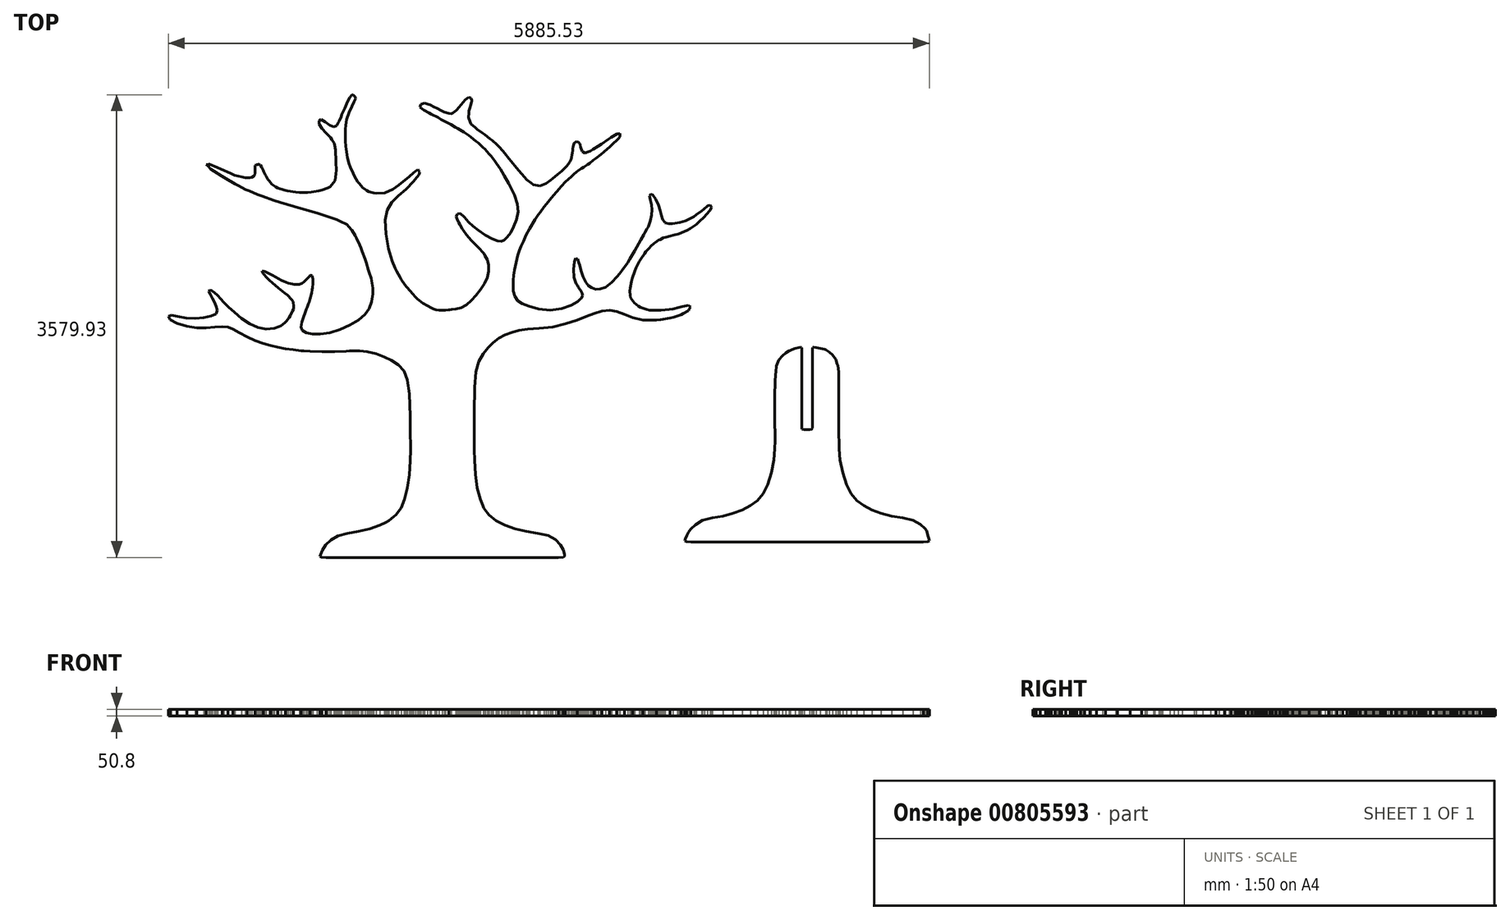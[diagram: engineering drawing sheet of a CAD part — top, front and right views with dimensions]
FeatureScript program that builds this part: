
annotation { "Feature Type Name" : "Feature", "Feature Type Description" : "" }
export const myFeature = defineFeature(function(context is Context, id is Id, definition is map)
    precondition{}
    {
        {
            var Q0;
            Q0=qCreatedBy(makeId("Top.planeOp"),FACE);
            var sketch = newSketch(context, id + "F0", { "sketchPlane" : qUnion([Q0])});
            skLineSegment(sketch, "E0", {"start": v(-5439.15, 1936.53) * mm, "end": v(-5418.75, 1946.97) * mm});
            skLineSegment(sketch, "E1", {"start": v(-5418.75, 1946.97) * mm, "end": v(-5368.69, 1938.08) * mm});
            skLineSegment(sketch, "E2", {"start": v(-5368.69, 1938.08) * mm, "end": v(-5302.09, 1925.05) * mm});
            skLineSegment(sketch, "E3", {"start": v(-5302.09, 1925.05) * mm, "end": v(-5232.04, 1923) * mm});
            skLineSegment(sketch, "E4", {"start": v(-5232.04, 1923) * mm, "end": v(-5165.29, 1928.8) * mm});
            skLineSegment(sketch, "E5", {"start": v(-5165.29, 1928.8) * mm, "end": v(-5108.52, 1939.45) * mm});
            skLineSegment(sketch, "E6", {"start": v(-5108.52, 1939.45) * mm, "end": v(-5071.25, 1957.33) * mm});
            skLineSegment(sketch, "E7", {"start": v(-5071.25, 1957.33) * mm, "end": v(-5063.03, 1984.92) * mm});
            skLineSegment(sketch, "E8", {"start": v(-5063.03, 1984.92) * mm, "end": v(-5071.2, 2016.84) * mm});
            skLineSegment(sketch, "E9", {"start": v(-5071.2, 2016.84) * mm, "end": v(-5083.17, 2047.76) * mm});
            skLineSegment(sketch, "E10", {"start": v(-5083.17, 2047.76) * mm, "end": v(-5098.53, 2078.31) * mm});
            skLineSegment(sketch, "E11", {"start": v(-5098.53, 2078.31) * mm, "end": v(-5116.97, 2109.17) * mm});
            skLineSegment(sketch, "E12", {"start": v(-5116.97, 2109.17) * mm, "end": v(-5128.35, 2132.67) * mm});
            skLineSegment(sketch, "E13", {"start": v(-5128.35, 2132.67) * mm, "end": v(-5122.64, 2141.15) * mm});
            skLineSegment(sketch, "E14", {"start": v(-5122.64, 2141.15) * mm, "end": v(-5105.5, 2136.55) * mm});
            skLineSegment(sketch, "E15", {"start": v(-5105.5, 2136.55) * mm, "end": v(-5082.68, 2120.8) * mm});
            skLineSegment(sketch, "E16", {"start": v(-5082.68, 2120.8) * mm, "end": v(-5058.38, 2098.6) * mm});
            skLineSegment(sketch, "E17", {"start": v(-5058.38, 2098.6) * mm, "end": v(-5036.81, 2074.63) * mm});
            skLineSegment(sketch, "E18", {"start": v(-5036.81, 2074.63) * mm, "end": v(-5011.36, 2046.2) * mm});
            skLineSegment(sketch, "E19", {"start": v(-5011.36, 2046.2) * mm, "end": v(-4975.47, 2010.62) * mm});
            skLineSegment(sketch, "E20", {"start": v(-4975.47, 2010.62) * mm, "end": v(-4929.45, 1968.96) * mm});
            skLineSegment(sketch, "E21", {"start": v(-4929.45, 1968.96) * mm, "end": v(-4873.5, 1922.33) * mm});
            skLineSegment(sketch, "E22", {"start": v(-4873.5, 1922.33) * mm, "end": v(-4811.51, 1880.12) * mm});
            skLineSegment(sketch, "E23", {"start": v(-4811.51, 1880.12) * mm, "end": v(-4747.35, 1851.74) * mm});
            skLineSegment(sketch, "E24", {"start": v(-4747.35, 1851.74) * mm, "end": v(-4683.35, 1839.17) * mm});
            skLineSegment(sketch, "E25", {"start": v(-4683.35, 1839.17) * mm, "end": v(-4621.88, 1844.4) * mm});
            skLineSegment(sketch, "E26", {"start": v(-4621.88, 1844.4) * mm, "end": v(-4585.12, 1858.53) * mm});
            skLineSegment(sketch, "E27", {"start": v(-4585.12, 1858.53) * mm, "end": v(-4568.23, 1865) * mm});
            skLineSegment(sketch, "E28", {"start": v(-4568.23, 1865) * mm, "end": v(-4540.47, 1887.99) * mm});
            skLineSegment(sketch, "E29", {"start": v(-4540.47, 1887.99) * mm, "end": v(-4527.72, 1898.56) * mm});
            skLineSegment(sketch, "E30", {"start": v(-4527.72, 1898.56) * mm, "end": v(-4506.61, 1928.9) * mm});
            skLineSegment(sketch, "E31", {"start": v(-4506.61, 1928.9) * mm, "end": v(-4496.9, 1942.83) * mm});
            skLineSegment(sketch, "E32", {"start": v(-4496.9, 1942.83) * mm, "end": v(-4480.1, 1979) * mm});
            skLineSegment(sketch, "E33", {"start": v(-4480.1, 1979) * mm, "end": v(-4480.1, 1979) * mm});
            skLineSegment(sketch, "E34", {"start": v(-4480.1, 1979) * mm, "end": v(-4472.35, 1995.58) * mm});
            skLineSegment(sketch, "E35", {"start": v(-4472.35, 1995.58) * mm, "end": v(-4472.35, 1995.58) * mm});
            skLineSegment(sketch, "E36", {"start": v(-4472.35, 1995.58) * mm, "end": v(-4472.65, 2012.93) * mm});
            skLineSegment(sketch, "E37", {"start": v(-4472.65, 2012.93) * mm, "end": v(-4473.34, 2050.75) * mm});
            skLineSegment(sketch, "E38", {"start": v(-4473.34, 2050.75) * mm, "end": v(-4473.34, 2050.75) * mm});
            skLineSegment(sketch, "E39", {"start": v(-4473.34, 2050.75) * mm, "end": v(-4487.74, 2066.98) * mm});
            skLineSegment(sketch, "E40", {"start": v(-4487.74, 2066.98) * mm, "end": v(-4519.13, 2102.31) * mm});
            skLineSegment(sketch, "E41", {"start": v(-4519.13, 2102.31) * mm, "end": v(-4519.14, 2102.32) * mm});
            skLineSegment(sketch, "E42", {"start": v(-4519.14, 2102.32) * mm, "end": v(-4540.78, 2119.18) * mm});
            skLineSegment(sketch, "E43", {"start": v(-4540.78, 2119.18) * mm, "end": v(-4587.87, 2155.88) * mm});
            skLineSegment(sketch, "E44", {"start": v(-4587.87, 2155.88) * mm, "end": v(-4635.72, 2197.87) * mm});
            skLineSegment(sketch, "E45", {"start": v(-4635.72, 2197.87) * mm, "end": v(-4657.67, 2217.1) * mm});
            skLineSegment(sketch, "E46", {"start": v(-4657.67, 2217.1) * mm, "end": v(-4673.31, 2233) * mm});
            skLineSegment(sketch, "E47", {"start": v(-4673.31, 2233) * mm, "end": v(-4707.5, 2267.72) * mm});
            skLineSegment(sketch, "E48", {"start": v(-4707.5, 2267.72) * mm, "end": v(-4707.5, 2267.72) * mm});
            skLineSegment(sketch, "E49", {"start": v(-4707.5, 2267.72) * mm, "end": v(-4710.24, 2274.53) * mm});
            skLineSegment(sketch, "E50", {"start": v(-4710.24, 2274.53) * mm, "end": v(-4716.4, 2289.46) * mm});
            skLineSegment(sketch, "E51", {"start": v(-4716.4, 2289.46) * mm, "end": v(-4698.13, 2285.83) * mm});
            skLineSegment(sketch, "E52", {"start": v(-4698.13, 2285.83) * mm, "end": v(-4689.65, 2284.13) * mm});
            skLineSegment(sketch, "E53", {"start": v(-4689.65, 2284.13) * mm, "end": v(-4650.66, 2263.17) * mm});
            skLineSegment(sketch, "E54", {"start": v(-4650.66, 2263.17) * mm, "end": v(-4632.6, 2253.5) * mm});
            skLineSegment(sketch, "E55", {"start": v(-4632.6, 2253.5) * mm, "end": v(-4587.33, 2228.63) * mm});
            skLineSegment(sketch, "E56", {"start": v(-4587.33, 2228.63) * mm, "end": v(-4566.4, 2217.15) * mm});
            skLineSegment(sketch, "E57", {"start": v(-4566.4, 2217.15) * mm, "end": v(-4529.24, 2201.7) * mm});
            skLineSegment(sketch, "E58", {"start": v(-4529.24, 2201.7) * mm, "end": v(-4512.2, 2194.62) * mm});
            skLineSegment(sketch, "E59", {"start": v(-4512.2, 2194.62) * mm, "end": v(-4481.06, 2187.7) * mm});
            skLineSegment(sketch, "E60", {"start": v(-4481.06, 2187.7) * mm, "end": v(-4466.84, 2184.56) * mm});
            skLineSegment(sketch, "E61", {"start": v(-4466.84, 2184.56) * mm, "end": v(-4439.58, 2185.27) * mm});
            skLineSegment(sketch, "E62", {"start": v(-4439.58, 2185.27) * mm, "end": v(-4427.19, 2185.65) * mm});
            skLineSegment(sketch, "E63", {"start": v(-4427.19, 2185.65) * mm, "end": v(-4404.07, 2195.46) * mm});
            skLineSegment(sketch, "E64", {"start": v(-4404.07, 2195.46) * mm, "end": v(-4393.6, 2200.03) * mm});
            skLineSegment(sketch, "E65", {"start": v(-4393.6, 2200.03) * mm, "end": v(-4374.94, 2220.45) * mm});
            skLineSegment(sketch, "E66", {"start": v(-4374.94, 2220.45) * mm, "end": v(-4366.48, 2229.9) * mm});
            skLineSegment(sketch, "E67", {"start": v(-4366.48, 2229.9) * mm, "end": v(-4351.92, 2246.71) * mm});
            skLineSegment(sketch, "E68", {"start": v(-4351.92, 2246.71) * mm, "end": v(-4351.92, 2246.71) * mm});
            skLineSegment(sketch, "E69", {"start": v(-4351.92, 2246.71) * mm, "end": v(-4345.32, 2254.49) * mm});
            skLineSegment(sketch, "E70", {"start": v(-4345.32, 2254.49) * mm, "end": v(-4334.6, 2253.5) * mm});
            skLineSegment(sketch, "E71", {"start": v(-4334.6, 2253.5) * mm, "end": v(-4334.6, 2253.5) * mm});
            skLineSegment(sketch, "E72", {"start": v(-4334.6, 2253.5) * mm, "end": v(-4329.7, 2253.06) * mm});
            skLineSegment(sketch, "E73", {"start": v(-4329.7, 2253.06) * mm, "end": v(-4323.99, 2237.32) * mm});
            skLineSegment(sketch, "E74", {"start": v(-4323.99, 2237.32) * mm, "end": v(-4323.99, 2237.32) * mm});
            skLineSegment(sketch, "E75", {"start": v(-4323.99, 2237.32) * mm, "end": v(-4323.99, 2237.31) * mm});
            skLineSegment(sketch, "E76", {"start": v(-4323.99, 2237.31) * mm, "end": v(-4321.35, 2230.08) * mm});
            skLineSegment(sketch, "E77", {"start": v(-4321.35, 2230.08) * mm, "end": v(-4321.85, 2202.6) * mm});
            skLineSegment(sketch, "E78", {"start": v(-4321.85, 2202.6) * mm, "end": v(-4321.85, 2202.6) * mm});
            skLineSegment(sketch, "E79", {"start": v(-4321.85, 2202.6) * mm, "end": v(-4322.03, 2189.97) * mm});
            skLineSegment(sketch, "E80", {"start": v(-4322.03, 2189.97) * mm, "end": v(-4325.84, 2159.26) * mm});
            skLineSegment(sketch, "E81", {"start": v(-4325.84, 2159.26) * mm, "end": v(-4325.84, 2159.26) * mm});
            skLineSegment(sketch, "E82", {"start": v(-4325.84, 2159.26) * mm, "end": v(-4327.54, 2145.16) * mm});
            skLineSegment(sketch, "E83", {"start": v(-4327.54, 2145.16) * mm, "end": v(-4331.84, 2119.76) * mm});
            skLineSegment(sketch, "E84", {"start": v(-4331.84, 2119.76) * mm, "end": v(-4333.8, 2108.1) * mm});
            skLineSegment(sketch, "E85", {"start": v(-4333.8, 2108.1) * mm, "end": v(-4339.76, 2084.43) * mm});
            skLineSegment(sketch, "E86", {"start": v(-4339.76, 2084.43) * mm, "end": v(-4339.76, 2084.43) * mm});
            skLineSegment(sketch, "E87", {"start": v(-4339.76, 2084.43) * mm, "end": v(-4342.55, 2073.59) * mm});
            skLineSegment(sketch, "E88", {"start": v(-4342.55, 2073.59) * mm, "end": v(-4351.5, 2048.06) * mm});
            skLineSegment(sketch, "E89", {"start": v(-4351.5, 2048.06) * mm, "end": v(-4355.64, 2036.38) * mm});
            skLineSegment(sketch, "E90", {"start": v(-4355.64, 2036.38) * mm, "end": v(-4367.01, 2006.89) * mm});
            skLineSegment(sketch, "E91", {"start": v(-4367.01, 2006.89) * mm, "end": v(-4372.3, 1993.37) * mm});
            skLineSegment(sketch, "E92", {"start": v(-4372.3, 1993.37) * mm, "end": v(-4385.58, 1957.79) * mm});
            skLineSegment(sketch, "E93", {"start": v(-4385.58, 1957.79) * mm, "end": v(-4391.68, 1941.45) * mm});
            skLineSegment(sketch, "E94", {"start": v(-4391.68, 1941.45) * mm, "end": v(-4407.43, 1891.67) * mm});
            skLineSegment(sketch, "E95", {"start": v(-4407.43, 1891.67) * mm, "end": v(-4413.06, 1855.02) * mm});
            skLineSegment(sketch, "E96", {"start": v(-4413.06, 1855.02) * mm, "end": v(-4403.23, 1829.04) * mm});
            skLineSegment(sketch, "E97", {"start": v(-4403.23, 1829.04) * mm, "end": v(-4372.6, 1811.23) * mm});
            skLineSegment(sketch, "E98", {"start": v(-4372.6, 1811.23) * mm, "end": v(-4339.84, 1804.53) * mm});
            skLineSegment(sketch, "E99", {"start": v(-4339.84, 1804.53) * mm, "end": v(-4324.8, 1801.45) * mm});
            skLineSegment(sketch, "E100", {"start": v(-4324.8, 1801.45) * mm, "end": v(-4282.81, 1800.18) * mm});
            skLineSegment(sketch, "E101", {"start": v(-4282.81, 1800.18) * mm, "end": v(-4263.53, 1799.6) * mm});
            skLineSegment(sketch, "E102", {"start": v(-4263.53, 1799.6) * mm, "end": v(-4191.88, 1809.78) * mm});
            skLineSegment(sketch, "E103", {"start": v(-4191.88, 1809.78) * mm, "end": v(-4112.86, 1836.22) * mm});
            skLineSegment(sketch, "E104", {"start": v(-4112.86, 1836.22) * mm, "end": v(-4035.72, 1871.99) * mm});
            skLineSegment(sketch, "E105", {"start": v(-4035.72, 1871.99) * mm, "end": v(-3969.58, 1910.09) * mm});
            skLineSegment(sketch, "E106", {"start": v(-3969.58, 1910.09) * mm, "end": v(-3918.22, 1952) * mm});
            skLineSegment(sketch, "E107", {"start": v(-3918.22, 1952) * mm, "end": v(-3885.3, 1999.24) * mm});
            skLineSegment(sketch, "E108", {"start": v(-3885.3, 1999.24) * mm, "end": v(-3866.79, 2052.68) * mm});
            skLineSegment(sketch, "E109", {"start": v(-3866.79, 2052.68) * mm, "end": v(-3858.6, 2113.21) * mm});
            skLineSegment(sketch, "E110", {"start": v(-3858.6, 2113.21) * mm, "end": v(-3859.85, 2155.58) * mm});
            skLineSegment(sketch, "E111", {"start": v(-3859.85, 2155.58) * mm, "end": v(-3860.41, 2175.06) * mm});
            skLineSegment(sketch, "E112", {"start": v(-3860.41, 2175.06) * mm, "end": v(-3868.2, 2214.35) * mm});
            skLineSegment(sketch, "E113", {"start": v(-3868.2, 2214.35) * mm, "end": v(-3871.8, 2232.46) * mm});
            skLineSegment(sketch, "E114", {"start": v(-3871.8, 2232.46) * mm, "end": v(-3885.4, 2276.71) * mm});
            skLineSegment(sketch, "E115", {"start": v(-3885.4, 2276.71) * mm, "end": v(-3891.65, 2297.06) * mm});
            skLineSegment(sketch, "E116", {"start": v(-3891.65, 2297.06) * mm, "end": v(-3910.37, 2354.3) * mm});
            skLineSegment(sketch, "E117", {"start": v(-3910.37, 2354.3) * mm, "end": v(-3918.96, 2380.47) * mm});
            skLineSegment(sketch, "E118", {"start": v(-3918.96, 2380.47) * mm, "end": v(-3940.78, 2440.26) * mm});
            skLineSegment(sketch, "E119", {"start": v(-3940.78, 2440.26) * mm, "end": v(-3950.76, 2467.6) * mm});
            skLineSegment(sketch, "E120", {"start": v(-3950.76, 2467.6) * mm, "end": v(-3961.25, 2491.4) * mm});
            skLineSegment(sketch, "E121", {"start": v(-3961.25, 2491.4) * mm, "end": v(-3984.1, 2543.23) * mm});
            skLineSegment(sketch, "E122", {"start": v(-3984.1, 2543.23) * mm, "end": v(-3995.39, 2562.51) * mm});
            skLineSegment(sketch, "E123", {"start": v(-3995.39, 2562.51) * mm, "end": v(-4020.02, 2604.4) * mm});
            skLineSegment(sketch, "E124", {"start": v(-4020.02, 2604.4) * mm, "end": v(-4047.15, 2634.24) * mm});
            skLineSegment(sketch, "E125", {"start": v(-4047.15, 2634.24) * mm, "end": v(-4059.6, 2647.96) * mm});
            skLineSegment(sketch, "E126", {"start": v(-4059.6, 2647.96) * mm, "end": v(-4113.42, 2675.03) * mm});
            skLineSegment(sketch, "E127", {"start": v(-4113.42, 2675.03) * mm, "end": v(-4138.06, 2687.43) * mm});
            skLineSegment(sketch, "E128", {"start": v(-4138.06, 2687.43) * mm, "end": v(-4242.86, 2721.03) * mm});
            skLineSegment(sketch, "E129", {"start": v(-4242.86, 2721.03) * mm, "end": v(-4290.61, 2736.32) * mm});
            skLineSegment(sketch, "E130", {"start": v(-4290.61, 2736.32) * mm, "end": v(-4413.4, 2772.04) * mm});
            skLineSegment(sketch, "E131", {"start": v(-4413.4, 2772.04) * mm, "end": v(-4469.05, 2788.21) * mm});
            skLineSegment(sketch, "E132", {"start": v(-4469.05, 2788.21) * mm, "end": v(-4576.44, 2821.57) * mm});
            skLineSegment(sketch, "E133", {"start": v(-4576.44, 2821.57) * mm, "end": v(-4625.15, 2836.7) * mm});
            skLineSegment(sketch, "E134", {"start": v(-4625.15, 2836.7) * mm, "end": v(-4712.25, 2867.03) * mm});
            skLineSegment(sketch, "E135", {"start": v(-4712.25, 2867.03) * mm, "end": v(-4751.9, 2880.82) * mm});
            skLineSegment(sketch, "E136", {"start": v(-4751.9, 2880.82) * mm, "end": v(-4813.9, 2907.52) * mm});
            skLineSegment(sketch, "E137", {"start": v(-4813.9, 2907.52) * mm, "end": v(-4842.25, 2919.7) * mm});
            skLineSegment(sketch, "E138", {"start": v(-4842.25, 2919.7) * mm, "end": v(-4898.64, 2949.81) * mm});
            skLineSegment(sketch, "E139", {"start": v(-4898.64, 2949.81) * mm, "end": v(-4924.5, 2963.6) * mm});
            skLineSegment(sketch, "E140", {"start": v(-4924.5, 2963.6) * mm, "end": v(-4994.67, 3004.07) * mm});
            skLineSegment(sketch, "E141", {"start": v(-4994.67, 3004.07) * mm, "end": v(-5027.03, 3022.7) * mm});
            skLineSegment(sketch, "E142", {"start": v(-5027.03, 3022.7) * mm, "end": v(-5085.86, 3061.04) * mm});
            skLineSegment(sketch, "E143", {"start": v(-5085.86, 3061.04) * mm, "end": v(-5113.11, 3078.76) * mm});
            skLineSegment(sketch, "E144", {"start": v(-5113.11, 3078.76) * mm, "end": v(-5135.54, 3102.5) * mm});
            skLineSegment(sketch, "E145", {"start": v(-5135.54, 3102.5) * mm, "end": v(-5135.54, 3102.5) * mm});
            skLineSegment(sketch, "E146", {"start": v(-5135.54, 3102.5) * mm, "end": v(-5145.96, 3113.51) * mm});
            skLineSegment(sketch, "E147", {"start": v(-5145.96, 3113.51) * mm, "end": v(-5128.79, 3115.4) * mm});
            skLineSegment(sketch, "E148", {"start": v(-5128.79, 3115.4) * mm, "end": v(-5128.79, 3115.4) * mm});
            skLineSegment(sketch, "E149", {"start": v(-5128.79, 3115.4) * mm, "end": v(-5120.84, 3116.28) * mm});
            skLineSegment(sketch, "E150", {"start": v(-5120.84, 3116.28) * mm, "end": v(-5060.76, 3089.05) * mm});
            skLineSegment(sketch, "E151", {"start": v(-5060.76, 3089.05) * mm, "end": v(-5033.03, 3076.48) * mm});
            skLineSegment(sketch, "E152", {"start": v(-5033.03, 3076.48) * mm, "end": v(-4960.18, 3044.25) * mm});
            skLineSegment(sketch, "E153", {"start": v(-4960.18, 3044.25) * mm, "end": v(-4926.7, 3029.44) * mm});
            skLineSegment(sketch, "E154", {"start": v(-4926.7, 3029.44) * mm, "end": v(-4871.36, 3016.46) * mm});
            skLineSegment(sketch, "E155", {"start": v(-4871.36, 3016.46) * mm, "end": v(-4846.03, 3010.52) * mm});
            skLineSegment(sketch, "E156", {"start": v(-4846.03, 3010.52) * mm, "end": v(-4810.02, 3012.17) * mm});
            skLineSegment(sketch, "E157", {"start": v(-4810.02, 3012.17) * mm, "end": v(-4793.56, 3012.93) * mm});
            skLineSegment(sketch, "E158", {"start": v(-4793.56, 3012.93) * mm, "end": v(-4793.56, 3012.93) * mm});
            skLineSegment(sketch, "E159", {"start": v(-4793.56, 3012.93) * mm, "end": v(-4793.55, 3012.93) * mm});
            skLineSegment(sketch, "E160", {"start": v(-4793.55, 3012.93) * mm, "end": v(-4778.65, 3024.59) * mm});
            skLineSegment(sketch, "E161", {"start": v(-4778.65, 3024.59) * mm, "end": v(-4771.86, 3029.9) * mm});
            skLineSegment(sketch, "E162", {"start": v(-4771.86, 3029.9) * mm, "end": v(-4769.22, 3047.3) * mm});
            skLineSegment(sketch, "E163", {"start": v(-4769.22, 3047.3) * mm, "end": v(-4769.22, 3047.3) * mm});
            skLineSegment(sketch, "E164", {"start": v(-4769.22, 3047.3) * mm, "end": v(-4768.03, 3055.25) * mm});
            skLineSegment(sketch, "E165", {"start": v(-4768.03, 3055.25) * mm, "end": v(-4768.03, 3055.25) * mm});
            skLineSegment(sketch, "E166", {"start": v(-4768.03, 3055.25) * mm, "end": v(-4768.87, 3074.17) * mm});
            skLineSegment(sketch, "E167", {"start": v(-4768.87, 3074.17) * mm, "end": v(-4768.87, 3074.17) * mm});
            skLineSegment(sketch, "E168", {"start": v(-4768.87, 3074.17) * mm, "end": v(-4769.25, 3082.8) * mm});
            skLineSegment(sketch, "E169", {"start": v(-4769.25, 3082.8) * mm, "end": v(-4769.25, 3082.8) * mm});
            skLineSegment(sketch, "E170", {"start": v(-4769.25, 3082.8) * mm, "end": v(-4768.9, 3097.77) * mm});
            skLineSegment(sketch, "E171", {"start": v(-4768.9, 3097.77) * mm, "end": v(-4768.9, 3097.77) * mm});
            skLineSegment(sketch, "E172", {"start": v(-4768.9, 3097.77) * mm, "end": v(-4768.72, 3104.6) * mm});
            skLineSegment(sketch, "E173", {"start": v(-4768.72, 3104.6) * mm, "end": v(-4762.52, 3110.09) * mm});
            skLineSegment(sketch, "E174", {"start": v(-4762.52, 3110.09) * mm, "end": v(-4762.52, 3110.09) * mm});
            skLineSegment(sketch, "E175", {"start": v(-4762.52, 3110.09) * mm, "end": v(-4759.7, 3112.57) * mm});
            skLineSegment(sketch, "E176", {"start": v(-4759.7, 3112.57) * mm, "end": v(-4759.7, 3112.57) * mm});
            skLineSegment(sketch, "E177", {"start": v(-4759.7, 3112.57) * mm, "end": v(-4751.24, 3113.29) * mm});
            skLineSegment(sketch, "E178", {"start": v(-4751.24, 3113.29) * mm, "end": v(-4751.24, 3113.29) * mm});
            skLineSegment(sketch, "E179", {"start": v(-4751.24, 3113.29) * mm, "end": v(-4747.35, 3113.6) * mm});
            skLineSegment(sketch, "E180", {"start": v(-4747.35, 3113.6) * mm, "end": v(-4740.22, 3114.17) * mm});
            skLineSegment(sketch, "E181", {"start": v(-4740.22, 3114.17) * mm, "end": v(-4740.22, 3114.17) * mm});
            skLineSegment(sketch, "E182", {"start": v(-4740.22, 3114.17) * mm, "end": v(-4736.94, 3114.45) * mm});
            skLineSegment(sketch, "E183", {"start": v(-4736.94, 3114.45) * mm, "end": v(-4736.94, 3114.45) * mm});
            skLineSegment(sketch, "E184", {"start": v(-4736.94, 3114.45) * mm, "end": v(-4729.98, 3110.14) * mm});
            skLineSegment(sketch, "E185", {"start": v(-4729.98, 3110.14) * mm, "end": v(-4729.98, 3110.14) * mm});
            skLineSegment(sketch, "E186", {"start": v(-4729.98, 3110.14) * mm, "end": v(-4726.8, 3108.18) * mm});
            skLineSegment(sketch, "E187", {"start": v(-4726.8, 3108.18) * mm, "end": v(-4718.9, 3094.13) * mm});
            skLineSegment(sketch, "E188", {"start": v(-4718.9, 3094.13) * mm, "end": v(-4718.9, 3094.13) * mm});
            skLineSegment(sketch, "E189", {"start": v(-4718.9, 3094.13) * mm, "end": v(-4715.32, 3087.76) * mm});
            skLineSegment(sketch, "E190", {"start": v(-4715.32, 3087.76) * mm, "end": v(-4705.75, 3067.24) * mm});
            skLineSegment(sketch, "E191", {"start": v(-4705.75, 3067.24) * mm, "end": v(-4701.4, 3057.89) * mm});
            skLineSegment(sketch, "E192", {"start": v(-4701.4, 3057.89) * mm, "end": v(-4689.4, 3034.11) * mm});
            skLineSegment(sketch, "E193", {"start": v(-4689.4, 3034.11) * mm, "end": v(-4689.4, 3034.11) * mm});
            skLineSegment(sketch, "E194", {"start": v(-4689.4, 3034.11) * mm, "end": v(-4683.93, 3023.3) * mm});
            skLineSegment(sketch, "E195", {"start": v(-4683.93, 3023.3) * mm, "end": v(-4683.93, 3023.3) * mm});
            skLineSegment(sketch, "E196", {"start": v(-4683.93, 3023.3) * mm, "end": v(-4669.6, 2999.44) * mm});
            skLineSegment(sketch, "E197", {"start": v(-4669.6, 2999.44) * mm, "end": v(-4663.1, 2988.62) * mm});
            skLineSegment(sketch, "E198", {"start": v(-4663.1, 2988.62) * mm, "end": v(-4646.54, 2967.92) * mm});
            skLineSegment(sketch, "E199", {"start": v(-4646.54, 2967.92) * mm, "end": v(-4639.02, 2958.52) * mm});
            skLineSegment(sketch, "E200", {"start": v(-4639.02, 2958.52) * mm, "end": v(-4639.02, 2958.52) * mm});
            skLineSegment(sketch, "E201", {"start": v(-4639.02, 2958.52) * mm, "end": v(-4609.6, 2940.44) * mm});
            skLineSegment(sketch, "E202", {"start": v(-4609.6, 2940.44) * mm, "end": v(-4596.3, 2932.26) * mm});
            skLineSegment(sketch, "E203", {"start": v(-4596.3, 2932.26) * mm, "end": v(-4543.37, 2916.28) * mm});
            skLineSegment(sketch, "E204", {"start": v(-4543.37, 2916.28) * mm, "end": v(-4519.47, 2909.07) * mm});
            skLineSegment(sketch, "E205", {"start": v(-4519.47, 2909.07) * mm, "end": v(-4455, 2899.85) * mm});
            skLineSegment(sketch, "E206", {"start": v(-4455, 2899.85) * mm, "end": v(-4425.9, 2895.68) * mm});
            skLineSegment(sketch, "E207", {"start": v(-4425.9, 2895.68) * mm, "end": v(-4361.96, 2897.84) * mm});
            skLineSegment(sketch, "E208", {"start": v(-4361.96, 2897.84) * mm, "end": v(-4333, 2898.8) * mm});
            skLineSegment(sketch, "E209", {"start": v(-4333, 2898.8) * mm, "end": v(-4276.46, 2909.88) * mm});
            skLineSegment(sketch, "E210", {"start": v(-4276.46, 2909.88) * mm, "end": v(-4276.46, 2909.88) * mm});
            skLineSegment(sketch, "E211", {"start": v(-4276.46, 2909.88) * mm, "end": v(-4250.73, 2914.91) * mm});
            skLineSegment(sketch, "E212", {"start": v(-4250.73, 2914.91) * mm, "end": v(-4208.4, 2932.4) * mm});
            skLineSegment(sketch, "E213", {"start": v(-4208.4, 2932.4) * mm, "end": v(-4208.4, 2932.41) * mm});
            skLineSegment(sketch, "E214", {"start": v(-4208.4, 2932.41) * mm, "end": v(-4189.06, 2940.39) * mm});
            skLineSegment(sketch, "E215", {"start": v(-4189.06, 2940.39) * mm, "end": v(-4163.18, 2972.8) * mm});
            skLineSegment(sketch, "E216", {"start": v(-4163.18, 2972.8) * mm, "end": v(-4151.32, 2987.63) * mm});
            skLineSegment(sketch, "E217", {"start": v(-4151.32, 2987.63) * mm, "end": v(-4144.15, 3043.44) * mm});
            skLineSegment(sketch, "E218", {"start": v(-4144.15, 3043.44) * mm, "end": v(-4140.88, 3069.04) * mm});
            skLineSegment(sketch, "E219", {"start": v(-4140.88, 3069.04) * mm, "end": v(-4142.96, 3129.67) * mm});
            skLineSegment(sketch, "E220", {"start": v(-4142.96, 3129.67) * mm, "end": v(-4143.92, 3157.48) * mm});
            skLineSegment(sketch, "E221", {"start": v(-4143.92, 3157.48) * mm, "end": v(-4145.8, 3204.4) * mm});
            skLineSegment(sketch, "E222", {"start": v(-4145.8, 3204.4) * mm, "end": v(-4146.67, 3225.93) * mm});
            skLineSegment(sketch, "E223", {"start": v(-4146.67, 3225.93) * mm, "end": v(-4154.04, 3262.18) * mm});
            skLineSegment(sketch, "E224", {"start": v(-4154.04, 3262.18) * mm, "end": v(-4157.41, 3278.8) * mm});
            skLineSegment(sketch, "E225", {"start": v(-4157.41, 3278.8) * mm, "end": v(-4175.96, 3307.42) * mm});
            skLineSegment(sketch, "E226", {"start": v(-4175.96, 3307.42) * mm, "end": v(-4184.46, 3320.55) * mm});
            skLineSegment(sketch, "E227", {"start": v(-4184.46, 3320.55) * mm, "end": v(-4218.98, 3356.82) * mm});
            skLineSegment(sketch, "E228", {"start": v(-4218.98, 3356.82) * mm, "end": v(-4252.18, 3393.14) * mm});
            skLineSegment(sketch, "E229", {"start": v(-4252.18, 3393.14) * mm, "end": v(-4274.1, 3426.14) * mm});
            skLineSegment(sketch, "E230", {"start": v(-4274.1, 3426.14) * mm, "end": v(-4274.1, 3426.14) * mm});
            skLineSegment(sketch, "E231", {"start": v(-4274.1, 3426.14) * mm, "end": v(-4274.84, 3452.35) * mm});
            skLineSegment(sketch, "E232", {"start": v(-4274.84, 3452.35) * mm, "end": v(-4257.62, 3461.3) * mm});
            skLineSegment(sketch, "E233", {"start": v(-4257.62, 3461.3) * mm, "end": v(-4225.8, 3442.52) * mm});
            skLineSegment(sketch, "E234", {"start": v(-4225.8, 3442.52) * mm, "end": v(-4190.1, 3417) * mm});
            skLineSegment(sketch, "E235", {"start": v(-4190.1, 3417) * mm, "end": v(-4161.33, 3405.72) * mm});
            skLineSegment(sketch, "E236", {"start": v(-4161.33, 3405.72) * mm, "end": v(-4137.78, 3414.48) * mm});
            skLineSegment(sketch, "E237", {"start": v(-4137.78, 3414.48) * mm, "end": v(-4124.04, 3438.25) * mm});
            skLineSegment(sketch, "E238", {"start": v(-4124.04, 3438.25) * mm, "end": v(-4124.04, 3438.25) * mm});
            skLineSegment(sketch, "E239", {"start": v(-4124.04, 3438.25) * mm, "end": v(-4117.71, 3449.15) * mm});
            skLineSegment(sketch, "E240", {"start": v(-4117.71, 3449.15) * mm, "end": v(-4104.25, 3482.83) * mm});
            skLineSegment(sketch, "E241", {"start": v(-4104.25, 3482.83) * mm, "end": v(-4104.25, 3482.83) * mm});
            skLineSegment(sketch, "E242", {"start": v(-4104.25, 3482.83) * mm, "end": v(-4098.08, 3498.27) * mm});
            skLineSegment(sketch, "E243", {"start": v(-4098.08, 3498.27) * mm, "end": v(-4075.78, 3550.4) * mm});
            skLineSegment(sketch, "E244", {"start": v(-4075.78, 3550.4) * mm, "end": v(-4053.73, 3597.66) * mm});
            skLineSegment(sketch, "E245", {"start": v(-4053.73, 3597.66) * mm, "end": v(-4034.88, 3632.18) * mm});
            skLineSegment(sketch, "E246", {"start": v(-4034.88, 3632.18) * mm, "end": v(-4019.85, 3651.1) * mm});
            skLineSegment(sketch, "E247", {"start": v(-4019.85, 3651.1) * mm, "end": v(-4019.85, 3651.1) * mm});
            skLineSegment(sketch, "E248", {"start": v(-4019.85, 3651.1) * mm, "end": v(-4009.26, 3651.59) * mm});
            skLineSegment(sketch, "E249", {"start": v(-4009.26, 3651.59) * mm, "end": v(-4001.2, 3643.13) * mm});
            skLineSegment(sketch, "E250", {"start": v(-4001.2, 3643.13) * mm, "end": v(-4001.2, 3643.13) * mm});
            skLineSegment(sketch, "E251", {"start": v(-4001.2, 3643.13) * mm, "end": v(-3993.71, 3635.28) * mm});
            skLineSegment(sketch, "E252", {"start": v(-3993.71, 3635.28) * mm, "end": v(-3993.71, 3635.28) * mm});
            skLineSegment(sketch, "E253", {"start": v(-3993.71, 3635.28) * mm, "end": v(-3992.44, 3622.38) * mm});
            skLineSegment(sketch, "E254", {"start": v(-3992.44, 3622.38) * mm, "end": v(-4003.1, 3598.8) * mm});
            skLineSegment(sketch, "E255", {"start": v(-4003.1, 3598.8) * mm, "end": v(-4021.17, 3563.32) * mm});
            skLineSegment(sketch, "E256", {"start": v(-4021.17, 3563.32) * mm, "end": v(-4042.1, 3514.78) * mm});
            skLineSegment(sketch, "E257", {"start": v(-4042.1, 3514.78) * mm, "end": v(-4060.1, 3462.66) * mm});
            skLineSegment(sketch, "E258", {"start": v(-4060.1, 3462.66) * mm, "end": v(-4069.3, 3416.54) * mm});
            skLineSegment(sketch, "E259", {"start": v(-4069.3, 3416.54) * mm, "end": v(-4071.51, 3384.25) * mm});
            skLineSegment(sketch, "E260", {"start": v(-4071.51, 3384.25) * mm, "end": v(-4072.52, 3369.42) * mm});
            skLineSegment(sketch, "E261", {"start": v(-4072.52, 3369.42) * mm, "end": v(-4072.58, 3331.7) * mm});
            skLineSegment(sketch, "E262", {"start": v(-4072.58, 3331.7) * mm, "end": v(-4072.58, 3331.7) * mm});
            skLineSegment(sketch, "E263", {"start": v(-4072.58, 3331.7) * mm, "end": v(-4072.6, 3314.4) * mm});
            skLineSegment(sketch, "E264", {"start": v(-4072.6, 3314.4) * mm, "end": v(-4071.3, 3295.12) * mm});
            skLineSegment(sketch, "E265", {"start": v(-4071.3, 3295.12) * mm, "end": v(-4068.49, 3253.09) * mm});
            skLineSegment(sketch, "E266", {"start": v(-4068.49, 3253.09) * mm, "end": v(-4068.49, 3253.09) * mm});
            skLineSegment(sketch, "E267", {"start": v(-4068.49, 3253.09) * mm, "end": v(-4065.57, 3232.39) * mm});
            skLineSegment(sketch, "E268", {"start": v(-4065.57, 3232.39) * mm, "end": v(-4059.2, 3187.15) * mm});
            skLineSegment(sketch, "E269", {"start": v(-4059.2, 3187.15) * mm, "end": v(-4053.6, 3165.23) * mm});
            skLineSegment(sketch, "E270", {"start": v(-4053.6, 3165.23) * mm, "end": v(-4041.39, 3117.4) * mm});
            skLineSegment(sketch, "E271", {"start": v(-4041.39, 3117.4) * mm, "end": v(-4032.09, 3094.49) * mm});
            skLineSegment(sketch, "E272", {"start": v(-4032.09, 3094.49) * mm, "end": v(-4011.8, 3044.65) * mm});
            skLineSegment(sketch, "E273", {"start": v(-4011.8, 3044.65) * mm, "end": v(-4011.8, 3044.65) * mm});
            skLineSegment(sketch, "E274", {"start": v(-4011.8, 3044.65) * mm, "end": v(-4000.31, 3024.18) * mm});
            skLineSegment(sketch, "E275", {"start": v(-4000.31, 3024.18) * mm, "end": v(-3975.3, 2979.73) * mm});
            skLineSegment(sketch, "E276", {"start": v(-3975.3, 2979.73) * mm, "end": v(-3963.18, 2965.18) * mm});
            skLineSegment(sketch, "E277", {"start": v(-3963.18, 2965.18) * mm, "end": v(-3936.76, 2933.48) * mm});
            skLineSegment(sketch, "E278", {"start": v(-3936.76, 2933.48) * mm, "end": v(-3905.3, 2913.16) * mm});
            skLineSegment(sketch, "E279", {"start": v(-3905.3, 2913.16) * mm, "end": v(-3890.84, 2903.83) * mm});
            skLineSegment(sketch, "E280", {"start": v(-3890.84, 2903.83) * mm, "end": v(-3850.63, 2893.55) * mm});
            skLineSegment(sketch, "E281", {"start": v(-3850.63, 2893.55) * mm, "end": v(-3850.63, 2893.55) * mm});
            skLineSegment(sketch, "E282", {"start": v(-3850.63, 2893.55) * mm, "end": v(-3832.2, 2888.83) * mm});
            skLineSegment(sketch, "E283", {"start": v(-3832.2, 2888.83) * mm, "end": v(-3767.35, 2893.42) * mm});
            skLineSegment(sketch, "E284", {"start": v(-3767.35, 2893.42) * mm, "end": v(-3702.9, 2922.66) * mm});
            skLineSegment(sketch, "E285", {"start": v(-3702.9, 2922.66) * mm, "end": v(-3659.27, 2953.8) * mm});
            skLineSegment(sketch, "E286", {"start": v(-3659.27, 2953.8) * mm, "end": v(-3659.27, 2953.8) * mm});
            skLineSegment(sketch, "E287", {"start": v(-3659.27, 2953.8) * mm, "end": v(-3639.23, 2968.12) * mm});
            skLineSegment(sketch, "E288", {"start": v(-3639.23, 2968.12) * mm, "end": v(-3596.35, 3004.6) * mm});
            skLineSegment(sketch, "E289", {"start": v(-3596.35, 3004.6) * mm, "end": v(-3576.67, 3021.34) * mm});
            skLineSegment(sketch, "E290", {"start": v(-3576.67, 3021.34) * mm, "end": v(-3543.98, 3049.7) * mm});
            skLineSegment(sketch, "E291", {"start": v(-3543.98, 3049.7) * mm, "end": v(-3543.97, 3049.71) * mm});
            skLineSegment(sketch, "E292", {"start": v(-3543.97, 3049.71) * mm, "end": v(-3528.97, 3062.74) * mm});
            skLineSegment(sketch, "E293", {"start": v(-3528.97, 3062.74) * mm, "end": v(-3509.79, 3072.65) * mm});
            skLineSegment(sketch, "E294", {"start": v(-3509.79, 3072.65) * mm, "end": v(-3503.82, 3065.53) * mm});
            skLineSegment(sketch, "E295", {"start": v(-3503.82, 3065.53) * mm, "end": v(-3503.82, 3065.53) * mm});
            skLineSegment(sketch, "E296", {"start": v(-3503.82, 3065.53) * mm, "end": v(-3498.23, 3058.9) * mm});
            skLineSegment(sketch, "E297", {"start": v(-3498.23, 3058.9) * mm, "end": v(-3498.23, 3058.9) * mm});
            skLineSegment(sketch, "E298", {"start": v(-3498.23, 3058.9) * mm, "end": v(-3495.67, 3055.86) * mm});
            skLineSegment(sketch, "E299", {"start": v(-3495.67, 3055.86) * mm, "end": v(-3500.8, 3039.37) * mm});
            skLineSegment(sketch, "E300", {"start": v(-3500.8, 3039.37) * mm, "end": v(-3503.16, 3031.78) * mm});
            skLineSegment(sketch, "E301", {"start": v(-3503.16, 3031.78) * mm, "end": v(-3531.23, 2997.36) * mm});
            skLineSegment(sketch, "E302", {"start": v(-3531.23, 2997.36) * mm, "end": v(-3544.13, 2981.54) * mm});
            skLineSegment(sketch, "E303", {"start": v(-3544.13, 2981.54) * mm, "end": v(-3602.2, 2922.3) * mm});
            skLineSegment(sketch, "E304", {"start": v(-3602.2, 2922.3) * mm, "end": v(-3661.05, 2871.3) * mm});
            skLineSegment(sketch, "E305", {"start": v(-3661.05, 2871.3) * mm, "end": v(-3711.97, 2820.32) * mm});
            skLineSegment(sketch, "E306", {"start": v(-3711.97, 2820.32) * mm, "end": v(-3746.24, 2761.22) * mm});
            skLineSegment(sketch, "E307", {"start": v(-3746.24, 2761.22) * mm, "end": v(-3761.96, 2683.26) * mm});
            skLineSegment(sketch, "E308", {"start": v(-3761.96, 2683.26) * mm, "end": v(-3757.29, 2575.77) * mm});
            skLineSegment(sketch, "E309", {"start": v(-3757.29, 2575.77) * mm, "end": v(-3744.03, 2498.2) * mm});
            skLineSegment(sketch, "E310", {"start": v(-3744.03, 2498.2) * mm, "end": v(-3737.93, 2462.59) * mm});
            skLineSegment(sketch, "E311", {"start": v(-3737.93, 2462.59) * mm, "end": v(-3718.55, 2397.46) * mm});
            skLineSegment(sketch, "E312", {"start": v(-3718.55, 2397.46) * mm, "end": v(-3709.66, 2367.57) * mm});
            skLineSegment(sketch, "E313", {"start": v(-3709.66, 2367.57) * mm, "end": v(-3686.17, 2313.21) * mm});
            skLineSegment(sketch, "E314", {"start": v(-3686.17, 2313.21) * mm, "end": v(-3675.37, 2288.24) * mm});
            skLineSegment(sketch, "E315", {"start": v(-3675.37, 2288.24) * mm, "end": v(-3649.77, 2243) * mm});
            skLineSegment(sketch, "E316", {"start": v(-3649.77, 2243) * mm, "end": v(-3649.77, 2243) * mm});
            skLineSegment(sketch, "E317", {"start": v(-3649.77, 2243) * mm, "end": v(-3638.03, 2222.23) * mm});
            skLineSegment(sketch, "E318", {"start": v(-3638.03, 2222.23) * mm, "end": v(-3610.32, 2183.31) * mm});
            skLineSegment(sketch, "E319", {"start": v(-3610.32, 2183.31) * mm, "end": v(-3597.6, 2165.46) * mm});
            skLineSegment(sketch, "E320", {"start": v(-3597.6, 2165.46) * mm, "end": v(-3567.78, 2130.13) * mm});
            skLineSegment(sketch, "E321", {"start": v(-3567.78, 2130.13) * mm, "end": v(-3554.09, 2113.92) * mm});
            skLineSegment(sketch, "E322", {"start": v(-3554.09, 2113.92) * mm, "end": v(-3524.32, 2084.53) * mm});
            skLineSegment(sketch, "E323", {"start": v(-3524.32, 2084.53) * mm, "end": v(-3510.65, 2071.02) * mm});
            skLineSegment(sketch, "E324", {"start": v(-3510.65, 2071.02) * mm, "end": v(-3470.57, 2040.16) * mm});
            skLineSegment(sketch, "E325", {"start": v(-3470.57, 2040.16) * mm, "end": v(-3435.57, 2018.7) * mm});
            skLineSegment(sketch, "E326", {"start": v(-3435.57, 2018.7) * mm, "end": v(-3407.5, 2004) * mm});
            skLineSegment(sketch, "E327", {"start": v(-3407.5, 2004) * mm, "end": v(-3388.1, 1995.03) * mm});
            skLineSegment(sketch, "E328", {"start": v(-3388.1, 1995.03) * mm, "end": v(-3379.06, 1990.86) * mm});
            skLineSegment(sketch, "E329", {"start": v(-3379.06, 1990.86) * mm, "end": v(-3379.06, 1990.86) * mm});
            skLineSegment(sketch, "E330", {"start": v(-3379.06, 1990.86) * mm, "end": v(-3369.35, 1988.85) * mm});
            skLineSegment(sketch, "E331", {"start": v(-3369.35, 1988.85) * mm, "end": v(-3347.9, 1986.36) * mm});
            skLineSegment(sketch, "E332", {"start": v(-3347.9, 1986.36) * mm, "end": v(-3321.12, 1985) * mm});
            skLineSegment(sketch, "E333", {"start": v(-3321.12, 1985) * mm, "end": v(-3295.52, 1986.36) * mm});
            skLineSegment(sketch, "E334", {"start": v(-3295.52, 1986.36) * mm, "end": v(-3275.07, 1988.55) * mm});
            skLineSegment(sketch, "E335", {"start": v(-3275.07, 1988.55) * mm, "end": v(-3263.76, 1989.7) * mm});
            skLineSegment(sketch, "E336", {"start": v(-3263.76, 1989.7) * mm, "end": v(-3248.7, 1991.04) * mm});
            skLineSegment(sketch, "E337", {"start": v(-3248.7, 1991.04) * mm, "end": v(-3216.88, 1993.88) * mm});
            skLineSegment(sketch, "E338", {"start": v(-3216.88, 1993.88) * mm, "end": v(-3176.5, 2003.94) * mm});
            skLineSegment(sketch, "E339", {"start": v(-3176.5, 2003.94) * mm, "end": v(-3135.67, 2026.93) * mm});
            skLineSegment(sketch, "E340", {"start": v(-3135.67, 2026.93) * mm, "end": v(-3096.3, 2059.8) * mm});
            skLineSegment(sketch, "E341", {"start": v(-3096.3, 2059.8) * mm, "end": v(-3060.24, 2099.47) * mm});
            skLineSegment(sketch, "E342", {"start": v(-3060.24, 2099.47) * mm, "end": v(-3026.96, 2144.02) * mm});
            skLineSegment(sketch, "E343", {"start": v(-3026.96, 2144.02) * mm, "end": v(-2995.97, 2191.52) * mm});
            skLineSegment(sketch, "E344", {"start": v(-2995.97, 2191.52) * mm, "end": v(-2972.45, 2240.16) * mm});
            skLineSegment(sketch, "E345", {"start": v(-2972.45, 2240.16) * mm, "end": v(-2961.45, 2288.04) * mm});
            skLineSegment(sketch, "E346", {"start": v(-2961.45, 2288.04) * mm, "end": v(-2961.89, 2334.01) * mm});
            skLineSegment(sketch, "E347", {"start": v(-2961.89, 2334.01) * mm, "end": v(-2969.25, 2363.45) * mm});
            skLineSegment(sketch, "E348", {"start": v(-2969.25, 2363.45) * mm, "end": v(-2969.25, 2363.45) * mm});
            skLineSegment(sketch, "E349", {"start": v(-2969.25, 2363.45) * mm, "end": v(-2972.6, 2376.97) * mm});
            skLineSegment(sketch, "E350", {"start": v(-2972.6, 2376.97) * mm, "end": v(-2990.56, 2407.78) * mm});
            skLineSegment(sketch, "E351", {"start": v(-2990.56, 2407.78) * mm, "end": v(-2998.82, 2421.95) * mm});
            skLineSegment(sketch, "E352", {"start": v(-2998.82, 2421.95) * mm, "end": v(-3045.73, 2474.04) * mm});
            skLineSegment(sketch, "E353", {"start": v(-3045.73, 2474.04) * mm, "end": v(-3080.6, 2509.6) * mm});
            skLineSegment(sketch, "E354", {"start": v(-3080.6, 2509.6) * mm, "end": v(-3096.63, 2525.91) * mm});
            skLineSegment(sketch, "E355", {"start": v(-3096.63, 2525.91) * mm, "end": v(-3134.76, 2570.1) * mm});
            skLineSegment(sketch, "E356", {"start": v(-3134.76, 2570.1) * mm, "end": v(-3156.04, 2599.98) * mm});
            skLineSegment(sketch, "E357", {"start": v(-3156.04, 2599.98) * mm, "end": v(-3165.82, 2613.7) * mm});
            skLineSegment(sketch, "E358", {"start": v(-3165.82, 2613.7) * mm, "end": v(-3186.2, 2647.98) * mm});
            skLineSegment(sketch, "E359", {"start": v(-3186.2, 2647.98) * mm, "end": v(-3195.57, 2663.73) * mm});
            skLineSegment(sketch, "E360", {"start": v(-3195.57, 2663.73) * mm, "end": v(-3207, 2693.8) * mm});
            skLineSegment(sketch, "E361", {"start": v(-3207, 2693.8) * mm, "end": v(-3207, 2693.8) * mm});
            skLineSegment(sketch, "E362", {"start": v(-3207, 2693.8) * mm, "end": v(-3212.25, 2707.6) * mm});
            skLineSegment(sketch, "E363", {"start": v(-3212.25, 2707.6) * mm, "end": v(-3204.25, 2732.72) * mm});
            skLineSegment(sketch, "E364", {"start": v(-3204.25, 2732.72) * mm, "end": v(-3180.63, 2734.16) * mm});
            skLineSegment(sketch, "E365", {"start": v(-3180.63, 2734.16) * mm, "end": v(-3150.56, 2707.09) * mm});
            skLineSegment(sketch, "E366", {"start": v(-3150.56, 2707.09) * mm, "end": v(-3117.18, 2668.46) * mm});
            skLineSegment(sketch, "E367", {"start": v(-3117.18, 2668.46) * mm, "end": v(-3083.68, 2635.23) * mm});
            skLineSegment(sketch, "E368", {"start": v(-3083.68, 2635.23) * mm, "end": v(-3042.84, 2602.9) * mm});
            skLineSegment(sketch, "E369", {"start": v(-3042.84, 2602.9) * mm, "end": v(-2987.51, 2566.93) * mm});
            skLineSegment(sketch, "E370", {"start": v(-2987.51, 2566.93) * mm, "end": v(-2932.8, 2536.68) * mm});
            skLineSegment(sketch, "E371", {"start": v(-2932.8, 2536.68) * mm, "end": v(-2893.87, 2521.57) * mm});
            skLineSegment(sketch, "E372", {"start": v(-2893.87, 2521.57) * mm, "end": v(-2865.21, 2519.61) * mm});
            skLineSegment(sketch, "E373", {"start": v(-2865.21, 2519.61) * mm, "end": v(-2841.41, 2528.8) * mm});
            skLineSegment(sketch, "E374", {"start": v(-2841.41, 2528.8) * mm, "end": v(-2818.63, 2550.32) * mm});
            skLineSegment(sketch, "E375", {"start": v(-2818.63, 2550.32) * mm, "end": v(-2793.08, 2585.3) * mm});
            skLineSegment(sketch, "E376", {"start": v(-2793.08, 2585.3) * mm, "end": v(-2767.93, 2631.63) * mm});
            skLineSegment(sketch, "E377", {"start": v(-2767.93, 2631.63) * mm, "end": v(-2746.4, 2687.1) * mm});
            skLineSegment(sketch, "E378", {"start": v(-2746.4, 2687.1) * mm, "end": v(-2734.91, 2747) * mm});
            skLineSegment(sketch, "E379", {"start": v(-2734.91, 2747) * mm, "end": v(-2739.97, 2806.6) * mm});
            skLineSegment(sketch, "E380", {"start": v(-2739.97, 2806.6) * mm, "end": v(-2763.33, 2876.02) * mm});
            skLineSegment(sketch, "E381", {"start": v(-2763.33, 2876.02) * mm, "end": v(-2806.84, 2965.36) * mm});
            skLineSegment(sketch, "E382", {"start": v(-2806.84, 2965.36) * mm, "end": v(-2841.41, 3026.34) * mm});
            skLineSegment(sketch, "E383", {"start": v(-2841.41, 3026.34) * mm, "end": v(-2857.26, 3054.33) * mm});
            skLineSegment(sketch, "E384", {"start": v(-2857.26, 3054.33) * mm, "end": v(-2871.13, 3075.9) * mm});
            skLineSegment(sketch, "E385", {"start": v(-2871.13, 3075.9) * mm, "end": v(-2901.43, 3122.81) * mm});
            skLineSegment(sketch, "E386", {"start": v(-2901.43, 3122.81) * mm, "end": v(-2914.92, 3140.49) * mm});
            skLineSegment(sketch, "E387", {"start": v(-2914.92, 3140.49) * mm, "end": v(-2944.46, 3179.02) * mm});
            skLineSegment(sketch, "E388", {"start": v(-2944.46, 3179.02) * mm, "end": v(-2959.2, 3195.48) * mm});
            skLineSegment(sketch, "E389", {"start": v(-2959.2, 3195.48) * mm, "end": v(-2991.45, 3231.3) * mm});
            skLineSegment(sketch, "E390", {"start": v(-2991.45, 3231.3) * mm, "end": v(-3007.53, 3246.53) * mm});
            skLineSegment(sketch, "E391", {"start": v(-3007.53, 3246.53) * mm, "end": v(-3042.7, 3279.66) * mm});
            skLineSegment(sketch, "E392", {"start": v(-3042.7, 3279.66) * mm, "end": v(-3060.24, 3293.63) * mm});
            skLineSegment(sketch, "E393", {"start": v(-3060.24, 3293.63) * mm, "end": v(-3098.54, 3324.08) * mm});
            skLineSegment(sketch, "E394", {"start": v(-3098.54, 3324.08) * mm, "end": v(-3115.76, 3336.04) * mm});
            skLineSegment(sketch, "E395", {"start": v(-3115.76, 3336.04) * mm, "end": v(-3153.3, 3362.15) * mm});
            skLineSegment(sketch, "E396", {"start": v(-3153.3, 3362.15) * mm, "end": v(-3153.3, 3362.16) * mm});
            skLineSegment(sketch, "E397", {"start": v(-3153.3, 3362.16) * mm, "end": v(-3168.46, 3371.38) * mm});
            skLineSegment(sketch, "E398", {"start": v(-3168.46, 3371.38) * mm, "end": v(-3201.38, 3391.52) * mm});
            skLineSegment(sketch, "E399", {"start": v(-3201.38, 3391.52) * mm, "end": v(-3218.68, 3401.04) * mm});
            skLineSegment(sketch, "E400", {"start": v(-3218.68, 3401.04) * mm, "end": v(-3256.17, 3421.87) * mm});
            skLineSegment(sketch, "E401", {"start": v(-3256.17, 3421.87) * mm, "end": v(-3279.82, 3434.75) * mm});
            skLineSegment(sketch, "E402", {"start": v(-3279.82, 3434.75) * mm, "end": v(-3331.13, 3462.9) * mm});
            skLineSegment(sketch, "E403", {"start": v(-3331.13, 3462.9) * mm, "end": v(-3354.95, 3475.8) * mm});
            skLineSegment(sketch, "E404", {"start": v(-3354.95, 3475.8) * mm, "end": v(-3406.74, 3503.96) * mm});
            skLineSegment(sketch, "E405", {"start": v(-3406.74, 3503.96) * mm, "end": v(-3406.74, 3503.96) * mm});
            skLineSegment(sketch, "E406", {"start": v(-3406.74, 3503.96) * mm, "end": v(-3424.62, 3513.56) * mm});
            skLineSegment(sketch, "E407", {"start": v(-3424.62, 3513.56) * mm, "end": v(-3463.56, 3534.5) * mm});
            skLineSegment(sketch, "E408", {"start": v(-3463.56, 3534.5) * mm, "end": v(-3472.93, 3541.94) * mm});
            skLineSegment(sketch, "E409", {"start": v(-3472.93, 3541.94) * mm, "end": v(-3493.28, 3558.12) * mm});
            skLineSegment(sketch, "E410", {"start": v(-3493.28, 3558.12) * mm, "end": v(-3489.37, 3572.11) * mm});
            skLineSegment(sketch, "E411", {"start": v(-3489.37, 3572.11) * mm, "end": v(-3489.37, 3572.11) * mm});
            skLineSegment(sketch, "E412", {"start": v(-3489.37, 3572.11) * mm, "end": v(-3487.56, 3578.54) * mm});
            skLineSegment(sketch, "E413", {"start": v(-3487.56, 3578.54) * mm, "end": v(-3467.37, 3584.43) * mm});
            skLineSegment(sketch, "E414", {"start": v(-3467.37, 3584.43) * mm, "end": v(-3467.37, 3584.43) * mm});
            skLineSegment(sketch, "E415", {"start": v(-3467.37, 3584.43) * mm, "end": v(-3458.1, 3587.12) * mm});
            skLineSegment(sketch, "E416", {"start": v(-3458.1, 3587.12) * mm, "end": v(-3429.6, 3579) * mm});
            skLineSegment(sketch, "E417", {"start": v(-3429.6, 3579) * mm, "end": v(-3416.52, 3575.26) * mm});
            skLineSegment(sketch, "E418", {"start": v(-3416.52, 3575.26) * mm, "end": v(-3381.52, 3558.2) * mm});
            skLineSegment(sketch, "E419", {"start": v(-3381.52, 3558.2) * mm, "end": v(-3365.44, 3550.37) * mm});
            skLineSegment(sketch, "E420", {"start": v(-3365.44, 3550.37) * mm, "end": v(-3325.69, 3529.46) * mm});
            skLineSegment(sketch, "E421", {"start": v(-3325.69, 3529.46) * mm, "end": v(-3307.43, 3519.86) * mm});
            skLineSegment(sketch, "E422", {"start": v(-3307.43, 3519.86) * mm, "end": v(-3270.04, 3510.24) * mm});
            skLineSegment(sketch, "E423", {"start": v(-3270.04, 3510.24) * mm, "end": v(-3252.9, 3505.82) * mm});
            skLineSegment(sketch, "E424", {"start": v(-3252.9, 3505.82) * mm, "end": v(-3240.1, 3513.51) * mm});
            skLineSegment(sketch, "E425", {"start": v(-3240.1, 3513.51) * mm, "end": v(-3212.2, 3530.3) * mm});
            skLineSegment(sketch, "E426", {"start": v(-3212.2, 3530.3) * mm, "end": v(-3189.34, 3558.98) * mm});
            skLineSegment(sketch, "E427", {"start": v(-3189.34, 3558.98) * mm, "end": v(-3178.85, 3572.14) * mm});
            skLineSegment(sketch, "E428", {"start": v(-3178.85, 3572.14) * mm, "end": v(-3156.58, 3598.17) * mm});
            skLineSegment(sketch, "E429", {"start": v(-3156.58, 3598.17) * mm, "end": v(-3146.37, 3610.14) * mm});
            skLineSegment(sketch, "E430", {"start": v(-3146.37, 3610.14) * mm, "end": v(-3127.27, 3625.3) * mm});
            skLineSegment(sketch, "E431", {"start": v(-3127.27, 3625.3) * mm, "end": v(-3127.27, 3625.3) * mm});
            skLineSegment(sketch, "E432", {"start": v(-3127.27, 3625.3) * mm, "end": v(-3118.5, 3632.28) * mm});
            skLineSegment(sketch, "E433", {"start": v(-3118.5, 3632.28) * mm, "end": v(-3105.2, 3628.37) * mm});
            skLineSegment(sketch, "E434", {"start": v(-3105.2, 3628.37) * mm, "end": v(-3105.2, 3628.37) * mm});
            skLineSegment(sketch, "E435", {"start": v(-3105.2, 3628.37) * mm, "end": v(-3105.19, 3628.37) * mm});
            skLineSegment(sketch, "E436", {"start": v(-3105.19, 3628.37) * mm, "end": v(-3105.19, 3628.37) * mm});
            skLineSegment(sketch, "E437", {"start": v(-3105.19, 3628.37) * mm, "end": v(-3099.1, 3626.57) * mm});
            skLineSegment(sketch, "E438", {"start": v(-3099.1, 3626.57) * mm, "end": v(-3099.1, 3626.57) * mm});
            skLineSegment(sketch, "E439", {"start": v(-3099.1, 3626.57) * mm, "end": v(-3094.58, 3610.21) * mm});
            skLineSegment(sketch, "E440", {"start": v(-3094.58, 3610.21) * mm, "end": v(-3094.58, 3610.21) * mm});
            skLineSegment(sketch, "E441", {"start": v(-3094.58, 3610.21) * mm, "end": v(-3094.58, 3610.2) * mm});
            skLineSegment(sketch, "E442", {"start": v(-3094.58, 3610.2) * mm, "end": v(-3094.58, 3610.2) * mm});
            skLineSegment(sketch, "E443", {"start": v(-3094.58, 3610.2) * mm, "end": v(-3092.44, 3602.74) * mm});
            skLineSegment(sketch, "E444", {"start": v(-3092.44, 3602.74) * mm, "end": v(-3095.54, 3592.63) * mm});
            skLineSegment(sketch, "E445", {"start": v(-3095.54, 3592.63) * mm, "end": v(-3102.86, 3570.51) * mm});
            skLineSegment(sketch, "E446", {"start": v(-3102.86, 3570.51) * mm, "end": v(-3106.84, 3557.56) * mm});
            skLineSegment(sketch, "E447", {"start": v(-3106.84, 3557.56) * mm, "end": v(-3115.99, 3529.24) * mm});
            skLineSegment(sketch, "E448", {"start": v(-3115.99, 3529.24) * mm, "end": v(-3116.42, 3513.2) * mm});
            skLineSegment(sketch, "E449", {"start": v(-3116.42, 3513.2) * mm, "end": v(-3117.44, 3478.28) * mm});
            skLineSegment(sketch, "E450", {"start": v(-3117.44, 3478.28) * mm, "end": v(-3104.48, 3443.05) * mm});
            skLineSegment(sketch, "E451", {"start": v(-3104.48, 3443.05) * mm, "end": v(-3098.59, 3426.87) * mm});
            skLineSegment(sketch, "E452", {"start": v(-3098.59, 3426.87) * mm, "end": v(-3065.85, 3397.64) * mm});
            skLineSegment(sketch, "E453", {"start": v(-3065.85, 3397.64) * mm, "end": v(-3065.85, 3397.64) * mm});
            skLineSegment(sketch, "E454", {"start": v(-3065.85, 3397.64) * mm, "end": v(-3050.89, 3384.2) * mm});
            skLineSegment(sketch, "E455", {"start": v(-3050.89, 3384.2) * mm, "end": v(-3009.82, 3356.62) * mm});
            skLineSegment(sketch, "E456", {"start": v(-3009.82, 3356.62) * mm, "end": v(-2991.02, 3343.94) * mm});
            skLineSegment(sketch, "E457", {"start": v(-2991.02, 3343.94) * mm, "end": v(-2953.05, 3313.67) * mm});
            skLineSegment(sketch, "E458", {"start": v(-2953.05, 3313.67) * mm, "end": v(-2935.67, 3299.75) * mm});
            skLineSegment(sketch, "E459", {"start": v(-2935.67, 3299.75) * mm, "end": v(-2900.6, 3266.78) * mm});
            skLineSegment(sketch, "E460", {"start": v(-2900.6, 3266.78) * mm, "end": v(-2884.57, 3251.61) * mm});
            skLineSegment(sketch, "E461", {"start": v(-2884.57, 3251.61) * mm, "end": v(-2852.23, 3215.95) * mm});
            skLineSegment(sketch, "E462", {"start": v(-2852.23, 3215.95) * mm, "end": v(-2837.45, 3199.57) * mm});
            skLineSegment(sketch, "E463", {"start": v(-2837.45, 3199.57) * mm, "end": v(-2803.34, 3157.79) * mm});
            skLineSegment(sketch, "E464", {"start": v(-2803.34, 3157.79) * mm, "end": v(-2787.72, 3138.6) * mm});
            skLineSegment(sketch, "E465", {"start": v(-2787.72, 3138.6) * mm, "end": v(-2747.33, 3087.35) * mm});
            skLineSegment(sketch, "E466", {"start": v(-2747.33, 3087.35) * mm, "end": v(-2728.87, 3063.8) * mm});
            skLineSegment(sketch, "E467", {"start": v(-2728.87, 3063.8) * mm, "end": v(-2687.82, 3017.38) * mm});
            skLineSegment(sketch, "E468", {"start": v(-2687.82, 3017.38) * mm, "end": v(-2669.02, 2996.06) * mm});
            skLineSegment(sketch, "E469", {"start": v(-2669.02, 2996.06) * mm, "end": v(-2632.9, 2968.81) * mm});
            skLineSegment(sketch, "E470", {"start": v(-2632.9, 2968.81) * mm, "end": v(-2616.34, 2956.29) * mm});
            skLineSegment(sketch, "E471", {"start": v(-2616.34, 2956.29) * mm, "end": v(-2582.66, 2949.07) * mm});
            skLineSegment(sketch, "E472", {"start": v(-2582.66, 2949.07) * mm, "end": v(-2567.2, 2945.77) * mm});
            skLineSegment(sketch, "E473", {"start": v(-2567.2, 2945.77) * mm, "end": v(-2533.41, 2959.51) * mm});
            skLineSegment(sketch, "E474", {"start": v(-2533.41, 2959.51) * mm, "end": v(-2533.41, 2959.51) * mm});
            skLineSegment(sketch, "E475", {"start": v(-2533.41, 2959.51) * mm, "end": v(-2517.92, 2965.81) * mm});
            skLineSegment(sketch, "E476", {"start": v(-2517.92, 2965.81) * mm, "end": v(-2482.94, 2992.23) * mm});
            skLineSegment(sketch, "E477", {"start": v(-2482.94, 2992.23) * mm, "end": v(-2466.87, 3004.35) * mm});
            skLineSegment(sketch, "E478", {"start": v(-2466.87, 3004.35) * mm, "end": v(-2429.58, 3035.18) * mm});
            skLineSegment(sketch, "E479", {"start": v(-2429.58, 3035.18) * mm, "end": v(-2412.46, 3049.3) * mm});
            skLineSegment(sketch, "E480", {"start": v(-2412.46, 3049.3) * mm, "end": v(-2397.93, 3062.84) * mm});
            skLineSegment(sketch, "E481", {"start": v(-2397.93, 3062.84) * mm, "end": v(-2366.23, 3092.33) * mm});
            skLineSegment(sketch, "E482", {"start": v(-2366.23, 3092.33) * mm, "end": v(-2357.9, 3102.6) * mm});
            skLineSegment(sketch, "E483", {"start": v(-2357.9, 3102.6) * mm, "end": v(-2339.74, 3125.02) * mm});
            skLineSegment(sketch, "E484", {"start": v(-2339.74, 3125.02) * mm, "end": v(-2339.74, 3125.02) * mm});
            skLineSegment(sketch, "E485", {"start": v(-2339.74, 3125.02) * mm, "end": v(-2335.35, 3134.4) * mm});
            skLineSegment(sketch, "E486", {"start": v(-2335.35, 3134.4) * mm, "end": v(-2325.75, 3154.79) * mm});
            skLineSegment(sketch, "E487", {"start": v(-2325.75, 3154.79) * mm, "end": v(-2322.95, 3165.53) * mm});
            skLineSegment(sketch, "E488", {"start": v(-2322.95, 3165.53) * mm, "end": v(-2316.93, 3188.93) * mm});
            skLineSegment(sketch, "E489", {"start": v(-2316.93, 3188.93) * mm, "end": v(-2316.93, 3188.93) * mm});
            skLineSegment(sketch, "E490", {"start": v(-2316.93, 3188.93) * mm, "end": v(-2315.28, 3199.82) * mm});
            skLineSegment(sketch, "E491", {"start": v(-2315.28, 3199.82) * mm, "end": v(-2311.73, 3223.52) * mm});
            skLineSegment(sketch, "E492", {"start": v(-2311.73, 3223.52) * mm, "end": v(-2311.73, 3223.52) * mm});
            skLineSegment(sketch, "E493", {"start": v(-2311.73, 3223.52) * mm, "end": v(-2310.7, 3233.3) * mm});
            skLineSegment(sketch, "E494", {"start": v(-2310.7, 3233.3) * mm, "end": v(-2308.55, 3254.59) * mm});
            skLineSegment(sketch, "E495", {"start": v(-2308.55, 3254.59) * mm, "end": v(-2306.31, 3261.98) * mm});
            skLineSegment(sketch, "E496", {"start": v(-2306.31, 3261.98) * mm, "end": v(-2301.41, 3278.08) * mm});
            skLineSegment(sketch, "E497", {"start": v(-2301.41, 3278.08) * mm, "end": v(-2289.73, 3286.16) * mm});
            skLineSegment(sketch, "E498", {"start": v(-2289.73, 3286.16) * mm, "end": v(-2289.73, 3286.16) * mm});
            skLineSegment(sketch, "E499", {"start": v(-2289.73, 3286.16) * mm, "end": v(-2289.72, 3286.16) * mm});
            skLineSegment(sketch, "E500", {"start": v(-2289.72, 3286.16) * mm, "end": v(-2284.34, 3289.9) * mm});
            skLineSegment(sketch, "E501", {"start": v(-2284.34, 3289.9) * mm, "end": v(-2271.97, 3288.11) * mm});
            skLineSegment(sketch, "E502", {"start": v(-2271.97, 3288.11) * mm, "end": v(-2271.97, 3288.11) * mm});
            skLineSegment(sketch, "E503", {"start": v(-2271.97, 3288.11) * mm, "end": v(-2266.28, 3287.3) * mm});
            skLineSegment(sketch, "E504", {"start": v(-2266.28, 3287.3) * mm, "end": v(-2259.32, 3273.79) * mm});
            skLineSegment(sketch, "E505", {"start": v(-2259.32, 3273.79) * mm, "end": v(-2256.12, 3267.57) * mm});
            skLineSegment(sketch, "E506", {"start": v(-2256.12, 3267.57) * mm, "end": v(-2250.91, 3248.74) * mm});
            skLineSegment(sketch, "E507", {"start": v(-2250.91, 3248.74) * mm, "end": v(-2248.53, 3240.08) * mm});
            skLineSegment(sketch, "E508", {"start": v(-2248.53, 3240.08) * mm, "end": v(-2241.39, 3222.35) * mm});
            skLineSegment(sketch, "E509", {"start": v(-2241.39, 3222.35) * mm, "end": v(-2238.14, 3214.2) * mm});
            skLineSegment(sketch, "E510", {"start": v(-2238.14, 3214.2) * mm, "end": v(-2238.14, 3214.2) * mm});
            skLineSegment(sketch, "E511", {"start": v(-2238.14, 3214.2) * mm, "end": v(-2231.4, 3210.47) * mm});
            skLineSegment(sketch, "E512", {"start": v(-2231.4, 3210.47) * mm, "end": v(-2216.7, 3202.39) * mm});
            skLineSegment(sketch, "E513", {"start": v(-2216.7, 3202.39) * mm, "end": v(-2216.7, 3202.39) * mm});
            skLineSegment(sketch, "E514", {"start": v(-2216.7, 3202.39) * mm, "end": v(-2203.92, 3207.04) * mm});
            skLineSegment(sketch, "E515", {"start": v(-2203.92, 3207.04) * mm, "end": v(-2176.01, 3217.17) * mm});
            skLineSegment(sketch, "E516", {"start": v(-2176.01, 3217.17) * mm, "end": v(-2176, 3217.17) * mm});
            skLineSegment(sketch, "E517", {"start": v(-2176, 3217.17) * mm, "end": v(-2157.19, 3228.68) * mm});
            skLineSegment(sketch, "E518", {"start": v(-2157.19, 3228.68) * mm, "end": v(-2116.07, 3253.77) * mm});
            skLineSegment(sketch, "E519", {"start": v(-2116.07, 3253.77) * mm, "end": v(-2091.23, 3270.66) * mm});
            skLineSegment(sketch, "E520", {"start": v(-2091.23, 3270.66) * mm, "end": v(-2036.92, 3307.5) * mm});
            skLineSegment(sketch, "E521", {"start": v(-2036.92, 3307.5) * mm, "end": v(-2015.91, 3320.88) * mm});
            skLineSegment(sketch, "E522", {"start": v(-2015.91, 3320.88) * mm, "end": v(-1970.07, 3350.06) * mm});
            skLineSegment(sketch, "E523", {"start": v(-1970.07, 3350.06) * mm, "end": v(-1970.07, 3350.06) * mm});
            skLineSegment(sketch, "E524", {"start": v(-1970.07, 3350.06) * mm, "end": v(-1970.06, 3350.06) * mm});
            skLineSegment(sketch, "E525", {"start": v(-1970.06, 3350.06) * mm, "end": v(-1962.83, 3351.08) * mm});
            skLineSegment(sketch, "E526", {"start": v(-1962.83, 3351.08) * mm, "end": v(-1962.83, 3351.08) * mm});
            skLineSegment(sketch, "E527", {"start": v(-1962.83, 3351.08) * mm, "end": v(-1947.05, 3353.3) * mm});
            skLineSegment(sketch, "E528", {"start": v(-1947.05, 3353.3) * mm, "end": v(-1947.05, 3353.29) * mm});
            skLineSegment(sketch, "E529", {"start": v(-1947.05, 3353.29) * mm, "end": v(-1946.45, 3343.38) * mm});
            skLineSegment(sketch, "E530", {"start": v(-1946.45, 3343.38) * mm, "end": v(-1946.45, 3343.38) * mm});
            skLineSegment(sketch, "E531", {"start": v(-1946.45, 3343.38) * mm, "end": v(-1946.14, 3338.84) * mm});
            skLineSegment(sketch, "E532", {"start": v(-1946.14, 3338.84) * mm, "end": v(-1946.14, 3338.84) * mm});
            skLineSegment(sketch, "E533", {"start": v(-1946.14, 3338.84) * mm, "end": v(-1945.84, 3331.7) * mm});
            skLineSegment(sketch, "E534", {"start": v(-1945.84, 3331.7) * mm, "end": v(-1945.84, 3331.7) * mm});
            skLineSegment(sketch, "E535", {"start": v(-1945.84, 3331.7) * mm, "end": v(-1945.68, 3328.4) * mm});
            skLineSegment(sketch, "E536", {"start": v(-1945.68, 3328.4) * mm, "end": v(-1958.79, 3312.65) * mm});
            skLineSegment(sketch, "E537", {"start": v(-1958.79, 3312.65) * mm, "end": v(-1964.8, 3305.41) * mm});
            skLineSegment(sketch, "E538", {"start": v(-1964.8, 3305.41) * mm, "end": v(-2004.43, 3269.72) * mm});
            skLineSegment(sketch, "E539", {"start": v(-2004.43, 3269.72) * mm, "end": v(-2022.7, 3253.32) * mm});
            skLineSegment(sketch, "E540", {"start": v(-2022.7, 3253.32) * mm, "end": v(-2071.39, 3212.02) * mm});
            skLineSegment(sketch, "E541", {"start": v(-2071.39, 3212.02) * mm, "end": v(-2093.77, 3193.04) * mm});
            skLineSegment(sketch, "E542", {"start": v(-2093.77, 3193.04) * mm, "end": v(-2134.02, 3160.5) * mm});
            skLineSegment(sketch, "E543", {"start": v(-2134.02, 3160.5) * mm, "end": v(-2152.39, 3145.57) * mm});
            skLineSegment(sketch, "E544", {"start": v(-2152.39, 3145.57) * mm, "end": v(-2182.84, 3122.63) * mm});
            skLineSegment(sketch, "E545", {"start": v(-2182.84, 3122.63) * mm, "end": v(-2196.66, 3112.06) * mm});
            skLineSegment(sketch, "E546", {"start": v(-2196.66, 3112.06) * mm, "end": v(-2215.89, 3099.6) * mm});
            skLineSegment(sketch, "E547", {"start": v(-2215.89, 3099.6) * mm, "end": v(-2224.63, 3093.75) * mm});
            skLineSegment(sketch, "E548", {"start": v(-2224.63, 3093.75) * mm, "end": v(-2240.83, 3083.85) * mm});
            skLineSegment(sketch, "E549", {"start": v(-2240.83, 3083.85) * mm, "end": v(-2248.23, 3079.15) * mm});
            skLineSegment(sketch, "E550", {"start": v(-2248.23, 3079.15) * mm, "end": v(-2269.63, 3063.88) * mm});
            skLineSegment(sketch, "E551", {"start": v(-2269.63, 3063.88) * mm, "end": v(-2279.44, 3056.72) * mm});
            skLineSegment(sketch, "E552", {"start": v(-2279.44, 3056.72) * mm, "end": v(-2306, 3034.85) * mm});
            skLineSegment(sketch, "E553", {"start": v(-2306, 3034.85) * mm, "end": v(-2306, 3034.85) * mm});
            skLineSegment(sketch, "E554", {"start": v(-2306, 3034.85) * mm, "end": v(-2318.2, 3024.7) * mm});
            skLineSegment(sketch, "E555", {"start": v(-2318.2, 3024.7) * mm, "end": v(-2349.85, 2995) * mm});
            skLineSegment(sketch, "E556", {"start": v(-2349.85, 2995) * mm, "end": v(-2349.85, 2995) * mm});
            skLineSegment(sketch, "E557", {"start": v(-2349.85, 2995) * mm, "end": v(-2364.38, 2981.28) * mm});
            skLineSegment(sketch, "E558", {"start": v(-2364.38, 2981.28) * mm, "end": v(-2400.67, 2942.8) * mm});
            skLineSegment(sketch, "E559", {"start": v(-2400.67, 2942.8) * mm, "end": v(-2400.67, 2942.8) * mm});
            skLineSegment(sketch, "E560", {"start": v(-2400.67, 2942.8) * mm, "end": v(-2417.31, 2925.17) * mm});
            skLineSegment(sketch, "E561", {"start": v(-2417.31, 2925.17) * mm, "end": v(-2457.82, 2876.99) * mm});
            skLineSegment(sketch, "E562", {"start": v(-2457.82, 2876.99) * mm, "end": v(-2476.42, 2855.17) * mm});
            skLineSegment(sketch, "E563", {"start": v(-2476.42, 2855.17) * mm, "end": v(-2515.07, 2806.2) * mm});
            skLineSegment(sketch, "E564", {"start": v(-2515.07, 2806.2) * mm, "end": v(-2532.83, 2784.05) * mm});
            skLineSegment(sketch, "E565", {"start": v(-2532.83, 2784.05) * mm, "end": v(-2563.61, 2743.28) * mm});
            skLineSegment(sketch, "E566", {"start": v(-2563.61, 2743.28) * mm, "end": v(-2577.74, 2724.7) * mm});
            skLineSegment(sketch, "E567", {"start": v(-2577.74, 2724.7) * mm, "end": v(-2602.9, 2687.81) * mm});
            skLineSegment(sketch, "E568", {"start": v(-2602.9, 2687.81) * mm, "end": v(-2614.47, 2670.87) * mm});
            skLineSegment(sketch, "E569", {"start": v(-2614.47, 2670.87) * mm, "end": v(-2636.28, 2633.5) * mm});
            skLineSegment(sketch, "E570", {"start": v(-2636.28, 2633.5) * mm, "end": v(-2636.28, 2633.5) * mm});
            skLineSegment(sketch, "E571", {"start": v(-2636.28, 2633.5) * mm, "end": v(-2646.3, 2616.36) * mm});
            skLineSegment(sketch, "E572", {"start": v(-2646.3, 2616.36) * mm, "end": v(-2672.96, 2564.54) * mm});
            skLineSegment(sketch, "E573", {"start": v(-2672.96, 2564.54) * mm, "end": v(-2694.22, 2518.7) * mm});
            skLineSegment(sketch, "E574", {"start": v(-2694.22, 2518.7) * mm, "end": v(-2711.26, 2479.4) * mm});
            skLineSegment(sketch, "E575", {"start": v(-2711.26, 2479.4) * mm, "end": v(-2725.26, 2447.15) * mm});
            skLineSegment(sketch, "E576", {"start": v(-2725.26, 2447.15) * mm, "end": v(-2738.11, 2409.38) * mm});
            skLineSegment(sketch, "E577", {"start": v(-2738.11, 2409.38) * mm, "end": v(-2751.8, 2353.5) * mm});
            skLineSegment(sketch, "E578", {"start": v(-2751.8, 2353.5) * mm, "end": v(-2762.98, 2296.24) * mm});
            skLineSegment(sketch, "E579", {"start": v(-2762.98, 2296.24) * mm, "end": v(-2768.34, 2254.38) * mm});
            skLineSegment(sketch, "E580", {"start": v(-2768.34, 2254.38) * mm, "end": v(-2770.93, 2218.04) * mm});
            skLineSegment(sketch, "E581", {"start": v(-2770.93, 2218.04) * mm, "end": v(-2773.82, 2177.47) * mm});
            skLineSegment(sketch, "E582", {"start": v(-2773.82, 2177.47) * mm, "end": v(-2771.9, 2135.16) * mm});
            skLineSegment(sketch, "E583", {"start": v(-2771.9, 2135.16) * mm, "end": v(-2759.98, 2093.6) * mm});
            skLineSegment(sketch, "E584", {"start": v(-2759.98, 2093.6) * mm, "end": v(-2737.5, 2058.25) * mm});
            skLineSegment(sketch, "E585", {"start": v(-2737.5, 2058.25) * mm, "end": v(-2703.87, 2034.55) * mm});
            skLineSegment(sketch, "E586", {"start": v(-2703.87, 2034.55) * mm, "end": v(-2652.16, 2015.83) * mm});
            skLineSegment(sketch, "E587", {"start": v(-2652.16, 2015.83) * mm, "end": v(-2575.5, 1995.46) * mm});
            skLineSegment(sketch, "E588", {"start": v(-2575.5, 1995.46) * mm, "end": v(-2486.7, 1985.63) * mm});
            skLineSegment(sketch, "E589", {"start": v(-2486.7, 1985.63) * mm, "end": v(-2398.64, 1998.56) * mm});
            skLineSegment(sketch, "E590", {"start": v(-2398.64, 1998.56) * mm, "end": v(-2323.3, 2023.96) * mm});
            skLineSegment(sketch, "E591", {"start": v(-2323.3, 2023.96) * mm, "end": v(-2272.73, 2051.54) * mm});
            skLineSegment(sketch, "E592", {"start": v(-2272.73, 2051.54) * mm, "end": v(-2253.33, 2069.83) * mm});
            skLineSegment(sketch, "E593", {"start": v(-2253.33, 2069.83) * mm, "end": v(-2244.41, 2078.2) * mm});
            skLineSegment(sketch, "E594", {"start": v(-2244.41, 2078.2) * mm, "end": v(-2244.41, 2078.2) * mm});
            skLineSegment(sketch, "E595", {"start": v(-2244.41, 2078.2) * mm, "end": v(-2238.52, 2093.76) * mm});
            skLineSegment(sketch, "E596", {"start": v(-2238.52, 2093.76) * mm, "end": v(-2238.52, 2093.76) * mm});
            skLineSegment(sketch, "E597", {"start": v(-2238.52, 2093.76) * mm, "end": v(-2235.83, 2100.9) * mm});
            skLineSegment(sketch, "E598", {"start": v(-2235.83, 2100.9) * mm, "end": v(-2239.84, 2116.08) * mm});
            skLineSegment(sketch, "E599", {"start": v(-2239.84, 2116.08) * mm, "end": v(-2239.84, 2116.08) * mm});
            skLineSegment(sketch, "E600", {"start": v(-2239.84, 2116.08) * mm, "end": v(-2241.7, 2123.04) * mm});
            skLineSegment(sketch, "E601", {"start": v(-2241.7, 2123.04) * mm, "end": v(-2241.7, 2123.04) * mm});
            skLineSegment(sketch, "E602", {"start": v(-2241.7, 2123.04) * mm, "end": v(-2252, 2140.21) * mm});
            skLineSegment(sketch, "E603", {"start": v(-2252, 2140.21) * mm, "end": v(-2252, 2140.21) * mm});
            skLineSegment(sketch, "E604", {"start": v(-2252, 2140.21) * mm, "end": v(-2256.73, 2148.09) * mm});
            skLineSegment(sketch, "E605", {"start": v(-2256.73, 2148.09) * mm, "end": v(-2269.28, 2166.22) * mm});
            skLineSegment(sketch, "E606", {"start": v(-2269.28, 2166.22) * mm, "end": v(-2269.28, 2166.22) * mm});
            skLineSegment(sketch, "E607", {"start": v(-2269.28, 2166.22) * mm, "end": v(-2275.02, 2174.55) * mm});
            skLineSegment(sketch, "E608", {"start": v(-2275.02, 2174.55) * mm, "end": v(-2285.71, 2192.69) * mm});
            skLineSegment(sketch, "E609", {"start": v(-2285.71, 2192.69) * mm, "end": v(-2290.62, 2201) * mm});
            skLineSegment(sketch, "E610", {"start": v(-2290.62, 2201) * mm, "end": v(-2301.1, 2239.25) * mm});
            skLineSegment(sketch, "E611", {"start": v(-2301.1, 2239.25) * mm, "end": v(-2304.13, 2301.07) * mm});
            skLineSegment(sketch, "E612", {"start": v(-2304.13, 2301.07) * mm, "end": v(-2300.11, 2359.7) * mm});
            skLineSegment(sketch, "E613", {"start": v(-2300.11, 2359.7) * mm, "end": v(-2289.52, 2388.2) * mm});
            skLineSegment(sketch, "E614", {"start": v(-2289.52, 2388.2) * mm, "end": v(-2289.52, 2388.2) * mm});
            skLineSegment(sketch, "E615", {"start": v(-2289.52, 2388.2) * mm, "end": v(-2279.49, 2383.47) * mm});
            skLineSegment(sketch, "E616", {"start": v(-2279.49, 2383.47) * mm, "end": v(-2279.49, 2383.47) * mm});
            skLineSegment(sketch, "E617", {"start": v(-2279.49, 2383.47) * mm, "end": v(-2274.92, 2381.3) * mm});
            skLineSegment(sketch, "E618", {"start": v(-2274.92, 2381.3) * mm, "end": v(-2263.9, 2348.64) * mm});
            skLineSegment(sketch, "E619", {"start": v(-2263.9, 2348.64) * mm, "end": v(-2258.84, 2333.68) * mm});
            skLineSegment(sketch, "E620", {"start": v(-2258.84, 2333.68) * mm, "end": v(-2247.66, 2293.1) * mm});
            skLineSegment(sketch, "E621", {"start": v(-2247.66, 2293.1) * mm, "end": v(-2242.56, 2274.5) * mm});
            skLineSegment(sketch, "E622", {"start": v(-2242.56, 2274.5) * mm, "end": v(-2232.07, 2245.95) * mm});
            skLineSegment(sketch, "E623", {"start": v(-2232.07, 2245.95) * mm, "end": v(-2227.27, 2232.87) * mm});
            skLineSegment(sketch, "E624", {"start": v(-2227.27, 2232.87) * mm, "end": v(-2210.83, 2202.5) * mm});
            skLineSegment(sketch, "E625", {"start": v(-2210.83, 2202.5) * mm, "end": v(-2191.05, 2177.04) * mm});
            skLineSegment(sketch, "E626", {"start": v(-2191.05, 2177.04) * mm, "end": v(-2166.18, 2158.27) * mm});
            skLineSegment(sketch, "E627", {"start": v(-2166.18, 2158.27) * mm, "end": v(-2134.53, 2147.9) * mm});
            skLineSegment(sketch, "E628", {"start": v(-2134.53, 2147.9) * mm, "end": v(-2097.88, 2148.75) * mm});
            skLineSegment(sketch, "E629", {"start": v(-2097.88, 2148.75) * mm, "end": v(-2057.98, 2163.5) * mm});
            skLineSegment(sketch, "E630", {"start": v(-2057.98, 2163.5) * mm, "end": v(-2025.29, 2188.73) * mm});
            skLineSegment(sketch, "E631", {"start": v(-2025.29, 2188.73) * mm, "end": v(-2010.3, 2200.28) * mm});
            skLineSegment(sketch, "E632", {"start": v(-2010.3, 2200.28) * mm, "end": v(-1969.15, 2246.18) * mm});
            skLineSegment(sketch, "E633", {"start": v(-1969.15, 2246.18) * mm, "end": v(-1950.28, 2267.21) * mm});
            skLineSegment(sketch, "E634", {"start": v(-1950.28, 2267.21) * mm, "end": v(-1930.52, 2294.19) * mm});
            skLineSegment(sketch, "E635", {"start": v(-1930.52, 2294.19) * mm, "end": v(-1887.47, 2352.99) * mm});
            skLineSegment(sketch, "E636", {"start": v(-1887.47, 2352.99) * mm, "end": v(-1869.84, 2382.32) * mm});
            skLineSegment(sketch, "E637", {"start": v(-1869.84, 2382.32) * mm, "end": v(-1831.38, 2446.23) * mm});
            skLineSegment(sketch, "E638", {"start": v(-1831.38, 2446.23) * mm, "end": v(-1799.73, 2503.56) * mm});
            skLineSegment(sketch, "E639", {"start": v(-1799.73, 2503.56) * mm, "end": v(-1785.18, 2529.9) * mm});
            skLineSegment(sketch, "E640", {"start": v(-1785.18, 2529.9) * mm, "end": v(-1762.47, 2568.91) * mm});
            skLineSegment(sketch, "E641", {"start": v(-1762.47, 2568.91) * mm, "end": v(-1752.03, 2586.85) * mm});
            skLineSegment(sketch, "E642", {"start": v(-1752.03, 2586.85) * mm, "end": v(-1736.03, 2617.1) * mm});
            skLineSegment(sketch, "E643", {"start": v(-1736.03, 2617.1) * mm, "end": v(-1728.7, 2631.02) * mm});
            skLineSegment(sketch, "E644", {"start": v(-1728.7, 2631.02) * mm, "end": v(-1711.93, 2676.33) * mm});
            skLineSegment(sketch, "E645", {"start": v(-1711.93, 2676.33) * mm, "end": v(-1702.07, 2720.7) * mm});
            skLineSegment(sketch, "E646", {"start": v(-1702.07, 2720.7) * mm, "end": v(-1699.56, 2761.98) * mm});
            skLineSegment(sketch, "E647", {"start": v(-1699.56, 2761.98) * mm, "end": v(-1703.24, 2801.37) * mm});
            skLineSegment(sketch, "E648", {"start": v(-1703.24, 2801.37) * mm, "end": v(-1712, 2840.16) * mm});
            skLineSegment(sketch, "E649", {"start": v(-1712, 2840.16) * mm, "end": v(-1717.26, 2870.54) * mm});
            skLineSegment(sketch, "E650", {"start": v(-1717.26, 2870.54) * mm, "end": v(-1710.4, 2884.81) * mm});
            skLineSegment(sketch, "E651", {"start": v(-1710.4, 2884.81) * mm, "end": v(-1693.94, 2877.7) * mm});
            skLineSegment(sketch, "E652", {"start": v(-1693.94, 2877.7) * mm, "end": v(-1670.4, 2843.94) * mm});
            skLineSegment(sketch, "E653", {"start": v(-1670.4, 2843.94) * mm, "end": v(-1647.84, 2798.68) * mm});
            skLineSegment(sketch, "E654", {"start": v(-1647.84, 2798.68) * mm, "end": v(-1634.33, 2757.08) * mm});
            skLineSegment(sketch, "E655", {"start": v(-1634.33, 2757.08) * mm, "end": v(-1625.26, 2719.28) * mm});
            skLineSegment(sketch, "E656", {"start": v(-1625.26, 2719.28) * mm, "end": v(-1625.26, 2719.28) * mm});
            skLineSegment(sketch, "E657", {"start": v(-1625.26, 2719.28) * mm, "end": v(-1615.91, 2685.5) * mm});
            skLineSegment(sketch, "E658", {"start": v(-1615.91, 2685.5) * mm, "end": v(-1602.45, 2669.17) * mm});
            skLineSegment(sketch, "E659", {"start": v(-1602.45, 2669.17) * mm, "end": v(-1602.45, 2669.17) * mm});
            skLineSegment(sketch, "E660", {"start": v(-1602.45, 2669.17) * mm, "end": v(-1596.28, 2661.67) * mm});
            skLineSegment(sketch, "E661", {"start": v(-1596.28, 2661.67) * mm, "end": v(-1568.9, 2656.26) * mm});
            skLineSegment(sketch, "E662", {"start": v(-1568.9, 2656.26) * mm, "end": v(-1556.33, 2653.7) * mm});
            skLineSegment(sketch, "E663", {"start": v(-1556.33, 2653.7) * mm, "end": v(-1539.26, 2655.58) * mm});
            skLineSegment(sketch, "E664", {"start": v(-1539.26, 2655.58) * mm, "end": v(-1502.05, 2659.8) * mm});
            skLineSegment(sketch, "E665", {"start": v(-1502.05, 2659.8) * mm, "end": v(-1482.34, 2665.56) * mm});
            skLineSegment(sketch, "E666", {"start": v(-1482.34, 2665.56) * mm, "end": v(-1439.41, 2678.16) * mm});
            skLineSegment(sketch, "E667", {"start": v(-1439.41, 2678.16) * mm, "end": v(-1419.04, 2688.04) * mm});
            skLineSegment(sketch, "E668", {"start": v(-1419.04, 2688.04) * mm, "end": v(-1374.74, 2709.58) * mm});
            skLineSegment(sketch, "E669", {"start": v(-1374.74, 2709.58) * mm, "end": v(-1355.74, 2723.88) * mm});
            skLineSegment(sketch, "E670", {"start": v(-1355.74, 2723.88) * mm, "end": v(-1314.44, 2754.9) * mm});
            skLineSegment(sketch, "E671", {"start": v(-1314.44, 2754.9) * mm, "end": v(-1300.17, 2766.63) * mm});
            skLineSegment(sketch, "E672", {"start": v(-1300.17, 2766.63) * mm, "end": v(-1269.2, 2791.98) * mm});
            skLineSegment(sketch, "E673", {"start": v(-1269.2, 2791.98) * mm, "end": v(-1269.2, 2791.98) * mm});
            skLineSegment(sketch, "E674", {"start": v(-1269.2, 2791.98) * mm, "end": v(-1263.09, 2794.13) * mm});
            skLineSegment(sketch, "E675", {"start": v(-1263.09, 2794.13) * mm, "end": v(-1249.8, 2798.7) * mm});
            skLineSegment(sketch, "E676", {"start": v(-1249.8, 2798.7) * mm, "end": v(-1245.5, 2793.2) * mm});
            skLineSegment(sketch, "E677", {"start": v(-1245.5, 2793.2) * mm, "end": v(-1245.5, 2793.2) * mm});
            skLineSegment(sketch, "E678", {"start": v(-1245.5, 2793.2) * mm, "end": v(-1243.53, 2790.68) * mm});
            skLineSegment(sketch, "E679", {"start": v(-1243.53, 2790.68) * mm, "end": v(-1243.53, 2790.68) * mm});
            skLineSegment(sketch, "E680", {"start": v(-1243.53, 2790.68) * mm, "end": v(-1243.52, 2790.68) * mm});
            skLineSegment(sketch, "E681", {"start": v(-1243.52, 2790.68) * mm, "end": v(-1241.7, 2788.42) * mm});
            skLineSegment(sketch, "E682", {"start": v(-1241.7, 2788.42) * mm, "end": v(-1241.7, 2788.42) * mm});
            skLineSegment(sketch, "E683", {"start": v(-1241.7, 2788.42) * mm, "end": v(-1237.73, 2783.54) * mm});
            skLineSegment(sketch, "E684", {"start": v(-1237.73, 2783.54) * mm, "end": v(-1241.3, 2776.48) * mm});
            skLineSegment(sketch, "E685", {"start": v(-1241.3, 2776.48) * mm, "end": v(-1249.04, 2761.22) * mm});
            skLineSegment(sketch, "E686", {"start": v(-1249.04, 2761.22) * mm, "end": v(-1279.82, 2724.59) * mm});
            skLineSegment(sketch, "E687", {"start": v(-1279.82, 2724.59) * mm, "end": v(-1294, 2707.72) * mm});
            skLineSegment(sketch, "E688", {"start": v(-1294, 2707.72) * mm, "end": v(-1337.66, 2666.35) * mm});
            skLineSegment(sketch, "E689", {"start": v(-1337.66, 2666.35) * mm, "end": v(-1357.75, 2647.32) * mm});
            skLineSegment(sketch, "E690", {"start": v(-1357.75, 2647.32) * mm, "end": v(-1404.08, 2617.86) * mm});
            skLineSegment(sketch, "E691", {"start": v(-1404.08, 2617.86) * mm, "end": v(-1425.36, 2604.3) * mm});
            skLineSegment(sketch, "E692", {"start": v(-1425.36, 2604.3) * mm, "end": v(-1471.5, 2584.86) * mm});
            skLineSegment(sketch, "E693", {"start": v(-1471.5, 2584.86) * mm, "end": v(-1492.72, 2575.87) * mm});
            skLineSegment(sketch, "E694", {"start": v(-1492.72, 2575.87) * mm, "end": v(-1535.76, 2564.62) * mm});
            skLineSegment(sketch, "E695", {"start": v(-1535.76, 2564.62) * mm, "end": v(-1555.67, 2559.26) * mm});
            skLineSegment(sketch, "E696", {"start": v(-1555.67, 2559.26) * mm, "end": v(-1592.47, 2550.1) * mm});
            skLineSegment(sketch, "E697", {"start": v(-1592.47, 2550.1) * mm, "end": v(-1609.46, 2545.75) * mm});
            skLineSegment(sketch, "E698", {"start": v(-1609.46, 2545.75) * mm, "end": v(-1636.84, 2532.6) * mm});
            skLineSegment(sketch, "E699", {"start": v(-1636.84, 2532.6) * mm, "end": v(-1649.34, 2526.65) * mm});
            skLineSegment(sketch, "E700", {"start": v(-1649.34, 2526.65) * mm, "end": v(-1672.7, 2509.12) * mm});
            skLineSegment(sketch, "E701", {"start": v(-1672.7, 2509.12) * mm, "end": v(-1672.7, 2509.12) * mm});
            skLineSegment(sketch, "E702", {"start": v(-1672.7, 2509.12) * mm, "end": v(-1683.33, 2501.25) * mm});
            skLineSegment(sketch, "E703", {"start": v(-1683.33, 2501.25) * mm, "end": v(-1708.07, 2479) * mm});
            skLineSegment(sketch, "E704", {"start": v(-1708.07, 2479) * mm, "end": v(-1719.4, 2468.86) * mm});
            skLineSegment(sketch, "E705", {"start": v(-1719.4, 2468.86) * mm, "end": v(-1745.45, 2438.26) * mm});
            skLineSegment(sketch, "E706", {"start": v(-1745.45, 2438.26) * mm, "end": v(-1757.42, 2424.2) * mm});
            skLineSegment(sketch, "E707", {"start": v(-1757.42, 2424.2) * mm, "end": v(-1784.72, 2381.54) * mm});
            skLineSegment(sketch, "E708", {"start": v(-1784.72, 2381.54) * mm, "end": v(-1797.27, 2361.95) * mm});
            skLineSegment(sketch, "E709", {"start": v(-1797.27, 2361.95) * mm, "end": v(-1821.88, 2311.23) * mm});
            skLineSegment(sketch, "E710", {"start": v(-1821.88, 2311.23) * mm, "end": v(-1833.19, 2287.94) * mm});
            skLineSegment(sketch, "E711", {"start": v(-1833.19, 2287.94) * mm, "end": v(-1851.17, 2233.1) * mm});
            skLineSegment(sketch, "E712", {"start": v(-1851.17, 2233.1) * mm, "end": v(-1859.4, 2207.9) * mm});
            skLineSegment(sketch, "E713", {"start": v(-1859.4, 2207.9) * mm, "end": v(-1867.6, 2157.86) * mm});
            skLineSegment(sketch, "E714", {"start": v(-1867.6, 2157.86) * mm, "end": v(-1867.6, 2157.86) * mm});
            skLineSegment(sketch, "E715", {"start": v(-1867.6, 2157.86) * mm, "end": v(-1871.36, 2134.9) * mm});
            skLineSegment(sketch, "E716", {"start": v(-1871.36, 2134.9) * mm, "end": v(-1866.64, 2098.58) * mm});
            skLineSegment(sketch, "E717", {"start": v(-1866.64, 2098.58) * mm, "end": v(-1866.64, 2098.58) * mm});
            skLineSegment(sketch, "E718", {"start": v(-1866.64, 2098.58) * mm, "end": v(-1864.48, 2081.9) * mm});
            skLineSegment(sketch, "E719", {"start": v(-1864.48, 2081.9) * mm, "end": v(-1845.78, 2054.3) * mm});
            skLineSegment(sketch, "E720", {"start": v(-1845.78, 2054.3) * mm, "end": v(-1837.2, 2041.66) * mm});
            skLineSegment(sketch, "E721", {"start": v(-1837.2, 2041.66) * mm, "end": v(-1803.44, 2017.8) * mm});
            skLineSegment(sketch, "E722", {"start": v(-1803.44, 2017.8) * mm, "end": v(-1787.95, 2006.89) * mm});
            skLineSegment(sketch, "E723", {"start": v(-1787.95, 2006.89) * mm, "end": v(-1740.1, 1991.98) * mm});
            skLineSegment(sketch, "E724", {"start": v(-1740.1, 1991.98) * mm, "end": v(-1718.15, 1985.12) * mm});
            skLineSegment(sketch, "E725", {"start": v(-1718.15, 1985.12) * mm, "end": v(-1657.19, 1984.33) * mm});
            skLineSegment(sketch, "E726", {"start": v(-1657.19, 1984.33) * mm, "end": v(-1629.17, 1983.95) * mm});
            skLineSegment(sketch, "E727", {"start": v(-1629.17, 1983.95) * mm, "end": v(-1567.35, 1992.2) * mm});
            skLineSegment(sketch, "E728", {"start": v(-1567.35, 1992.2) * mm, "end": v(-1538.95, 1995.97) * mm});
            skLineSegment(sketch, "E729", {"start": v(-1538.95, 1995.97) * mm, "end": v(-1488.51, 2008.16) * mm});
            skLineSegment(sketch, "E730", {"start": v(-1488.51, 2008.16) * mm, "end": v(-1465.32, 2013.75) * mm});
            skLineSegment(sketch, "E731", {"start": v(-1465.32, 2013.75) * mm, "end": v(-1416.25, 2023.14) * mm});
            skLineSegment(sketch, "E732", {"start": v(-1416.25, 2023.14) * mm, "end": v(-1399.71, 2010.04) * mm});
            skLineSegment(sketch, "E733", {"start": v(-1399.71, 2010.04) * mm, "end": v(-1412.33, 1991.6) * mm});
            skLineSegment(sketch, "E734", {"start": v(-1412.33, 1991.6) * mm, "end": v(-1418.15, 1983.11) * mm});
            skLineSegment(sketch, "E735", {"start": v(-1418.15, 1983.11) * mm, "end": v(-1456.43, 1961.14) * mm});
            skLineSegment(sketch, "E736", {"start": v(-1456.43, 1961.14) * mm, "end": v(-1474, 1951.06) * mm});
            skLineSegment(sketch, "E737", {"start": v(-1474, 1951.06) * mm, "end": v(-1532.15, 1931.96) * mm});
            skLineSegment(sketch, "E738", {"start": v(-1532.15, 1931.96) * mm, "end": v(-1558.87, 1923.2) * mm});
            skLineSegment(sketch, "E739", {"start": v(-1558.87, 1923.2) * mm, "end": v(-1631.1, 1913.42) * mm});
            skLineSegment(sketch, "E740", {"start": v(-1631.1, 1913.42) * mm, "end": v(-1664.28, 1908.9) * mm});
            skLineSegment(sketch, "E741", {"start": v(-1664.28, 1908.9) * mm, "end": v(-1768.09, 1910.09) * mm});
            skLineSegment(sketch, "E742", {"start": v(-1768.09, 1910.09) * mm, "end": v(-1848.17, 1928.63) * mm});
            skLineSegment(sketch, "E743", {"start": v(-1848.17, 1928.63) * mm, "end": v(-1912.94, 1954.08) * mm});
            skLineSegment(sketch, "E744", {"start": v(-1912.94, 1954.08) * mm, "end": v(-1970.78, 1975.85) * mm});
            skLineSegment(sketch, "E745", {"start": v(-1970.78, 1975.85) * mm, "end": v(-2026.66, 1986.54) * mm});
            skLineSegment(sketch, "E746", {"start": v(-2026.66, 1986.54) * mm, "end": v(-2085.48, 1978.77) * mm});
            skLineSegment(sketch, "E747", {"start": v(-2085.48, 1978.77) * mm, "end": v(-2146.09, 1959.64) * mm});
            skLineSegment(sketch, "E748", {"start": v(-2146.09, 1959.64) * mm, "end": v(-2207.33, 1936.38) * mm});
            skLineSegment(sketch, "E749", {"start": v(-2207.33, 1936.38) * mm, "end": v(-2278.37, 1909.7) * mm});
            skLineSegment(sketch, "E750", {"start": v(-2278.37, 1909.7) * mm, "end": v(-2368.39, 1880.4) * mm});
            skLineSegment(sketch, "E751", {"start": v(-2368.39, 1880.4) * mm, "end": v(-2468.77, 1856.24) * mm});
            skLineSegment(sketch, "E752", {"start": v(-2468.77, 1856.24) * mm, "end": v(-2570.9, 1844.96) * mm});
            skLineSegment(sketch, "E753", {"start": v(-2570.9, 1844.96) * mm, "end": v(-2661.5, 1838.56) * mm});
            skLineSegment(sketch, "E754", {"start": v(-2661.5, 1838.56) * mm, "end": v(-2727.37, 1829.04) * mm});
            skLineSegment(sketch, "E755", {"start": v(-2727.37, 1829.04) * mm, "end": v(-2780.8, 1814.91) * mm});
            skLineSegment(sketch, "E756", {"start": v(-2780.8, 1814.91) * mm, "end": v(-2834.28, 1794.62) * mm});
            skLineSegment(sketch, "E757", {"start": v(-2834.28, 1794.62) * mm, "end": v(-2884.14, 1768.25) * mm});
            skLineSegment(sketch, "E758", {"start": v(-2884.14, 1768.25) * mm, "end": v(-2926.8, 1735.82) * mm});
            skLineSegment(sketch, "E759", {"start": v(-2926.8, 1735.82) * mm, "end": v(-2966.03, 1696.47) * mm});
            skLineSegment(sketch, "E760", {"start": v(-2966.03, 1696.47) * mm, "end": v(-3005.55, 1649.26) * mm});
            skLineSegment(sketch, "E761", {"start": v(-3005.55, 1649.26) * mm, "end": v(-3039.1, 1588.83) * mm});
            skLineSegment(sketch, "E762", {"start": v(-3039.1, 1588.83) * mm, "end": v(-3060.36, 1509.8) * mm});
            skLineSegment(sketch, "E763", {"start": v(-3060.36, 1509.8) * mm, "end": v(-3071.46, 1386.95) * mm});
            skLineSegment(sketch, "E764", {"start": v(-3071.46, 1386.95) * mm, "end": v(-3074.56, 1195.08) * mm});
            skLineSegment(sketch, "E765", {"start": v(-3074.56, 1195.08) * mm, "end": v(-3073.85, 1022.74) * mm});
            skLineSegment(sketch, "E766", {"start": v(-3073.85, 1022.74) * mm, "end": v(-3073.57, 958.45) * mm});
            skLineSegment(sketch, "E767", {"start": v(-3073.57, 958.45) * mm, "end": v(-3073.57, 958.45) * mm});
            skLineSegment(sketch, "E768", {"start": v(-3073.57, 958.45) * mm, "end": v(-3073.5, 948.8) * mm});
            skLineSegment(sketch, "E769", {"start": v(-3073.5, 948.8) * mm, "end": v(-3073.5, 948.8) * mm});
            skLineSegment(sketch, "E770", {"start": v(-3073.5, 948.8) * mm, "end": v(-3073.42, 940.42) * mm});
            skLineSegment(sketch, "E771", {"start": v(-3073.42, 940.42) * mm, "end": v(-3072.94, 906.86) * mm});
            skLineSegment(sketch, "E772", {"start": v(-3072.94, 906.86) * mm, "end": v(-3071.61, 821.77) * mm});
            skLineSegment(sketch, "E773", {"start": v(-3071.61, 821.77) * mm, "end": v(-3065.42, 713.65) * mm});
            skLineSegment(sketch, "E774", {"start": v(-3065.42, 713.65) * mm, "end": v(-3050.35, 611.08) * mm});
            skLineSegment(sketch, "E775", {"start": v(-3050.35, 611.08) * mm, "end": v(-3028, 521.85) * mm});
            skLineSegment(sketch, "E776", {"start": v(-3028, 521.85) * mm, "end": v(-3008.85, 475.11) * mm});
            skLineSegment(sketch, "E777", {"start": v(-3008.85, 475.11) * mm, "end": v(-3000.04, 453.68) * mm});
            skLineSegment(sketch, "E778", {"start": v(-3000.04, 453.68) * mm, "end": v(-2973.4, 417.23) * mm});
            skLineSegment(sketch, "E779", {"start": v(-2973.4, 417.23) * mm, "end": v(-2961.18, 400.51) * mm});
            skLineSegment(sketch, "E780", {"start": v(-2961.18, 400.51) * mm, "end": v(-2906.08, 356.3) * mm});
            skLineSegment(sketch, "E781", {"start": v(-2906.08, 356.3) * mm, "end": v(-2837.15, 320.58) * mm});
            skLineSegment(sketch, "E782", {"start": v(-2837.15, 320.58) * mm, "end": v(-2756.73, 292.95) * mm});
            skLineSegment(sketch, "E783", {"start": v(-2756.73, 292.95) * mm, "end": v(-2669.58, 272.6) * mm});
            skLineSegment(sketch, "E784", {"start": v(-2669.58, 272.6) * mm, "end": v(-2580.48, 258.8) * mm});
            skLineSegment(sketch, "E785", {"start": v(-2580.48, 258.8) * mm, "end": v(-2501.44, 241.13) * mm});
            skLineSegment(sketch, "E786", {"start": v(-2501.44, 241.13) * mm, "end": v(-2444.49, 209.18) * mm});
            skLineSegment(sketch, "E787", {"start": v(-2444.49, 209.18) * mm, "end": v(-2406.98, 169.76) * mm});
            skLineSegment(sketch, "E788", {"start": v(-2406.98, 169.76) * mm, "end": v(-2386.27, 129.65) * mm});
            skLineSegment(sketch, "E789", {"start": v(-2386.27, 129.65) * mm, "end": v(-2377.1, 97.11) * mm});
            skLineSegment(sketch, "E790", {"start": v(-2377.1, 97.11) * mm, "end": v(-2377.1, 97.11) * mm});
            skLineSegment(sketch, "E791", {"start": v(-2377.1, 97.11) * mm, "end": v(-2374.26, 80.42) * mm});
            skLineSegment(sketch, "E792", {"start": v(-2374.26, 80.42) * mm, "end": v(-2386.35, 73.87) * mm});
            skLineSegment(sketch, "E793", {"start": v(-2386.35, 73.87) * mm, "end": v(-2421.93, 71.66) * mm});
            skLineSegment(sketch, "E794", {"start": v(-2421.93, 71.66) * mm, "end": v(-3271, 71.66) * mm});
            skLineSegment(sketch, "E795", {"start": v(-3271, 71.66) * mm, "end": v(-3271, 71.66) * mm});
            skLineSegment(sketch, "E796", {"start": v(-3271, 71.66) * mm, "end": v(-3278.12, 75.52) * mm});
            skLineSegment(sketch, "E797", {"start": v(-3278.12, 75.52) * mm, "end": v(-3278.12, 75.52) * mm});
            skLineSegment(sketch, "E798", {"start": v(-3278.12, 75.52) * mm, "end": v(-3280.5, 87.1) * mm});
            skLineSegment(sketch, "E799", {"start": v(-3280.5, 87.1) * mm, "end": v(-3280.6, 139.96) * mm});
            skLineSegment(sketch, "E800", {"start": v(-3280.6, 139.96) * mm, "end": v(-3280.88, 267.75) * mm});
            skLineSegment(sketch, "E801", {"start": v(-3280.88, 267.75) * mm, "end": v(-3281.3, 427.31) * mm});
            skLineSegment(sketch, "E802", {"start": v(-3281.3, 427.31) * mm, "end": v(-3281.82, 575.55) * mm});
            skLineSegment(sketch, "E803", {"start": v(-3281.82, 575.55) * mm, "end": v(-3282.4, 709.18) * mm});
            skLineSegment(sketch, "E804", {"start": v(-3282.4, 709.18) * mm, "end": v(-3282.84, 788.5) * mm});
            skLineSegment(sketch, "E805", {"start": v(-3282.84, 788.5) * mm, "end": v(-3283.04, 824.9) * mm});
            skLineSegment(sketch, "E806", {"start": v(-3283.04, 824.9) * mm, "end": v(-3283.37, 881.1) * mm});
            skLineSegment(sketch, "E807", {"start": v(-3283.37, 881.1) * mm, "end": v(-3283.53, 906.91) * mm});
            skLineSegment(sketch, "E808", {"start": v(-3283.53, 906.91) * mm, "end": v(-3283.7, 939.33) * mm});
            skLineSegment(sketch, "E809", {"start": v(-3283.7, 939.33) * mm, "end": v(-3283.7, 939.33) * mm});
            skLineSegment(sketch, "E810", {"start": v(-3283.7, 939.33) * mm, "end": v(-3288.3, 945.3) * mm});
            skLineSegment(sketch, "E811", {"start": v(-3288.3, 945.3) * mm, "end": v(-3302.02, 947.96) * mm});
            skLineSegment(sketch, "E812", {"start": v(-3302.02, 947.96) * mm, "end": v(-3320.33, 948.47) * mm});
            skLineSegment(sketch, "E813", {"start": v(-3320.33, 948.47) * mm, "end": v(-3338.62, 947.96) * mm});
            skLineSegment(sketch, "E814", {"start": v(-3338.62, 947.96) * mm, "end": v(-3352.36, 944.99) * mm});
            skLineSegment(sketch, "E815", {"start": v(-3352.36, 944.99) * mm, "end": v(-3356.93, 938.1) * mm});
            skLineSegment(sketch, "E816", {"start": v(-3356.93, 938.1) * mm, "end": v(-3357.14, 905.09) * mm});
            skLineSegment(sketch, "E817", {"start": v(-3357.14, 905.09) * mm, "end": v(-3357.62, 823.7) * mm});
            skLineSegment(sketch, "E818", {"start": v(-3357.62, 823.7) * mm, "end": v(-3358.23, 708.87) * mm});
            skLineSegment(sketch, "E819", {"start": v(-3358.23, 708.87) * mm, "end": v(-3358.84, 575.55) * mm});
            skLineSegment(sketch, "E820", {"start": v(-3358.84, 575.55) * mm, "end": v(-3359.35, 426.83) * mm});
            skLineSegment(sketch, "E821", {"start": v(-3359.35, 426.83) * mm, "end": v(-3359.78, 265.84) * mm});
            skLineSegment(sketch, "E822", {"start": v(-3359.78, 265.84) * mm, "end": v(-3360.06, 137.12) * mm});
            skLineSegment(sketch, "E823", {"start": v(-3360.06, 137.12) * mm, "end": v(-3360.16, 85.2) * mm});
            skLineSegment(sketch, "E824", {"start": v(-3360.16, 85.2) * mm, "end": v(-3362.29, 75.06) * mm});
            skLineSegment(sketch, "E825", {"start": v(-3362.29, 75.06) * mm, "end": v(-3368.64, 71.66) * mm});
            skLineSegment(sketch, "E826", {"start": v(-3368.64, 71.66) * mm, "end": v(-4219.16, 71.66) * mm});
            skLineSegment(sketch, "E827", {"start": v(-4219.16, 71.66) * mm, "end": v(-4254.75, 73.8) * mm});
            skLineSegment(sketch, "E828", {"start": v(-4254.75, 73.8) * mm, "end": v(-4266.81, 80.14) * mm});
            skLineSegment(sketch, "E829", {"start": v(-4266.81, 80.14) * mm, "end": v(-4262.3, 96.45) * mm});
            skLineSegment(sketch, "E830", {"start": v(-4262.3, 96.45) * mm, "end": v(-4248.14, 128.4) * mm});
            skLineSegment(sketch, "E831", {"start": v(-4248.14, 128.4) * mm, "end": v(-4222.44, 168) * mm});
            skLineSegment(sketch, "E832", {"start": v(-4222.44, 168) * mm, "end": v(-4183.27, 207.27) * mm});
            skLineSegment(sketch, "E833", {"start": v(-4183.27, 207.27) * mm, "end": v(-4127.97, 239.45) * mm});
            skLineSegment(sketch, "E834", {"start": v(-4127.97, 239.45) * mm, "end": v(-4053.93, 257.84) * mm});
            skLineSegment(sketch, "E835", {"start": v(-4053.93, 257.84) * mm, "end": v(-3969.76, 272.37) * mm});
            skLineSegment(sketch, "E836", {"start": v(-3969.76, 272.37) * mm, "end": v(-3884.06, 292.95) * mm});
            skLineSegment(sketch, "E837", {"start": v(-3884.06, 292.95) * mm, "end": v(-3803.41, 320.58) * mm});
            skLineSegment(sketch, "E838", {"start": v(-3803.41, 320.58) * mm, "end": v(-3756.12, 345.07) * mm});
            skLineSegment(sketch, "E839", {"start": v(-3756.12, 345.07) * mm, "end": v(-3734.43, 356.3) * mm});
            skLineSegment(sketch, "E840", {"start": v(-3734.43, 356.3) * mm, "end": v(-3696.66, 386.6) * mm});
            skLineSegment(sketch, "E841", {"start": v(-3696.66, 386.6) * mm, "end": v(-3679.33, 400.51) * mm});
            skLineSegment(sketch, "E842", {"start": v(-3679.33, 400.51) * mm, "end": v(-3640.47, 453.68) * mm});
            skLineSegment(sketch, "E843", {"start": v(-3640.47, 453.68) * mm, "end": v(-3612.5, 521.85) * mm});
            skLineSegment(sketch, "E844", {"start": v(-3612.5, 521.85) * mm, "end": v(-3590.16, 611.08) * mm});
            skLineSegment(sketch, "E845", {"start": v(-3590.16, 611.08) * mm, "end": v(-3575.1, 713.34) * mm});
            skLineSegment(sketch, "E846", {"start": v(-3575.1, 713.34) * mm, "end": v(-3568.9, 820.53) * mm});
            skLineSegment(sketch, "E847", {"start": v(-3568.9, 820.53) * mm, "end": v(-3567.57, 905) * mm});
            skLineSegment(sketch, "E848", {"start": v(-3567.57, 905) * mm, "end": v(-3567.1, 939.17) * mm});
            skLineSegment(sketch, "E849", {"start": v(-3567.1, 939.17) * mm, "end": v(-3567.1, 947.94) * mm});
            skLineSegment(sketch, "E850", {"start": v(-3567.1, 947.94) * mm, "end": v(-3567.1, 947.94) * mm});
            skLineSegment(sketch, "E851", {"start": v(-3567.1, 947.94) * mm, "end": v(-3567.2, 953.6) * mm});
            skLineSegment(sketch, "E852", {"start": v(-3567.2, 953.6) * mm, "end": v(-3567.2, 953.6) * mm});
            skLineSegment(sketch, "E853", {"start": v(-3567.2, 953.6) * mm, "end": v(-3567.24, 956.22) * mm});
            skLineSegment(sketch, "E854", {"start": v(-3567.24, 956.22) * mm, "end": v(-3568, 1012.55) * mm});
            skLineSegment(sketch, "E855", {"start": v(-3568, 1012.55) * mm, "end": v(-3569.86, 1165.51) * mm});
            skLineSegment(sketch, "E856", {"start": v(-3569.86, 1165.51) * mm, "end": v(-3576.34, 1336.23) * mm});
            skLineSegment(sketch, "E857", {"start": v(-3576.34, 1336.23) * mm, "end": v(-3591, 1445.88) * mm});
            skLineSegment(sketch, "E858", {"start": v(-3591, 1445.88) * mm, "end": v(-3617.94, 1514.46) * mm});
            skLineSegment(sketch, "E859", {"start": v(-3617.94, 1514.46) * mm, "end": v(-3661.28, 1562.03) * mm});
            skLineSegment(sketch, "E860", {"start": v(-3661.28, 1562.03) * mm, "end": v(-3714.1, 1596.17) * mm});
            skLineSegment(sketch, "E861", {"start": v(-3714.1, 1596.17) * mm, "end": v(-3769.45, 1624.54) * mm});
            skLineSegment(sketch, "E862", {"start": v(-3769.45, 1624.54) * mm, "end": v(-3831.46, 1647.02) * mm});
            skLineSegment(sketch, "E863", {"start": v(-3831.46, 1647.02) * mm, "end": v(-3904.25, 1663.58) * mm});
            skLineSegment(sketch, "E864", {"start": v(-3904.25, 1663.58) * mm, "end": v(-3958.79, 1669.2) * mm});
            skLineSegment(sketch, "E865", {"start": v(-3958.79, 1669.2) * mm, "end": v(-3983.8, 1671.76) * mm});
            skLineSegment(sketch, "E866", {"start": v(-3983.8, 1671.76) * mm, "end": v(-4040.22, 1669.96) * mm});
            skLineSegment(sketch, "E867", {"start": v(-4040.22, 1669.96) * mm, "end": v(-4066.1, 1669.14) * mm});
            skLineSegment(sketch, "E868", {"start": v(-4066.1, 1669.14) * mm, "end": v(-4154.34, 1663.66) * mm});
            skLineSegment(sketch, "E869", {"start": v(-4154.34, 1663.66) * mm, "end": v(-4251.8, 1663.23) * mm});
            skLineSegment(sketch, "E870", {"start": v(-4251.8, 1663.23) * mm, "end": v(-4343.3, 1666.45) * mm});
            skLineSegment(sketch, "E871", {"start": v(-4343.3, 1666.45) * mm, "end": v(-4391.55, 1670.18) * mm});
            skLineSegment(sketch, "E872", {"start": v(-4391.55, 1670.18) * mm, "end": v(-4413.7, 1671.91) * mm});
            skLineSegment(sketch, "E873", {"start": v(-4413.7, 1671.91) * mm, "end": v(-4473.9, 1679.23) * mm});
            skLineSegment(sketch, "E874", {"start": v(-4473.9, 1679.23) * mm, "end": v(-4534.68, 1688.12) * mm});
            skLineSegment(sketch, "E875", {"start": v(-4534.68, 1688.12) * mm, "end": v(-4593.99, 1698.63) * mm});
            skLineSegment(sketch, "E876", {"start": v(-4593.99, 1698.63) * mm, "end": v(-4649.61, 1710.9) * mm});
            skLineSegment(sketch, "E877", {"start": v(-4649.61, 1710.9) * mm, "end": v(-4706.23, 1727.33) * mm});
            skLineSegment(sketch, "E878", {"start": v(-4706.23, 1727.33) * mm, "end": v(-4768.36, 1750.37) * mm});
            skLineSegment(sketch, "E879", {"start": v(-4768.36, 1750.37) * mm, "end": v(-4830.97, 1778.92) * mm});
            skLineSegment(sketch, "E880", {"start": v(-4830.97, 1778.92) * mm, "end": v(-4889.06, 1811.9) * mm});
            skLineSegment(sketch, "E881", {"start": v(-4889.06, 1811.9) * mm, "end": v(-4939.76, 1840.06) * mm});
            skLineSegment(sketch, "E882", {"start": v(-4939.76, 1840.06) * mm, "end": v(-4980.25, 1854.2) * mm});
            skLineSegment(sketch, "E883", {"start": v(-4980.25, 1854.2) * mm, "end": v(-5022.92, 1857.61) * mm});
            skLineSegment(sketch, "E884", {"start": v(-5022.92, 1857.61) * mm, "end": v(-5080.2, 1853.65) * mm});
            skLineSegment(sketch, "E885", {"start": v(-5080.2, 1853.65) * mm, "end": v(-5147.89, 1848.77) * mm});
            skLineSegment(sketch, "E886", {"start": v(-5147.89, 1848.77) * mm, "end": v(-5221.85, 1849.43) * mm});
            skLineSegment(sketch, "E887", {"start": v(-5221.85, 1849.43) * mm, "end": v(-5297.87, 1859.97) * mm});
            skLineSegment(sketch, "E888", {"start": v(-5297.87, 1859.97) * mm, "end": v(-5371.81, 1884.69) * mm});
            skLineSegment(sketch, "E889", {"start": v(-5371.81, 1884.69) * mm, "end": v(-5425.1, 1913.54) * mm});
            skLineSegment(sketch, "E890", {"start": v(-5425.1, 1913.54) * mm, "end": v(-5439.15, 1936.53) * mm});
            skLineSegment(sketch, "E891", {"start": v(-1446.17, 199.26) * mm, "end": v(-1442.26, 213.82) * mm});
            skLineSegment(sketch, "E892", {"start": v(-1442.26, 213.82) * mm, "end": v(-1429.94, 240.51) * mm});
            skLineSegment(sketch, "E893", {"start": v(-1429.94, 240.51) * mm, "end": v(-1416.94, 266.3) * mm});
            skLineSegment(sketch, "E894", {"start": v(-1416.94, 266.3) * mm, "end": v(-1410.97, 278.13) * mm});
            skLineSegment(sketch, "E895", {"start": v(-1410.97, 278.13) * mm, "end": v(-1397.66, 292.2) * mm});
            skLineSegment(sketch, "E896", {"start": v(-1397.66, 292.2) * mm, "end": v(-1362.6, 324.74) * mm});
            skLineSegment(sketch, "E897", {"start": v(-1362.6, 324.74) * mm, "end": v(-1307.34, 358.9) * mm});
            skLineSegment(sketch, "E898", {"start": v(-1307.34, 358.9) * mm, "end": v(-1233.3, 377.95) * mm});
            skLineSegment(sketch, "E899", {"start": v(-1233.3, 377.95) * mm, "end": v(-1151.6, 392.48) * mm});
            skLineSegment(sketch, "E900", {"start": v(-1151.6, 392.48) * mm, "end": v(-1073.38, 413.05) * mm});
            skLineSegment(sketch, "E901", {"start": v(-1073.38, 413.05) * mm, "end": v(-1001.34, 439.65) * mm});
            skLineSegment(sketch, "E902", {"start": v(-1001.34, 439.65) * mm, "end": v(-938.2, 472.23) * mm});
            skLineSegment(sketch, "E903", {"start": v(-938.2, 472.23) * mm, "end": v(-884.42, 513.3) * mm});
            skLineSegment(sketch, "E904", {"start": v(-884.42, 513.3) * mm, "end": v(-840.43, 565.43) * mm});
            skLineSegment(sketch, "E905", {"start": v(-840.43, 565.43) * mm, "end": v(-804.77, 634.52) * mm});
            skLineSegment(sketch, "E906", {"start": v(-804.77, 634.52) * mm, "end": v(-775.97, 726.51) * mm});
            skLineSegment(sketch, "E907", {"start": v(-775.97, 726.51) * mm, "end": v(-756.49, 824.74) * mm});
            skLineSegment(sketch, "E908", {"start": v(-756.49, 824.74) * mm, "end": v(-748.87, 912.4) * mm});
            skLineSegment(sketch, "E909", {"start": v(-748.87, 912.4) * mm, "end": v(-747.54, 976.9) * mm});
            skLineSegment(sketch, "E910", {"start": v(-747.54, 976.9) * mm, "end": v(-747.06, 1005.69) * mm});
            skLineSegment(sketch, "E911", {"start": v(-747.06, 1005.69) * mm, "end": v(-747.04, 1016.38) * mm});
            skLineSegment(sketch, "E912", {"start": v(-747.04, 1016.38) * mm, "end": v(-747.19, 1026.67) * mm});
            skLineSegment(sketch, "E913", {"start": v(-747.19, 1026.67) * mm, "end": v(-747.72, 1048.64) * mm});
            skLineSegment(sketch, "E914", {"start": v(-747.72, 1048.64) * mm, "end": v(-747.72, 1048.64) * mm});
            skLineSegment(sketch, "E915", {"start": v(-747.72, 1048.64) * mm, "end": v(-747.95, 1058.31) * mm});
            skLineSegment(sketch, "E916", {"start": v(-747.95, 1058.31) * mm, "end": v(-748.5, 1081.2) * mm});
            skLineSegment(sketch, "E917", {"start": v(-748.5, 1081.2) * mm, "end": v(-749.8, 1133.07) * mm});
            skLineSegment(sketch, "E918", {"start": v(-749.8, 1133.07) * mm, "end": v(-750.14, 1162.12) * mm});
            skLineSegment(sketch, "E919", {"start": v(-750.14, 1162.12) * mm, "end": v(-750.9, 1228.14) * mm});
            skLineSegment(sketch, "E920", {"start": v(-750.9, 1228.14) * mm, "end": v(-750.42, 1256.43) * mm});
            skLineSegment(sketch, "E921", {"start": v(-750.42, 1256.43) * mm, "end": v(-749.3, 1320.85) * mm});
            skLineSegment(sketch, "E922", {"start": v(-749.3, 1320.85) * mm, "end": v(-748.43, 1347.55) * mm});
            skLineSegment(sketch, "E923", {"start": v(-748.43, 1347.55) * mm, "end": v(-746.48, 1408.25) * mm});
            skLineSegment(sketch, "E924", {"start": v(-746.48, 1408.25) * mm, "end": v(-745.66, 1432.58) * mm});
            skLineSegment(sketch, "E925", {"start": v(-745.66, 1432.58) * mm, "end": v(-743.81, 1487.45) * mm});
            skLineSegment(sketch, "E926", {"start": v(-743.81, 1487.45) * mm, "end": v(-741.35, 1507.74) * mm});
            skLineSegment(sketch, "E927", {"start": v(-741.35, 1507.74) * mm, "end": v(-735.76, 1553.36) * mm});
            skLineSegment(sketch, "E928", {"start": v(-735.76, 1553.36) * mm, "end": v(-729.94, 1567.97) * mm});
            skLineSegment(sketch, "E929", {"start": v(-729.94, 1567.97) * mm, "end": v(-716.81, 1600.93) * mm});
            skLineSegment(sketch, "E930", {"start": v(-716.81, 1600.93) * mm, "end": v(-691.18, 1633.98) * mm});
            skLineSegment(sketch, "E931", {"start": v(-691.18, 1633.98) * mm, "end": v(-663.09, 1656.38) * mm});
            skLineSegment(sketch, "E932", {"start": v(-663.09, 1656.38) * mm, "end": v(-639.82, 1669.62) * mm});
            skLineSegment(sketch, "E933", {"start": v(-639.82, 1669.62) * mm, "end": v(-628.75, 1675.18) * mm});
            skLineSegment(sketch, "E934", {"start": v(-628.75, 1675.18) * mm, "end": v(-616.58, 1679.32) * mm});
            skLineSegment(sketch, "E935", {"start": v(-616.58, 1679.32) * mm, "end": v(-590.04, 1688.33) * mm});
            skLineSegment(sketch, "E936", {"start": v(-590.04, 1688.33) * mm, "end": v(-562.94, 1696.92) * mm});
            skLineSegment(sketch, "E937", {"start": v(-562.94, 1696.92) * mm, "end": v(-549.1, 1699.8) * mm});
            skLineSegment(sketch, "E938", {"start": v(-549.1, 1699.8) * mm, "end": v(-549.1, 1699.8) * mm});
            skLineSegment(sketch, "E939", {"start": v(-549.1, 1699.8) * mm, "end": v(-543.68, 1696.13) * mm});
            skLineSegment(sketch, "E940", {"start": v(-543.68, 1696.13) * mm, "end": v(-541.88, 1685.14) * mm});
            skLineSegment(sketch, "E941", {"start": v(-541.88, 1685.14) * mm, "end": v(-541.88, 1540.81) * mm});
            skLineSegment(sketch, "E942", {"start": v(-541.88, 1540.81) * mm, "end": v(-541.86, 1493.42) * mm});
            skLineSegment(sketch, "E943", {"start": v(-541.86, 1521.36) * mm, "end": v(-541.86, 1053.74) * mm});
            skLineSegment(sketch, "E944", {"start": v(-541.86, 1071.52) * mm, "end": v(-536.52, 1063.67) * mm});
            skLineSegment(sketch, "E945", {"start": v(-536.52, 1063.67) * mm, "end": v(-520.44, 1061.03) * mm});
            skLineSegment(sketch, "E946", {"start": v(-520.44, 1061.03) * mm, "end": v(-478.94, 1061.03) * mm});
            skLineSegment(sketch, "E947", {"start": v(-478.94, 1061.03) * mm, "end": v(-463.85, 1064.54) * mm});
            skLineSegment(sketch, "E948", {"start": v(-463.85, 1064.54) * mm, "end": v(-463.85, 1064.54) * mm});
            skLineSegment(sketch, "E949", {"start": v(-463.85, 1064.54) * mm, "end": v(-458.85, 1074.98) * mm});
            skLineSegment(sketch, "E950", {"start": v(-458.85, 1062.28) * mm, "end": v(-458.85, 1473.99) * mm});
            skLineSegment(sketch, "E951", {"start": v(-458.85, 1440.97) * mm, "end": v(-458.82, 1494.76) * mm});
            skLineSegment(sketch, "E952", {"start": v(-458.82, 1494.76) * mm, "end": v(-458.82, 1581.43) * mm});
            skLineSegment(sketch, "E953", {"start": v(-458.82, 1581.43) * mm, "end": v(-458.85, 1622.32) * mm});
            skLineSegment(sketch, "E954", {"start": v(-458.85, 1622.32) * mm, "end": v(-458.85, 1688.2) * mm});
            skLineSegment(sketch, "E955", {"start": v(-458.85, 1688.2) * mm, "end": v(-458.85, 1688.2) * mm});
            skLineSegment(sketch, "E956", {"start": v(-458.85, 1688.2) * mm, "end": v(-458.85, 1688.21) * mm});
            skLineSegment(sketch, "E957", {"start": v(-458.85, 1688.21) * mm, "end": v(-455.88, 1696.9) * mm});
            skLineSegment(sketch, "E958", {"start": v(-455.88, 1696.9) * mm, "end": v(-446.94, 1699.8) * mm});
            skLineSegment(sketch, "E959", {"start": v(-446.94, 1699.8) * mm, "end": v(-428.44, 1697.43) * mm});
            skLineSegment(sketch, "E960", {"start": v(-428.44, 1697.43) * mm, "end": v(-396.74, 1690.34) * mm});
            skLineSegment(sketch, "E961", {"start": v(-396.74, 1690.34) * mm, "end": v(-367.05, 1683) * mm});
            skLineSegment(sketch, "E962", {"start": v(-367.05, 1683) * mm, "end": v(-354.56, 1679.93) * mm});
            skLineSegment(sketch, "E963", {"start": v(-354.56, 1679.93) * mm, "end": v(-354.56, 1679.93) * mm});
            skLineSegment(sketch, "E964", {"start": v(-354.56, 1679.93) * mm, "end": v(-345.64, 1675.1) * mm});
            skLineSegment(sketch, "E965", {"start": v(-345.64, 1675.1) * mm, "end": v(-326.64, 1662.6) * mm});
            skLineSegment(sketch, "E966", {"start": v(-326.64, 1662.6) * mm, "end": v(-302.59, 1639.95) * mm});
            skLineSegment(sketch, "E967", {"start": v(-302.59, 1639.95) * mm, "end": v(-278.43, 1604.7) * mm});
            skLineSegment(sketch, "E968", {"start": v(-278.43, 1604.7) * mm, "end": v(-265.88, 1570.25) * mm});
            skLineSegment(sketch, "E969", {"start": v(-265.88, 1570.25) * mm, "end": v(-260.35, 1555.04) * mm});
            skLineSegment(sketch, "E970", {"start": v(-260.35, 1555.04) * mm, "end": v(-256.26, 1509.3) * mm});
            skLineSegment(sketch, "E971", {"start": v(-256.26, 1509.3) * mm, "end": v(-254.45, 1489.07) * mm});
            skLineSegment(sketch, "E972", {"start": v(-254.45, 1489.07) * mm, "end": v(-254.6, 1435) * mm});
            skLineSegment(sketch, "E973", {"start": v(-254.6, 1435) * mm, "end": v(-254.68, 1411.1) * mm});
            skLineSegment(sketch, "E974", {"start": v(-254.68, 1411.1) * mm, "end": v(-254.91, 1351.66) * mm});
            skLineSegment(sketch, "E975", {"start": v(-254.91, 1351.66) * mm, "end": v(-255.01, 1325.42) * mm});
            skLineSegment(sketch, "E976", {"start": v(-255.01, 1325.42) * mm, "end": v(-255.06, 1262.2) * mm});
            skLineSegment(sketch, "E977", {"start": v(-255.06, 1262.2) * mm, "end": v(-255.09, 1234.31) * mm});
            skLineSegment(sketch, "E978", {"start": v(-255.09, 1234.31) * mm, "end": v(-254.7, 1168.88) * mm});
            skLineSegment(sketch, "E979", {"start": v(-254.7, 1168.88) * mm, "end": v(-254.53, 1140.03) * mm});
            skLineSegment(sketch, "E980", {"start": v(-254.53, 1140.03) * mm, "end": v(-254.05, 1087.73) * mm});
            skLineSegment(sketch, "E981", {"start": v(-254.05, 1087.73) * mm, "end": v(-253.84, 1064.66) * mm});
            skLineSegment(sketch, "E982", {"start": v(-253.84, 1064.66) * mm, "end": v(-253.62, 1040.84) * mm});
            skLineSegment(sketch, "E983", {"start": v(-253.62, 1040.84) * mm, "end": v(-253.54, 1030.35) * mm});
            skLineSegment(sketch, "E984", {"start": v(-253.54, 1030.35) * mm, "end": v(-253.44, 1017.3) * mm});
            skLineSegment(sketch, "E985", {"start": v(-253.44, 1017.3) * mm, "end": v(-253.34, 1005.69) * mm});
            skLineSegment(sketch, "E986", {"start": v(-253.34, 1005.69) * mm, "end": v(-252.83, 976.9) * mm});
            skLineSegment(sketch, "E987", {"start": v(-252.83, 976.9) * mm, "end": v(-251.53, 912.4) * mm});
            skLineSegment(sketch, "E988", {"start": v(-251.53, 912.4) * mm, "end": v(-243.89, 824.74) * mm});
            skLineSegment(sketch, "E989", {"start": v(-243.89, 824.74) * mm, "end": v(-224.43, 726.51) * mm});
            skLineSegment(sketch, "E990", {"start": v(-224.43, 726.51) * mm, "end": v(-195.63, 634.52) * mm});
            skLineSegment(sketch, "E991", {"start": v(-195.63, 634.52) * mm, "end": v(-159.97, 565.43) * mm});
            skLineSegment(sketch, "E992", {"start": v(-159.97, 565.43) * mm, "end": v(-115.97, 513.3) * mm});
            skLineSegment(sketch, "E993", {"start": v(-115.97, 513.3) * mm, "end": v(-62.2, 472.23) * mm});
            skLineSegment(sketch, "E994", {"start": v(-62.2, 472.23) * mm, "end": v(1.02, 439.65) * mm});
            skLineSegment(sketch, "E995", {"start": v(1.02, 439.65) * mm, "end": v(73.28, 413.05) * mm});
            skLineSegment(sketch, "E996", {"start": v(-1398.52, 190.78) * mm, "end": v(-1434.1, 192.91) * mm});
            skLineSegment(sketch, "E997", {"start": v(-1434.1, 192.91) * mm, "end": v(-1446.17, 199.26) * mm});
            skLineSegment(sketch, "E998", {"start": v(443.84, 214.8) * mm, "end": v(446.38, 199.54) * mm});
            skLineSegment(sketch, "E999", {"start": v(446.38, 199.54) * mm, "end": v(434.3, 192.99) * mm});
            skLineSegment(sketch, "E1000", {"start": v(434.3, 192.99) * mm, "end": v(398.7, 190.78) * mm});
            skLineSegment(sketch, "E1001", {"start": v(398.7, 190.78) * mm, "end": v(-1398.52, 190.78) * mm});
            skLineSegment(sketch, "E1002", {"start": v(73.28, 413.05) * mm, "end": v(153.4, 392.7) * mm});
            skLineSegment(sketch, "E1003", {"start": v(153.4, 392.7) * mm, "end": v(240.16, 378.92) * mm});
            skLineSegment(sketch, "E1004", {"start": v(240.16, 378.92) * mm, "end": v(319.2, 360.58) * mm});
            skLineSegment(sketch, "E1005", {"start": v(319.2, 360.58) * mm, "end": v(376.15, 326.64) * mm});
            skLineSegment(sketch, "E1006", {"start": v(376.15, 326.64) * mm, "end": v(410.87, 294.43) * mm});
            skLineSegment(sketch, "E1007", {"start": v(410.87, 294.43) * mm, "end": v(423.2, 281.35) * mm});
            skLineSegment(sketch, "E1008", {"start": v(423.2, 281.35) * mm, "end": v(423.2, 281.35) * mm});
            skLineSegment(sketch, "E1009", {"start": v(423.2, 281.35) * mm, "end": v(426.85, 270.03) * mm});
            skLineSegment(sketch, "E1010", {"start": v(426.85, 270.03) * mm, "end": v(435.54, 243.08) * mm});
            skLineSegment(sketch, "E1011", {"start": v(435.54, 243.08) * mm, "end": v(443.84, 214.8) * mm});
            skSolve(sketch);
        }
        {
            var Q0;
            Q0 = qSketchRegion(id + "F0", true);
            extrude(context, id + "F1", {"entities" : qUnion([Q0]), "depth" : 50.8 * mm, "offsetDistance" : 25.4 * mm});
        }
        {
            var Q0;
            Q0=makeQuery(id+"F1.opExtrude","CAP_FACE",FACE,{"disambiguationData":[OSD([sQuery(id+"F0.wireOp",EDGE,"E0"),sQuery(id+"F0.wireOp",EDGE,"E1"),sQuery(id+"F0.wireOp",EDGE,"E2"),sQuery(id+"F0.wireOp",EDGE,"E3"),sQuery(id+"F0.wireOp",EDGE,"E4"),sQuery(id+"F0.wireOp",EDGE,"E5"),sQuery(id+"F0.wireOp",EDGE,"E6"),sQuery(id+"F0.wireOp",EDGE,"E7"),sQuery(id+"F0.wireOp",EDGE,"E8"),sQuery(id+"F0.wireOp",EDGE,"E9"),sQuery(id+"F0.wireOp",EDGE,"E10"),sQuery(id+"F0.wireOp",EDGE,"E11"),sQuery(id+"F0.wireOp",EDGE,"E12"),sQuery(id+"F0.wireOp",EDGE,"E13"),sQuery(id+"F0.wireOp",EDGE,"E14"),sQuery(id+"F0.wireOp",EDGE,"E15"),sQuery(id+"F0.wireOp",EDGE,"E16"),sQuery(id+"F0.wireOp",EDGE,"E17"),sQuery(id+"F0.wireOp",EDGE,"E18"),sQuery(id+"F0.wireOp",EDGE,"E19"),sQuery(id+"F0.wireOp",EDGE,"E20"),sQuery(id+"F0.wireOp",EDGE,"E21"),sQuery(id+"F0.wireOp",EDGE,"E22"),sQuery(id+"F0.wireOp",EDGE,"E23"),sQuery(id+"F0.wireOp",EDGE,"E24"),sQuery(id+"F0.wireOp",EDGE,"E25"),sQuery(id+"F0.wireOp",EDGE,"E26"),sQuery(id+"F0.wireOp",EDGE,"E27"),sQuery(id+"F0.wireOp",EDGE,"E28"),sQuery(id+"F0.wireOp",EDGE,"E29"),sQuery(id+"F0.wireOp",EDGE,"E30"),sQuery(id+"F0.wireOp",EDGE,"E31"),sQuery(id+"F0.wireOp",EDGE,"E32"),sQuery(id+"F0.wireOp",EDGE,"E33"),sQuery(id+"F0.wireOp",EDGE,"E34"),sQuery(id+"F0.wireOp",EDGE,"E35"),sQuery(id+"F0.wireOp",EDGE,"E36"),sQuery(id+"F0.wireOp",EDGE,"E37"),sQuery(id+"F0.wireOp",EDGE,"E38"),sQuery(id+"F0.wireOp",EDGE,"E39"),sQuery(id+"F0.wireOp",EDGE,"E40"),sQuery(id+"F0.wireOp",EDGE,"E41"),sQuery(id+"F0.wireOp",EDGE,"E42"),sQuery(id+"F0.wireOp",EDGE,"E43"),sQuery(id+"F0.wireOp",EDGE,"E44"),sQuery(id+"F0.wireOp",EDGE,"E45"),sQuery(id+"F0.wireOp",EDGE,"E46"),sQuery(id+"F0.wireOp",EDGE,"E47"),sQuery(id+"F0.wireOp",EDGE,"E48"),sQuery(id+"F0.wireOp",EDGE,"E49"),sQuery(id+"F0.wireOp",EDGE,"E50"),sQuery(id+"F0.wireOp",EDGE,"E51"),sQuery(id+"F0.wireOp",EDGE,"E52"),sQuery(id+"F0.wireOp",EDGE,"E53"),sQuery(id+"F0.wireOp",EDGE,"E54"),sQuery(id+"F0.wireOp",EDGE,"E55"),sQuery(id+"F0.wireOp",EDGE,"E56"),sQuery(id+"F0.wireOp",EDGE,"E57"),sQuery(id+"F0.wireOp",EDGE,"E58"),sQuery(id+"F0.wireOp",EDGE,"E59"),sQuery(id+"F0.wireOp",EDGE,"E60"),sQuery(id+"F0.wireOp",EDGE,"E61"),sQuery(id+"F0.wireOp",EDGE,"E62"),sQuery(id+"F0.wireOp",EDGE,"E63"),sQuery(id+"F0.wireOp",EDGE,"E64"),sQuery(id+"F0.wireOp",EDGE,"E65"),sQuery(id+"F0.wireOp",EDGE,"E66"),sQuery(id+"F0.wireOp",EDGE,"E67"),sQuery(id+"F0.wireOp",EDGE,"E68"),sQuery(id+"F0.wireOp",EDGE,"E69"),sQuery(id+"F0.wireOp",EDGE,"E70"),sQuery(id+"F0.wireOp",EDGE,"E71"),sQuery(id+"F0.wireOp",EDGE,"E72"),sQuery(id+"F0.wireOp",EDGE,"E73"),sQuery(id+"F0.wireOp",EDGE,"E74"),sQuery(id+"F0.wireOp",EDGE,"E75"),sQuery(id+"F0.wireOp",EDGE,"E76"),sQuery(id+"F0.wireOp",EDGE,"E77"),sQuery(id+"F0.wireOp",EDGE,"E78"),sQuery(id+"F0.wireOp",EDGE,"E79"),sQuery(id+"F0.wireOp",EDGE,"E80"),sQuery(id+"F0.wireOp",EDGE,"E81"),sQuery(id+"F0.wireOp",EDGE,"E82"),sQuery(id+"F0.wireOp",EDGE,"E83"),sQuery(id+"F0.wireOp",EDGE,"E84"),sQuery(id+"F0.wireOp",EDGE,"E85"),sQuery(id+"F0.wireOp",EDGE,"E86"),sQuery(id+"F0.wireOp",EDGE,"E87"),sQuery(id+"F0.wireOp",EDGE,"E88"),sQuery(id+"F0.wireOp",EDGE,"E89"),sQuery(id+"F0.wireOp",EDGE,"E90"),sQuery(id+"F0.wireOp",EDGE,"E91"),sQuery(id+"F0.wireOp",EDGE,"E92"),sQuery(id+"F0.wireOp",EDGE,"E93"),sQuery(id+"F0.wireOp",EDGE,"E94"),sQuery(id+"F0.wireOp",EDGE,"E95"),sQuery(id+"F0.wireOp",EDGE,"E96"),sQuery(id+"F0.wireOp",EDGE,"E97"),sQuery(id+"F0.wireOp",EDGE,"E98"),sQuery(id+"F0.wireOp",EDGE,"E99"),sQuery(id+"F0.wireOp",EDGE,"E100"),sQuery(id+"F0.wireOp",EDGE,"E101"),sQuery(id+"F0.wireOp",EDGE,"E102"),sQuery(id+"F0.wireOp",EDGE,"E103"),sQuery(id+"F0.wireOp",EDGE,"E104"),sQuery(id+"F0.wireOp",EDGE,"E105"),sQuery(id+"F0.wireOp",EDGE,"E106"),sQuery(id+"F0.wireOp",EDGE,"E107"),sQuery(id+"F0.wireOp",EDGE,"E108"),sQuery(id+"F0.wireOp",EDGE,"E109"),sQuery(id+"F0.wireOp",EDGE,"E110"),sQuery(id+"F0.wireOp",EDGE,"E111"),sQuery(id+"F0.wireOp",EDGE,"E112"),sQuery(id+"F0.wireOp",EDGE,"E113"),sQuery(id+"F0.wireOp",EDGE,"E114"),sQuery(id+"F0.wireOp",EDGE,"E115"),sQuery(id+"F0.wireOp",EDGE,"E116"),sQuery(id+"F0.wireOp",EDGE,"E117"),sQuery(id+"F0.wireOp",EDGE,"E118"),sQuery(id+"F0.wireOp",EDGE,"E119"),sQuery(id+"F0.wireOp",EDGE,"E120"),sQuery(id+"F0.wireOp",EDGE,"E121"),sQuery(id+"F0.wireOp",EDGE,"E122"),sQuery(id+"F0.wireOp",EDGE,"E123"),sQuery(id+"F0.wireOp",EDGE,"E124"),sQuery(id+"F0.wireOp",EDGE,"E125"),sQuery(id+"F0.wireOp",EDGE,"E126"),sQuery(id+"F0.wireOp",EDGE,"E127"),sQuery(id+"F0.wireOp",EDGE,"E128"),sQuery(id+"F0.wireOp",EDGE,"E129"),sQuery(id+"F0.wireOp",EDGE,"E130"),sQuery(id+"F0.wireOp",EDGE,"E131"),sQuery(id+"F0.wireOp",EDGE,"E132"),sQuery(id+"F0.wireOp",EDGE,"E133"),sQuery(id+"F0.wireOp",EDGE,"E134"),sQuery(id+"F0.wireOp",EDGE,"E135"),sQuery(id+"F0.wireOp",EDGE,"E136"),sQuery(id+"F0.wireOp",EDGE,"E137"),sQuery(id+"F0.wireOp",EDGE,"E138"),sQuery(id+"F0.wireOp",EDGE,"E139"),sQuery(id+"F0.wireOp",EDGE,"E140"),sQuery(id+"F0.wireOp",EDGE,"E141"),sQuery(id+"F0.wireOp",EDGE,"E142"),sQuery(id+"F0.wireOp",EDGE,"E143"),sQuery(id+"F0.wireOp",EDGE,"E144"),sQuery(id+"F0.wireOp",EDGE,"E145"),sQuery(id+"F0.wireOp",EDGE,"E146"),sQuery(id+"F0.wireOp",EDGE,"E147"),sQuery(id+"F0.wireOp",EDGE,"E148"),sQuery(id+"F0.wireOp",EDGE,"E149"),sQuery(id+"F0.wireOp",EDGE,"E150"),sQuery(id+"F0.wireOp",EDGE,"E151"),sQuery(id+"F0.wireOp",EDGE,"E152"),sQuery(id+"F0.wireOp",EDGE,"E153"),sQuery(id+"F0.wireOp",EDGE,"E154"),sQuery(id+"F0.wireOp",EDGE,"E155"),sQuery(id+"F0.wireOp",EDGE,"E156"),sQuery(id+"F0.wireOp",EDGE,"E157"),sQuery(id+"F0.wireOp",EDGE,"E158"),sQuery(id+"F0.wireOp",EDGE,"E159"),sQuery(id+"F0.wireOp",EDGE,"E160"),sQuery(id+"F0.wireOp",EDGE,"E161"),sQuery(id+"F0.wireOp",EDGE,"E162"),sQuery(id+"F0.wireOp",EDGE,"E163"),sQuery(id+"F0.wireOp",EDGE,"E163"),sQuery(id+"F0.wireOp",EDGE,"E164"),sQuery(id+"F0.wireOp",EDGE,"E165"),sQuery(id+"F0.wireOp",EDGE,"E166"),sQuery(id+"F0.wireOp",EDGE,"E167"),sQuery(id+"F0.wireOp",EDGE,"E168"),sQuery(id+"F0.wireOp",EDGE,"E169"),sQuery(id+"F0.wireOp",EDGE,"E170"),sQuery(id+"F0.wireOp",EDGE,"E171"),sQuery(id+"F0.wireOp",EDGE,"E171"),sQuery(id+"F0.wireOp",EDGE,"E172"),sQuery(id+"F0.wireOp",EDGE,"E173"),sQuery(id+"F0.wireOp",EDGE,"E174"),sQuery(id+"F0.wireOp",EDGE,"E174"),sQuery(id+"F0.wireOp",EDGE,"E174"),sQuery(id+"F0.wireOp",EDGE,"E175"),sQuery(id+"F0.wireOp",EDGE,"E176"),sQuery(id+"F0.wireOp",EDGE,"E176"),sQuery(id+"F0.wireOp",EDGE,"E177"),sQuery(id+"F0.wireOp",EDGE,"E178"),sQuery(id+"F0.wireOp",EDGE,"E178"),sQuery(id+"F0.wireOp",EDGE,"E179"),sQuery(id+"F0.wireOp",EDGE,"E180"),sQuery(id+"F0.wireOp",EDGE,"E181"),sQuery(id+"F0.wireOp",EDGE,"E182"),sQuery(id+"F0.wireOp",EDGE,"E183"),sQuery(id+"F0.wireOp",EDGE,"E184"),sQuery(id+"F0.wireOp",EDGE,"E185"),sQuery(id+"F0.wireOp",EDGE,"E186"),sQuery(id+"F0.wireOp",EDGE,"E187"),sQuery(id+"F0.wireOp",EDGE,"E188"),sQuery(id+"F0.wireOp",EDGE,"E189"),sQuery(id+"F0.wireOp",EDGE,"E190"),sQuery(id+"F0.wireOp",EDGE,"E191"),sQuery(id+"F0.wireOp",EDGE,"E192"),sQuery(id+"F0.wireOp",EDGE,"E193"),sQuery(id+"F0.wireOp",EDGE,"E194"),sQuery(id+"F0.wireOp",EDGE,"E195"),sQuery(id+"F0.wireOp",EDGE,"E196"),sQuery(id+"F0.wireOp",EDGE,"E197"),sQuery(id+"F0.wireOp",EDGE,"E198"),sQuery(id+"F0.wireOp",EDGE,"E199"),sQuery(id+"F0.wireOp",EDGE,"E200"),sQuery(id+"F0.wireOp",EDGE,"E201"),sQuery(id+"F0.wireOp",EDGE,"E202"),sQuery(id+"F0.wireOp",EDGE,"E203"),sQuery(id+"F0.wireOp",EDGE,"E204"),sQuery(id+"F0.wireOp",EDGE,"E205"),sQuery(id+"F0.wireOp",EDGE,"E206"),sQuery(id+"F0.wireOp",EDGE,"E207"),sQuery(id+"F0.wireOp",EDGE,"E208"),sQuery(id+"F0.wireOp",EDGE,"E209"),sQuery(id+"F0.wireOp",EDGE,"E210"),sQuery(id+"F0.wireOp",EDGE,"E211"),sQuery(id+"F0.wireOp",EDGE,"E212"),sQuery(id+"F0.wireOp",EDGE,"E213"),sQuery(id+"F0.wireOp",EDGE,"E214"),sQuery(id+"F0.wireOp",EDGE,"E215"),sQuery(id+"F0.wireOp",EDGE,"E216"),sQuery(id+"F0.wireOp",EDGE,"E217"),sQuery(id+"F0.wireOp",EDGE,"E218"),sQuery(id+"F0.wireOp",EDGE,"E219"),sQuery(id+"F0.wireOp",EDGE,"E220"),sQuery(id+"F0.wireOp",EDGE,"E221"),sQuery(id+"F0.wireOp",EDGE,"E222"),sQuery(id+"F0.wireOp",EDGE,"E223"),sQuery(id+"F0.wireOp",EDGE,"E224"),sQuery(id+"F0.wireOp",EDGE,"E225"),sQuery(id+"F0.wireOp",EDGE,"E226"),sQuery(id+"F0.wireOp",EDGE,"E227"),sQuery(id+"F0.wireOp",EDGE,"E228"),sQuery(id+"F0.wireOp",EDGE,"E229"),sQuery(id+"F0.wireOp",EDGE,"E230"),sQuery(id+"F0.wireOp",EDGE,"E231"),sQuery(id+"F0.wireOp",EDGE,"E232"),sQuery(id+"F0.wireOp",EDGE,"E233"),sQuery(id+"F0.wireOp",EDGE,"E234"),sQuery(id+"F0.wireOp",EDGE,"E235"),sQuery(id+"F0.wireOp",EDGE,"E236"),sQuery(id+"F0.wireOp",EDGE,"E237"),sQuery(id+"F0.wireOp",EDGE,"E238"),sQuery(id+"F0.wireOp",EDGE,"E239"),sQuery(id+"F0.wireOp",EDGE,"E240"),sQuery(id+"F0.wireOp",EDGE,"E241"),sQuery(id+"F0.wireOp",EDGE,"E242"),sQuery(id+"F0.wireOp",EDGE,"E243"),sQuery(id+"F0.wireOp",EDGE,"E244"),sQuery(id+"F0.wireOp",EDGE,"E245"),sQuery(id+"F0.wireOp",EDGE,"E246"),sQuery(id+"F0.wireOp",EDGE,"E247"),sQuery(id+"F0.wireOp",EDGE,"E248"),sQuery(id+"F0.wireOp",EDGE,"E249"),sQuery(id+"F0.wireOp",EDGE,"E250"),sQuery(id+"F0.wireOp",EDGE,"E251"),sQuery(id+"F0.wireOp",EDGE,"E252"),sQuery(id+"F0.wireOp",EDGE,"E253"),sQuery(id+"F0.wireOp",EDGE,"E254"),sQuery(id+"F0.wireOp",EDGE,"E255"),sQuery(id+"F0.wireOp",EDGE,"E256"),sQuery(id+"F0.wireOp",EDGE,"E257"),sQuery(id+"F0.wireOp",EDGE,"E258"),sQuery(id+"F0.wireOp",EDGE,"E259"),sQuery(id+"F0.wireOp",EDGE,"E260"),sQuery(id+"F0.wireOp",EDGE,"E261"),sQuery(id+"F0.wireOp",EDGE,"E262"),sQuery(id+"F0.wireOp",EDGE,"E263"),sQuery(id+"F0.wireOp",EDGE,"E264"),sQuery(id+"F0.wireOp",EDGE,"E265"),sQuery(id+"F0.wireOp",EDGE,"E266"),sQuery(id+"F0.wireOp",EDGE,"E267"),sQuery(id+"F0.wireOp",EDGE,"E268"),sQuery(id+"F0.wireOp",EDGE,"E269"),sQuery(id+"F0.wireOp",EDGE,"E270"),sQuery(id+"F0.wireOp",EDGE,"E271"),sQuery(id+"F0.wireOp",EDGE,"E272"),sQuery(id+"F0.wireOp",EDGE,"E273"),sQuery(id+"F0.wireOp",EDGE,"E274"),sQuery(id+"F0.wireOp",EDGE,"E275"),sQuery(id+"F0.wireOp",EDGE,"E276"),sQuery(id+"F0.wireOp",EDGE,"E277"),sQuery(id+"F0.wireOp",EDGE,"E278"),sQuery(id+"F0.wireOp",EDGE,"E279"),sQuery(id+"F0.wireOp",EDGE,"E280"),sQuery(id+"F0.wireOp",EDGE,"E281"),sQuery(id+"F0.wireOp",EDGE,"E282"),sQuery(id+"F0.wireOp",EDGE,"E283"),sQuery(id+"F0.wireOp",EDGE,"E284"),sQuery(id+"F0.wireOp",EDGE,"E285"),sQuery(id+"F0.wireOp",EDGE,"E286"),sQuery(id+"F0.wireOp",EDGE,"E287"),sQuery(id+"F0.wireOp",EDGE,"E288"),sQuery(id+"F0.wireOp",EDGE,"E289"),sQuery(id+"F0.wireOp",EDGE,"E290"),sQuery(id+"F0.wireOp",EDGE,"E291"),sQuery(id+"F0.wireOp",EDGE,"E292"),sQuery(id+"F0.wireOp",EDGE,"E293"),sQuery(id+"F0.wireOp",EDGE,"E294"),sQuery(id+"F0.wireOp",EDGE,"E295"),sQuery(id+"F0.wireOp",EDGE,"E296"),sQuery(id+"F0.wireOp",EDGE,"E297"),sQuery(id+"F0.wireOp",EDGE,"E297"),sQuery(id+"F0.wireOp",EDGE,"E298"),sQuery(id+"F0.wireOp",EDGE,"E299"),sQuery(id+"F0.wireOp",EDGE,"E300"),sQuery(id+"F0.wireOp",EDGE,"E301"),sQuery(id+"F0.wireOp",EDGE,"E302"),sQuery(id+"F0.wireOp",EDGE,"E303"),sQuery(id+"F0.wireOp",EDGE,"E304"),sQuery(id+"F0.wireOp",EDGE,"E305"),sQuery(id+"F0.wireOp",EDGE,"E306"),sQuery(id+"F0.wireOp",EDGE,"E307"),sQuery(id+"F0.wireOp",EDGE,"E308"),sQuery(id+"F0.wireOp",EDGE,"E309"),sQuery(id+"F0.wireOp",EDGE,"E310"),sQuery(id+"F0.wireOp",EDGE,"E311"),sQuery(id+"F0.wireOp",EDGE,"E312"),sQuery(id+"F0.wireOp",EDGE,"E313"),sQuery(id+"F0.wireOp",EDGE,"E314"),sQuery(id+"F0.wireOp",EDGE,"E315"),sQuery(id+"F0.wireOp",EDGE,"E316"),sQuery(id+"F0.wireOp",EDGE,"E317"),sQuery(id+"F0.wireOp",EDGE,"E318"),sQuery(id+"F0.wireOp",EDGE,"E319"),sQuery(id+"F0.wireOp",EDGE,"E320"),sQuery(id+"F0.wireOp",EDGE,"E321"),sQuery(id+"F0.wireOp",EDGE,"E322"),sQuery(id+"F0.wireOp",EDGE,"E323"),sQuery(id+"F0.wireOp",EDGE,"E324"),sQuery(id+"F0.wireOp",EDGE,"E325"),sQuery(id+"F0.wireOp",EDGE,"E326"),sQuery(id+"F0.wireOp",EDGE,"E327"),sQuery(id+"F0.wireOp",EDGE,"E328"),sQuery(id+"F0.wireOp",EDGE,"E329"),sQuery(id+"F0.wireOp",EDGE,"E330"),sQuery(id+"F0.wireOp",EDGE,"E331"),sQuery(id+"F0.wireOp",EDGE,"E332"),sQuery(id+"F0.wireOp",EDGE,"E333"),sQuery(id+"F0.wireOp",EDGE,"E334"),sQuery(id+"F0.wireOp",EDGE,"E335"),sQuery(id+"F0.wireOp",EDGE,"E336"),sQuery(id+"F0.wireOp",EDGE,"E337"),sQuery(id+"F0.wireOp",EDGE,"E338"),sQuery(id+"F0.wireOp",EDGE,"E339"),sQuery(id+"F0.wireOp",EDGE,"E340"),sQuery(id+"F0.wireOp",EDGE,"E341"),sQuery(id+"F0.wireOp",EDGE,"E342"),sQuery(id+"F0.wireOp",EDGE,"E343"),sQuery(id+"F0.wireOp",EDGE,"E344"),sQuery(id+"F0.wireOp",EDGE,"E345"),sQuery(id+"F0.wireOp",EDGE,"E346"),sQuery(id+"F0.wireOp",EDGE,"E347"),sQuery(id+"F0.wireOp",EDGE,"E348"),sQuery(id+"F0.wireOp",EDGE,"E349"),sQuery(id+"F0.wireOp",EDGE,"E350"),sQuery(id+"F0.wireOp",EDGE,"E351"),sQuery(id+"F0.wireOp",EDGE,"E352"),sQuery(id+"F0.wireOp",EDGE,"E353"),sQuery(id+"F0.wireOp",EDGE,"E354"),sQuery(id+"F0.wireOp",EDGE,"E355"),sQuery(id+"F0.wireOp",EDGE,"E356"),sQuery(id+"F0.wireOp",EDGE,"E357"),sQuery(id+"F0.wireOp",EDGE,"E358"),sQuery(id+"F0.wireOp",EDGE,"E359"),sQuery(id+"F0.wireOp",EDGE,"E360"),sQuery(id+"F0.wireOp",EDGE,"E361"),sQuery(id+"F0.wireOp",EDGE,"E362"),sQuery(id+"F0.wireOp",EDGE,"E363"),sQuery(id+"F0.wireOp",EDGE,"E364"),sQuery(id+"F0.wireOp",EDGE,"E365"),sQuery(id+"F0.wireOp",EDGE,"E366"),sQuery(id+"F0.wireOp",EDGE,"E367"),sQuery(id+"F0.wireOp",EDGE,"E368"),sQuery(id+"F0.wireOp",EDGE,"E369"),sQuery(id+"F0.wireOp",EDGE,"E370"),sQuery(id+"F0.wireOp",EDGE,"E371"),sQuery(id+"F0.wireOp",EDGE,"E372"),sQuery(id+"F0.wireOp",EDGE,"E373"),sQuery(id+"F0.wireOp",EDGE,"E374"),sQuery(id+"F0.wireOp",EDGE,"E375"),sQuery(id+"F0.wireOp",EDGE,"E376"),sQuery(id+"F0.wireOp",EDGE,"E377"),sQuery(id+"F0.wireOp",EDGE,"E378"),sQuery(id+"F0.wireOp",EDGE,"E379"),sQuery(id+"F0.wireOp",EDGE,"E380"),sQuery(id+"F0.wireOp",EDGE,"E381"),sQuery(id+"F0.wireOp",EDGE,"E382"),sQuery(id+"F0.wireOp",EDGE,"E383"),sQuery(id+"F0.wireOp",EDGE,"E384"),sQuery(id+"F0.wireOp",EDGE,"E385"),sQuery(id+"F0.wireOp",EDGE,"E386"),sQuery(id+"F0.wireOp",EDGE,"E387"),sQuery(id+"F0.wireOp",EDGE,"E388"),sQuery(id+"F0.wireOp",EDGE,"E389"),sQuery(id+"F0.wireOp",EDGE,"E390"),sQuery(id+"F0.wireOp",EDGE,"E391"),sQuery(id+"F0.wireOp",EDGE,"E392"),sQuery(id+"F0.wireOp",EDGE,"E393"),sQuery(id+"F0.wireOp",EDGE,"E394"),sQuery(id+"F0.wireOp",EDGE,"E395"),sQuery(id+"F0.wireOp",EDGE,"E396"),sQuery(id+"F0.wireOp",EDGE,"E397"),sQuery(id+"F0.wireOp",EDGE,"E398"),sQuery(id+"F0.wireOp",EDGE,"E399"),sQuery(id+"F0.wireOp",EDGE,"E400"),sQuery(id+"F0.wireOp",EDGE,"E401"),sQuery(id+"F0.wireOp",EDGE,"E402"),sQuery(id+"F0.wireOp",EDGE,"E403"),sQuery(id+"F0.wireOp",EDGE,"E404"),sQuery(id+"F0.wireOp",EDGE,"E405"),sQuery(id+"F0.wireOp",EDGE,"E406"),sQuery(id+"F0.wireOp",EDGE,"E407"),sQuery(id+"F0.wireOp",EDGE,"E408"),sQuery(id+"F0.wireOp",EDGE,"E409"),sQuery(id+"F0.wireOp",EDGE,"E410"),sQuery(id+"F0.wireOp",EDGE,"E411"),sQuery(id+"F0.wireOp",EDGE,"E412"),sQuery(id+"F0.wireOp",EDGE,"E413"),sQuery(id+"F0.wireOp",EDGE,"E414"),sQuery(id+"F0.wireOp",EDGE,"E415"),sQuery(id+"F0.wireOp",EDGE,"E416"),sQuery(id+"F0.wireOp",EDGE,"E417"),sQuery(id+"F0.wireOp",EDGE,"E418"),sQuery(id+"F0.wireOp",EDGE,"E419"),sQuery(id+"F0.wireOp",EDGE,"E420"),sQuery(id+"F0.wireOp",EDGE,"E421"),sQuery(id+"F0.wireOp",EDGE,"E422"),sQuery(id+"F0.wireOp",EDGE,"E423"),sQuery(id+"F0.wireOp",EDGE,"E424"),sQuery(id+"F0.wireOp",EDGE,"E425"),sQuery(id+"F0.wireOp",EDGE,"E426"),sQuery(id+"F0.wireOp",EDGE,"E427"),sQuery(id+"F0.wireOp",EDGE,"E428"),sQuery(id+"F0.wireOp",EDGE,"E429"),sQuery(id+"F0.wireOp",EDGE,"E430"),sQuery(id+"F0.wireOp",EDGE,"E431"),sQuery(id+"F0.wireOp",EDGE,"E432"),sQuery(id+"F0.wireOp",EDGE,"E433"),sQuery(id+"F0.wireOp",EDGE,"E434"),sQuery(id+"F0.wireOp",EDGE,"E434"),sQuery(id+"F0.wireOp",EDGE,"E434"),sQuery(id+"F0.wireOp",EDGE,"E435"),sQuery(id+"F0.wireOp",EDGE,"E436"),sQuery(id+"F0.wireOp",EDGE,"E437"),sQuery(id+"F0.wireOp",EDGE,"E438"),sQuery(id+"F0.wireOp",EDGE,"E439"),sQuery(id+"F0.wireOp",EDGE,"E440"),sQuery(id+"F0.wireOp",EDGE,"E441"),sQuery(id+"F0.wireOp",EDGE,"E442"),sQuery(id+"F0.wireOp",EDGE,"E443"),sQuery(id+"F0.wireOp",EDGE,"E444"),sQuery(id+"F0.wireOp",EDGE,"E445"),sQuery(id+"F0.wireOp",EDGE,"E446"),sQuery(id+"F0.wireOp",EDGE,"E447"),sQuery(id+"F0.wireOp",EDGE,"E448"),sQuery(id+"F0.wireOp",EDGE,"E449"),sQuery(id+"F0.wireOp",EDGE,"E450"),sQuery(id+"F0.wireOp",EDGE,"E451"),sQuery(id+"F0.wireOp",EDGE,"E452"),sQuery(id+"F0.wireOp",EDGE,"E453"),sQuery(id+"F0.wireOp",EDGE,"E454"),sQuery(id+"F0.wireOp",EDGE,"E455"),sQuery(id+"F0.wireOp",EDGE,"E456"),sQuery(id+"F0.wireOp",EDGE,"E457"),sQuery(id+"F0.wireOp",EDGE,"E458"),sQuery(id+"F0.wireOp",EDGE,"E459"),sQuery(id+"F0.wireOp",EDGE,"E460"),sQuery(id+"F0.wireOp",EDGE,"E461"),sQuery(id+"F0.wireOp",EDGE,"E462"),sQuery(id+"F0.wireOp",EDGE,"E463"),sQuery(id+"F0.wireOp",EDGE,"E464"),sQuery(id+"F0.wireOp",EDGE,"E465"),sQuery(id+"F0.wireOp",EDGE,"E466"),sQuery(id+"F0.wireOp",EDGE,"E467"),sQuery(id+"F0.wireOp",EDGE,"E468"),sQuery(id+"F0.wireOp",EDGE,"E469"),sQuery(id+"F0.wireOp",EDGE,"E470"),sQuery(id+"F0.wireOp",EDGE,"E471"),sQuery(id+"F0.wireOp",EDGE,"E472"),sQuery(id+"F0.wireOp",EDGE,"E473"),sQuery(id+"F0.wireOp",EDGE,"E474"),sQuery(id+"F0.wireOp",EDGE,"E475"),sQuery(id+"F0.wireOp",EDGE,"E476"),sQuery(id+"F0.wireOp",EDGE,"E477"),sQuery(id+"F0.wireOp",EDGE,"E478"),sQuery(id+"F0.wireOp",EDGE,"E479"),sQuery(id+"F0.wireOp",EDGE,"E480"),sQuery(id+"F0.wireOp",EDGE,"E481"),sQuery(id+"F0.wireOp",EDGE,"E482"),sQuery(id+"F0.wireOp",EDGE,"E483"),sQuery(id+"F0.wireOp",EDGE,"E484"),sQuery(id+"F0.wireOp",EDGE,"E485"),sQuery(id+"F0.wireOp",EDGE,"E486"),sQuery(id+"F0.wireOp",EDGE,"E487"),sQuery(id+"F0.wireOp",EDGE,"E488"),sQuery(id+"F0.wireOp",EDGE,"E489"),sQuery(id+"F0.wireOp",EDGE,"E489"),sQuery(id+"F0.wireOp",EDGE,"E489"),sQuery(id+"F0.wireOp",EDGE,"E490"),sQuery(id+"F0.wireOp",EDGE,"E491"),sQuery(id+"F0.wireOp",EDGE,"E492"),sQuery(id+"F0.wireOp",EDGE,"E493"),sQuery(id+"F0.wireOp",EDGE,"E494"),sQuery(id+"F0.wireOp",EDGE,"E495"),sQuery(id+"F0.wireOp",EDGE,"E496"),sQuery(id+"F0.wireOp",EDGE,"E497"),sQuery(id+"F0.wireOp",EDGE,"E498"),sQuery(id+"F0.wireOp",EDGE,"E498"),sQuery(id+"F0.wireOp",EDGE,"E499"),sQuery(id+"F0.wireOp",EDGE,"E500"),sQuery(id+"F0.wireOp",EDGE,"E501"),sQuery(id+"F0.wireOp",EDGE,"E502"),sQuery(id+"F0.wireOp",EDGE,"E503"),sQuery(id+"F0.wireOp",EDGE,"E504"),sQuery(id+"F0.wireOp",EDGE,"E505"),sQuery(id+"F0.wireOp",EDGE,"E506"),sQuery(id+"F0.wireOp",EDGE,"E507"),sQuery(id+"F0.wireOp",EDGE,"E508"),sQuery(id+"F0.wireOp",EDGE,"E509"),sQuery(id+"F0.wireOp",EDGE,"E510"),sQuery(id+"F0.wireOp",EDGE,"E510"),sQuery(id+"F0.wireOp",EDGE,"E510"),sQuery(id+"F0.wireOp",EDGE,"E511"),sQuery(id+"F0.wireOp",EDGE,"E512"),sQuery(id+"F0.wireOp",EDGE,"E513"),sQuery(id+"F0.wireOp",EDGE,"E514"),sQuery(id+"F0.wireOp",EDGE,"E515"),sQuery(id+"F0.wireOp",EDGE,"E516"),sQuery(id+"F0.wireOp",EDGE,"E517"),sQuery(id+"F0.wireOp",EDGE,"E518"),sQuery(id+"F0.wireOp",EDGE,"E519"),sQuery(id+"F0.wireOp",EDGE,"E520"),sQuery(id+"F0.wireOp",EDGE,"E521"),sQuery(id+"F0.wireOp",EDGE,"E522"),sQuery(id+"F0.wireOp",EDGE,"E523"),sQuery(id+"F0.wireOp",EDGE,"E523"),sQuery(id+"F0.wireOp",EDGE,"E524"),sQuery(id+"F0.wireOp",EDGE,"E525"),sQuery(id+"F0.wireOp",EDGE,"E526"),sQuery(id+"F0.wireOp",EDGE,"E527"),sQuery(id+"F0.wireOp",EDGE,"E528"),sQuery(id+"F0.wireOp",EDGE,"E529"),sQuery(id+"F0.wireOp",EDGE,"E530"),sQuery(id+"F0.wireOp",EDGE,"E531"),sQuery(id+"F0.wireOp",EDGE,"E532"),sQuery(id+"F0.wireOp",EDGE,"E533"),sQuery(id+"F0.wireOp",EDGE,"E534"),sQuery(id+"F0.wireOp",EDGE,"E534"),sQuery(id+"F0.wireOp",EDGE,"E534"),sQuery(id+"F0.wireOp",EDGE,"E534"),sQuery(id+"F0.wireOp",EDGE,"E534"),sQuery(id+"F0.wireOp",EDGE,"E535"),sQuery(id+"F0.wireOp",EDGE,"E536"),sQuery(id+"F0.wireOp",EDGE,"E537"),sQuery(id+"F0.wireOp",EDGE,"E538"),sQuery(id+"F0.wireOp",EDGE,"E539"),sQuery(id+"F0.wireOp",EDGE,"E540"),sQuery(id+"F0.wireOp",EDGE,"E541"),sQuery(id+"F0.wireOp",EDGE,"E542"),sQuery(id+"F0.wireOp",EDGE,"E543"),sQuery(id+"F0.wireOp",EDGE,"E544"),sQuery(id+"F0.wireOp",EDGE,"E545"),sQuery(id+"F0.wireOp",EDGE,"E546"),sQuery(id+"F0.wireOp",EDGE,"E547"),sQuery(id+"F0.wireOp",EDGE,"E548"),sQuery(id+"F0.wireOp",EDGE,"E549"),sQuery(id+"F0.wireOp",EDGE,"E550"),sQuery(id+"F0.wireOp",EDGE,"E551"),sQuery(id+"F0.wireOp",EDGE,"E552"),sQuery(id+"F0.wireOp",EDGE,"E553"),sQuery(id+"F0.wireOp",EDGE,"E554"),sQuery(id+"F0.wireOp",EDGE,"E555"),sQuery(id+"F0.wireOp",EDGE,"E556"),sQuery(id+"F0.wireOp",EDGE,"E557"),sQuery(id+"F0.wireOp",EDGE,"E558"),sQuery(id+"F0.wireOp",EDGE,"E559"),sQuery(id+"F0.wireOp",EDGE,"E560"),sQuery(id+"F0.wireOp",EDGE,"E561"),sQuery(id+"F0.wireOp",EDGE,"E562"),sQuery(id+"F0.wireOp",EDGE,"E563"),sQuery(id+"F0.wireOp",EDGE,"E564"),sQuery(id+"F0.wireOp",EDGE,"E565"),sQuery(id+"F0.wireOp",EDGE,"E566"),sQuery(id+"F0.wireOp",EDGE,"E567"),sQuery(id+"F0.wireOp",EDGE,"E568"),sQuery(id+"F0.wireOp",EDGE,"E569"),sQuery(id+"F0.wireOp",EDGE,"E570"),sQuery(id+"F0.wireOp",EDGE,"E571"),sQuery(id+"F0.wireOp",EDGE,"E572"),sQuery(id+"F0.wireOp",EDGE,"E573"),sQuery(id+"F0.wireOp",EDGE,"E574"),sQuery(id+"F0.wireOp",EDGE,"E575"),sQuery(id+"F0.wireOp",EDGE,"E576"),sQuery(id+"F0.wireOp",EDGE,"E577"),sQuery(id+"F0.wireOp",EDGE,"E578"),sQuery(id+"F0.wireOp",EDGE,"E579"),sQuery(id+"F0.wireOp",EDGE,"E580"),sQuery(id+"F0.wireOp",EDGE,"E581"),sQuery(id+"F0.wireOp",EDGE,"E582"),sQuery(id+"F0.wireOp",EDGE,"E583"),sQuery(id+"F0.wireOp",EDGE,"E584"),sQuery(id+"F0.wireOp",EDGE,"E585"),sQuery(id+"F0.wireOp",EDGE,"E586"),sQuery(id+"F0.wireOp",EDGE,"E587"),sQuery(id+"F0.wireOp",EDGE,"E588"),sQuery(id+"F0.wireOp",EDGE,"E589"),sQuery(id+"F0.wireOp",EDGE,"E590"),sQuery(id+"F0.wireOp",EDGE,"E591"),sQuery(id+"F0.wireOp",EDGE,"E592"),sQuery(id+"F0.wireOp",EDGE,"E593"),sQuery(id+"F0.wireOp",EDGE,"E594"),sQuery(id+"F0.wireOp",EDGE,"E595"),sQuery(id+"F0.wireOp",EDGE,"E596"),sQuery(id+"F0.wireOp",EDGE,"E597"),sQuery(id+"F0.wireOp",EDGE,"E598"),sQuery(id+"F0.wireOp",EDGE,"E599"),sQuery(id+"F0.wireOp",EDGE,"E600"),sQuery(id+"F0.wireOp",EDGE,"E601"),sQuery(id+"F0.wireOp",EDGE,"E602"),sQuery(id+"F0.wireOp",EDGE,"E603"),sQuery(id+"F0.wireOp",EDGE,"E604"),sQuery(id+"F0.wireOp",EDGE,"E605"),sQuery(id+"F0.wireOp",EDGE,"E606"),sQuery(id+"F0.wireOp",EDGE,"E607"),sQuery(id+"F0.wireOp",EDGE,"E608"),sQuery(id+"F0.wireOp",EDGE,"E609"),sQuery(id+"F0.wireOp",EDGE,"E610"),sQuery(id+"F0.wireOp",EDGE,"E611"),sQuery(id+"F0.wireOp",EDGE,"E612"),sQuery(id+"F0.wireOp",EDGE,"E613"),sQuery(id+"F0.wireOp",EDGE,"E614"),sQuery(id+"F0.wireOp",EDGE,"E615"),sQuery(id+"F0.wireOp",EDGE,"E616"),sQuery(id+"F0.wireOp",EDGE,"E616"),sQuery(id+"F0.wireOp",EDGE,"E617"),sQuery(id+"F0.wireOp",EDGE,"E618"),sQuery(id+"F0.wireOp",EDGE,"E619"),sQuery(id+"F0.wireOp",EDGE,"E620"),sQuery(id+"F0.wireOp",EDGE,"E621"),sQuery(id+"F0.wireOp",EDGE,"E622"),sQuery(id+"F0.wireOp",EDGE,"E623"),sQuery(id+"F0.wireOp",EDGE,"E624"),sQuery(id+"F0.wireOp",EDGE,"E625"),sQuery(id+"F0.wireOp",EDGE,"E626"),sQuery(id+"F0.wireOp",EDGE,"E627"),sQuery(id+"F0.wireOp",EDGE,"E628"),sQuery(id+"F0.wireOp",EDGE,"E629"),sQuery(id+"F0.wireOp",EDGE,"E630"),sQuery(id+"F0.wireOp",EDGE,"E631"),sQuery(id+"F0.wireOp",EDGE,"E632"),sQuery(id+"F0.wireOp",EDGE,"E633"),sQuery(id+"F0.wireOp",EDGE,"E634"),sQuery(id+"F0.wireOp",EDGE,"E635"),sQuery(id+"F0.wireOp",EDGE,"E636"),sQuery(id+"F0.wireOp",EDGE,"E637"),sQuery(id+"F0.wireOp",EDGE,"E638"),sQuery(id+"F0.wireOp",EDGE,"E639"),sQuery(id+"F0.wireOp",EDGE,"E640"),sQuery(id+"F0.wireOp",EDGE,"E641"),sQuery(id+"F0.wireOp",EDGE,"E642"),sQuery(id+"F0.wireOp",EDGE,"E643"),sQuery(id+"F0.wireOp",EDGE,"E644"),sQuery(id+"F0.wireOp",EDGE,"E645"),sQuery(id+"F0.wireOp",EDGE,"E646"),sQuery(id+"F0.wireOp",EDGE,"E647"),sQuery(id+"F0.wireOp",EDGE,"E648"),sQuery(id+"F0.wireOp",EDGE,"E649"),sQuery(id+"F0.wireOp",EDGE,"E650"),sQuery(id+"F0.wireOp",EDGE,"E651"),sQuery(id+"F0.wireOp",EDGE,"E652"),sQuery(id+"F0.wireOp",EDGE,"E653"),sQuery(id+"F0.wireOp",EDGE,"E654"),sQuery(id+"F0.wireOp",EDGE,"E655"),sQuery(id+"F0.wireOp",EDGE,"E656"),sQuery(id+"F0.wireOp",EDGE,"E657"),sQuery(id+"F0.wireOp",EDGE,"E658"),sQuery(id+"F0.wireOp",EDGE,"E659"),sQuery(id+"F0.wireOp",EDGE,"E660"),sQuery(id+"F0.wireOp",EDGE,"E661"),sQuery(id+"F0.wireOp",EDGE,"E662"),sQuery(id+"F0.wireOp",EDGE,"E663"),sQuery(id+"F0.wireOp",EDGE,"E664"),sQuery(id+"F0.wireOp",EDGE,"E665"),sQuery(id+"F0.wireOp",EDGE,"E666"),sQuery(id+"F0.wireOp",EDGE,"E667"),sQuery(id+"F0.wireOp",EDGE,"E668"),sQuery(id+"F0.wireOp",EDGE,"E669"),sQuery(id+"F0.wireOp",EDGE,"E670"),sQuery(id+"F0.wireOp",EDGE,"E671"),sQuery(id+"F0.wireOp",EDGE,"E672"),sQuery(id+"F0.wireOp",EDGE,"E673"),sQuery(id+"F0.wireOp",EDGE,"E674"),sQuery(id+"F0.wireOp",EDGE,"E675"),sQuery(id+"F0.wireOp",EDGE,"E676"),sQuery(id+"F0.wireOp",EDGE,"E677"),sQuery(id+"F0.wireOp",EDGE,"E678"),sQuery(id+"F0.wireOp",EDGE,"E679"),sQuery(id+"F0.wireOp",EDGE,"E679"),sQuery(id+"F0.wireOp",EDGE,"E680"),sQuery(id+"F0.wireOp",EDGE,"E681"),sQuery(id+"F0.wireOp",EDGE,"E682"),sQuery(id+"F0.wireOp",EDGE,"E683"),sQuery(id+"F0.wireOp",EDGE,"E684"),sQuery(id+"F0.wireOp",EDGE,"E685"),sQuery(id+"F0.wireOp",EDGE,"E686"),sQuery(id+"F0.wireOp",EDGE,"E687"),sQuery(id+"F0.wireOp",EDGE,"E688"),sQuery(id+"F0.wireOp",EDGE,"E689"),sQuery(id+"F0.wireOp",EDGE,"E690"),sQuery(id+"F0.wireOp",EDGE,"E691"),sQuery(id+"F0.wireOp",EDGE,"E692"),sQuery(id+"F0.wireOp",EDGE,"E693"),sQuery(id+"F0.wireOp",EDGE,"E694"),sQuery(id+"F0.wireOp",EDGE,"E695"),sQuery(id+"F0.wireOp",EDGE,"E696"),sQuery(id+"F0.wireOp",EDGE,"E697"),sQuery(id+"F0.wireOp",EDGE,"E698"),sQuery(id+"F0.wireOp",EDGE,"E699"),sQuery(id+"F0.wireOp",EDGE,"E700"),sQuery(id+"F0.wireOp",EDGE,"E701"),sQuery(id+"F0.wireOp",EDGE,"E702"),sQuery(id+"F0.wireOp",EDGE,"E703"),sQuery(id+"F0.wireOp",EDGE,"E704"),sQuery(id+"F0.wireOp",EDGE,"E705"),sQuery(id+"F0.wireOp",EDGE,"E706"),sQuery(id+"F0.wireOp",EDGE,"E707"),sQuery(id+"F0.wireOp",EDGE,"E708"),sQuery(id+"F0.wireOp",EDGE,"E709"),sQuery(id+"F0.wireOp",EDGE,"E710"),sQuery(id+"F0.wireOp",EDGE,"E711"),sQuery(id+"F0.wireOp",EDGE,"E712"),sQuery(id+"F0.wireOp",EDGE,"E713"),sQuery(id+"F0.wireOp",EDGE,"E714"),sQuery(id+"F0.wireOp",EDGE,"E715"),sQuery(id+"F0.wireOp",EDGE,"E716"),sQuery(id+"F0.wireOp",EDGE,"E717"),sQuery(id+"F0.wireOp",EDGE,"E718"),sQuery(id+"F0.wireOp",EDGE,"E719"),sQuery(id+"F0.wireOp",EDGE,"E720"),sQuery(id+"F0.wireOp",EDGE,"E721"),sQuery(id+"F0.wireOp",EDGE,"E722"),sQuery(id+"F0.wireOp",EDGE,"E723"),sQuery(id+"F0.wireOp",EDGE,"E724"),sQuery(id+"F0.wireOp",EDGE,"E725"),sQuery(id+"F0.wireOp",EDGE,"E726"),sQuery(id+"F0.wireOp",EDGE,"E727"),sQuery(id+"F0.wireOp",EDGE,"E728"),sQuery(id+"F0.wireOp",EDGE,"E729"),sQuery(id+"F0.wireOp",EDGE,"E730"),sQuery(id+"F0.wireOp",EDGE,"E731"),sQuery(id+"F0.wireOp",EDGE,"E732"),sQuery(id+"F0.wireOp",EDGE,"E733"),sQuery(id+"F0.wireOp",EDGE,"E734"),sQuery(id+"F0.wireOp",EDGE,"E735"),sQuery(id+"F0.wireOp",EDGE,"E736"),sQuery(id+"F0.wireOp",EDGE,"E737"),sQuery(id+"F0.wireOp",EDGE,"E738"),sQuery(id+"F0.wireOp",EDGE,"E739"),sQuery(id+"F0.wireOp",EDGE,"E740"),sQuery(id+"F0.wireOp",EDGE,"E741"),sQuery(id+"F0.wireOp",EDGE,"E742"),sQuery(id+"F0.wireOp",EDGE,"E743"),sQuery(id+"F0.wireOp",EDGE,"E744"),sQuery(id+"F0.wireOp",EDGE,"E745"),sQuery(id+"F0.wireOp",EDGE,"E746"),sQuery(id+"F0.wireOp",EDGE,"E747"),sQuery(id+"F0.wireOp",EDGE,"E748"),sQuery(id+"F0.wireOp",EDGE,"E749"),sQuery(id+"F0.wireOp",EDGE,"E750"),sQuery(id+"F0.wireOp",EDGE,"E751"),sQuery(id+"F0.wireOp",EDGE,"E752"),sQuery(id+"F0.wireOp",EDGE,"E753"),sQuery(id+"F0.wireOp",EDGE,"E754"),sQuery(id+"F0.wireOp",EDGE,"E755"),sQuery(id+"F0.wireOp",EDGE,"E756"),sQuery(id+"F0.wireOp",EDGE,"E757"),sQuery(id+"F0.wireOp",EDGE,"E758"),sQuery(id+"F0.wireOp",EDGE,"E759"),sQuery(id+"F0.wireOp",EDGE,"E760"),sQuery(id+"F0.wireOp",EDGE,"E761"),sQuery(id+"F0.wireOp",EDGE,"E762"),sQuery(id+"F0.wireOp",EDGE,"E763"),sQuery(id+"F0.wireOp",EDGE,"E764"),sQuery(id+"F0.wireOp",EDGE,"E765"),sQuery(id+"F0.wireOp",EDGE,"E766"),sQuery(id+"F0.wireOp",EDGE,"E767"),sQuery(id+"F0.wireOp",EDGE,"E768"),sQuery(id+"F0.wireOp",EDGE,"E769"),sQuery(id+"F0.wireOp",EDGE,"E769"),sQuery(id+"F0.wireOp",EDGE,"E770"),sQuery(id+"F0.wireOp",EDGE,"E771"),sQuery(id+"F0.wireOp",EDGE,"E772"),sQuery(id+"F0.wireOp",EDGE,"E773"),sQuery(id+"F0.wireOp",EDGE,"E774"),sQuery(id+"F0.wireOp",EDGE,"E775"),sQuery(id+"F0.wireOp",EDGE,"E776"),sQuery(id+"F0.wireOp",EDGE,"E777"),sQuery(id+"F0.wireOp",EDGE,"E778"),sQuery(id+"F0.wireOp",EDGE,"E779"),sQuery(id+"F0.wireOp",EDGE,"E780"),sQuery(id+"F0.wireOp",EDGE,"E781"),sQuery(id+"F0.wireOp",EDGE,"E782"),sQuery(id+"F0.wireOp",EDGE,"E783"),sQuery(id+"F0.wireOp",EDGE,"E784"),sQuery(id+"F0.wireOp",EDGE,"E785"),sQuery(id+"F0.wireOp",EDGE,"E786"),sQuery(id+"F0.wireOp",EDGE,"E787"),sQuery(id+"F0.wireOp",EDGE,"E788"),sQuery(id+"F0.wireOp",EDGE,"E789"),sQuery(id+"F0.wireOp",EDGE,"E790"),sQuery(id+"F0.wireOp",EDGE,"E791"),sQuery(id+"F0.wireOp",EDGE,"E792"),sQuery(id+"F0.wireOp",EDGE,"E793"),sQuery(id+"F0.wireOp",EDGE,"E794"),sQuery(id+"F0.wireOp",EDGE,"E795"),sQuery(id+"F0.wireOp",EDGE,"E796"),sQuery(id+"F0.wireOp",EDGE,"E797"),sQuery(id+"F0.wireOp",EDGE,"E798"),sQuery(id+"F0.wireOp",EDGE,"E799"),sQuery(id+"F0.wireOp",EDGE,"E800"),sQuery(id+"F0.wireOp",EDGE,"E801"),sQuery(id+"F0.wireOp",EDGE,"E802"),sQuery(id+"F0.wireOp",EDGE,"E803"),sQuery(id+"F0.wireOp",EDGE,"E804"),sQuery(id+"F0.wireOp",EDGE,"E805"),sQuery(id+"F0.wireOp",EDGE,"E806"),sQuery(id+"F0.wireOp",EDGE,"E807"),sQuery(id+"F0.wireOp",EDGE,"E808"),sQuery(id+"F0.wireOp",EDGE,"E809"),sQuery(id+"F0.wireOp",EDGE,"E809"),sQuery(id+"F0.wireOp",EDGE,"E810"),sQuery(id+"F0.wireOp",EDGE,"E811"),sQuery(id+"F0.wireOp",EDGE,"E812"),sQuery(id+"F0.wireOp",EDGE,"E813"),sQuery(id+"F0.wireOp",EDGE,"E814"),sQuery(id+"F0.wireOp",EDGE,"E815"),sQuery(id+"F0.wireOp",EDGE,"E816"),sQuery(id+"F0.wireOp",EDGE,"E817"),sQuery(id+"F0.wireOp",EDGE,"E818"),sQuery(id+"F0.wireOp",EDGE,"E819"),sQuery(id+"F0.wireOp",EDGE,"E820"),sQuery(id+"F0.wireOp",EDGE,"E821"),sQuery(id+"F0.wireOp",EDGE,"E822"),sQuery(id+"F0.wireOp",EDGE,"E823"),sQuery(id+"F0.wireOp",EDGE,"E824"),sQuery(id+"F0.wireOp",EDGE,"E825"),sQuery(id+"F0.wireOp",EDGE,"E826"),sQuery(id+"F0.wireOp",EDGE,"E827"),sQuery(id+"F0.wireOp",EDGE,"E828"),sQuery(id+"F0.wireOp",EDGE,"E829"),sQuery(id+"F0.wireOp",EDGE,"E830"),sQuery(id+"F0.wireOp",EDGE,"E831"),sQuery(id+"F0.wireOp",EDGE,"E832"),sQuery(id+"F0.wireOp",EDGE,"E833"),sQuery(id+"F0.wireOp",EDGE,"E834"),sQuery(id+"F0.wireOp",EDGE,"E835"),sQuery(id+"F0.wireOp",EDGE,"E836"),sQuery(id+"F0.wireOp",EDGE,"E837"),sQuery(id+"F0.wireOp",EDGE,"E838"),sQuery(id+"F0.wireOp",EDGE,"E839"),sQuery(id+"F0.wireOp",EDGE,"E840"),sQuery(id+"F0.wireOp",EDGE,"E841"),sQuery(id+"F0.wireOp",EDGE,"E842"),sQuery(id+"F0.wireOp",EDGE,"E843"),sQuery(id+"F0.wireOp",EDGE,"E844"),sQuery(id+"F0.wireOp",EDGE,"E845"),sQuery(id+"F0.wireOp",EDGE,"E846"),sQuery(id+"F0.wireOp",EDGE,"E847"),sQuery(id+"F0.wireOp",EDGE,"E848"),sQuery(id+"F0.wireOp",EDGE,"E849"),sQuery(id+"F0.wireOp",EDGE,"E850"),sQuery(id+"F0.wireOp",EDGE,"E851"),sQuery(id+"F0.wireOp",EDGE,"E852"),sQuery(id+"F0.wireOp",EDGE,"E852"),sQuery(id+"F0.wireOp",EDGE,"E852"),sQuery(id+"F0.wireOp",EDGE,"E852"),sQuery(id+"F0.wireOp",EDGE,"E852"),sQuery(id+"F0.wireOp",EDGE,"E853"),sQuery(id+"F0.wireOp",EDGE,"E854"),sQuery(id+"F0.wireOp",EDGE,"E855"),sQuery(id+"F0.wireOp",EDGE,"E856"),sQuery(id+"F0.wireOp",EDGE,"E857"),sQuery(id+"F0.wireOp",EDGE,"E858"),sQuery(id+"F0.wireOp",EDGE,"E859"),sQuery(id+"F0.wireOp",EDGE,"E860"),sQuery(id+"F0.wireOp",EDGE,"E861"),sQuery(id+"F0.wireOp",EDGE,"E862"),sQuery(id+"F0.wireOp",EDGE,"E863"),sQuery(id+"F0.wireOp",EDGE,"E864"),sQuery(id+"F0.wireOp",EDGE,"E865"),sQuery(id+"F0.wireOp",EDGE,"E866"),sQuery(id+"F0.wireOp",EDGE,"E867"),sQuery(id+"F0.wireOp",EDGE,"E868"),sQuery(id+"F0.wireOp",EDGE,"E869"),sQuery(id+"F0.wireOp",EDGE,"E870"),sQuery(id+"F0.wireOp",EDGE,"E871"),sQuery(id+"F0.wireOp",EDGE,"E872"),sQuery(id+"F0.wireOp",EDGE,"E873"),sQuery(id+"F0.wireOp",EDGE,"E874"),sQuery(id+"F0.wireOp",EDGE,"E875"),sQuery(id+"F0.wireOp",EDGE,"E876"),sQuery(id+"F0.wireOp",EDGE,"E877"),sQuery(id+"F0.wireOp",EDGE,"E878"),sQuery(id+"F0.wireOp",EDGE,"E879"),sQuery(id+"F0.wireOp",EDGE,"E880"),sQuery(id+"F0.wireOp",EDGE,"E881"),sQuery(id+"F0.wireOp",EDGE,"E882"),sQuery(id+"F0.wireOp",EDGE,"E883"),sQuery(id+"F0.wireOp",EDGE,"E884"),sQuery(id+"F0.wireOp",EDGE,"E885"),sQuery(id+"F0.wireOp",EDGE,"E886"),sQuery(id+"F0.wireOp",EDGE,"E887"),sQuery(id+"F0.wireOp",EDGE,"E888"),sQuery(id+"F0.wireOp",EDGE,"E889"),sQuery(id+"F0.wireOp",EDGE,"E890")])],"isStart":false});
            var sketch = newSketch(context, id + "F2", { "sketchPlane" : qUnion([Q0])});
            skPoint(sketch, "E1012.0", {"position": v(-3271, 71.66) * mm});
            skLineSegment(sketch, "E1013.bottom", {"start": v(-3368.64, 71.66) * mm, "end": v(-3271, 71.66) * mm});
            skLineSegment(sketch, "E1013.top", {"start": v(-3368.64, 986.06) * mm, "end": v(-3271, 986.06) * mm});
            skLineSegment(sketch, "E1013.left", {"start": v(-3368.64, 71.66) * mm, "end": v(-3368.64, 986.06) * mm});
            skLineSegment(sketch, "E1013.right", {"start": v(-3271, 71.66) * mm, "end": v(-3271, 986.06) * mm});
            skSolve(sketch);
        }
        {
            var Q0;
            Q0 = qSketchRegion(id + "F2", true);
            var Q1;
            Q1=makeQuery(id+"F1.opExtrude","CAP_FACE",FACE,{"disambiguationData":[OSD([sQuery(id+"F0.wireOp",EDGE,"E0"),sQuery(id+"F0.wireOp",EDGE,"E1"),sQuery(id+"F0.wireOp",EDGE,"E2"),sQuery(id+"F0.wireOp",EDGE,"E3"),sQuery(id+"F0.wireOp",EDGE,"E4"),sQuery(id+"F0.wireOp",EDGE,"E5"),sQuery(id+"F0.wireOp",EDGE,"E6"),sQuery(id+"F0.wireOp",EDGE,"E7"),sQuery(id+"F0.wireOp",EDGE,"E8"),sQuery(id+"F0.wireOp",EDGE,"E9"),sQuery(id+"F0.wireOp",EDGE,"E10"),sQuery(id+"F0.wireOp",EDGE,"E11"),sQuery(id+"F0.wireOp",EDGE,"E12"),sQuery(id+"F0.wireOp",EDGE,"E13"),sQuery(id+"F0.wireOp",EDGE,"E14"),sQuery(id+"F0.wireOp",EDGE,"E15"),sQuery(id+"F0.wireOp",EDGE,"E16"),sQuery(id+"F0.wireOp",EDGE,"E17"),sQuery(id+"F0.wireOp",EDGE,"E18"),sQuery(id+"F0.wireOp",EDGE,"E19"),sQuery(id+"F0.wireOp",EDGE,"E20"),sQuery(id+"F0.wireOp",EDGE,"E21"),sQuery(id+"F0.wireOp",EDGE,"E22"),sQuery(id+"F0.wireOp",EDGE,"E23"),sQuery(id+"F0.wireOp",EDGE,"E24"),sQuery(id+"F0.wireOp",EDGE,"E25"),sQuery(id+"F0.wireOp",EDGE,"E26"),sQuery(id+"F0.wireOp",EDGE,"E27"),sQuery(id+"F0.wireOp",EDGE,"E28"),sQuery(id+"F0.wireOp",EDGE,"E29"),sQuery(id+"F0.wireOp",EDGE,"E30"),sQuery(id+"F0.wireOp",EDGE,"E31"),sQuery(id+"F0.wireOp",EDGE,"E32"),sQuery(id+"F0.wireOp",EDGE,"E33"),sQuery(id+"F0.wireOp",EDGE,"E34"),sQuery(id+"F0.wireOp",EDGE,"E35"),sQuery(id+"F0.wireOp",EDGE,"E36"),sQuery(id+"F0.wireOp",EDGE,"E37"),sQuery(id+"F0.wireOp",EDGE,"E38"),sQuery(id+"F0.wireOp",EDGE,"E39"),sQuery(id+"F0.wireOp",EDGE,"E40"),sQuery(id+"F0.wireOp",EDGE,"E41"),sQuery(id+"F0.wireOp",EDGE,"E42"),sQuery(id+"F0.wireOp",EDGE,"E43"),sQuery(id+"F0.wireOp",EDGE,"E44"),sQuery(id+"F0.wireOp",EDGE,"E45"),sQuery(id+"F0.wireOp",EDGE,"E46"),sQuery(id+"F0.wireOp",EDGE,"E47"),sQuery(id+"F0.wireOp",EDGE,"E48"),sQuery(id+"F0.wireOp",EDGE,"E49"),sQuery(id+"F0.wireOp",EDGE,"E50"),sQuery(id+"F0.wireOp",EDGE,"E51"),sQuery(id+"F0.wireOp",EDGE,"E52"),sQuery(id+"F0.wireOp",EDGE,"E53"),sQuery(id+"F0.wireOp",EDGE,"E54"),sQuery(id+"F0.wireOp",EDGE,"E55"),sQuery(id+"F0.wireOp",EDGE,"E56"),sQuery(id+"F0.wireOp",EDGE,"E57"),sQuery(id+"F0.wireOp",EDGE,"E58"),sQuery(id+"F0.wireOp",EDGE,"E59"),sQuery(id+"F0.wireOp",EDGE,"E60"),sQuery(id+"F0.wireOp",EDGE,"E61"),sQuery(id+"F0.wireOp",EDGE,"E62"),sQuery(id+"F0.wireOp",EDGE,"E63"),sQuery(id+"F0.wireOp",EDGE,"E64"),sQuery(id+"F0.wireOp",EDGE,"E65"),sQuery(id+"F0.wireOp",EDGE,"E66"),sQuery(id+"F0.wireOp",EDGE,"E67"),sQuery(id+"F0.wireOp",EDGE,"E68"),sQuery(id+"F0.wireOp",EDGE,"E69"),sQuery(id+"F0.wireOp",EDGE,"E70"),sQuery(id+"F0.wireOp",EDGE,"E71"),sQuery(id+"F0.wireOp",EDGE,"E72"),sQuery(id+"F0.wireOp",EDGE,"E73"),sQuery(id+"F0.wireOp",EDGE,"E74"),sQuery(id+"F0.wireOp",EDGE,"E75"),sQuery(id+"F0.wireOp",EDGE,"E76"),sQuery(id+"F0.wireOp",EDGE,"E77"),sQuery(id+"F0.wireOp",EDGE,"E78"),sQuery(id+"F0.wireOp",EDGE,"E79"),sQuery(id+"F0.wireOp",EDGE,"E80"),sQuery(id+"F0.wireOp",EDGE,"E81"),sQuery(id+"F0.wireOp",EDGE,"E82"),sQuery(id+"F0.wireOp",EDGE,"E83"),sQuery(id+"F0.wireOp",EDGE,"E84"),sQuery(id+"F0.wireOp",EDGE,"E85"),sQuery(id+"F0.wireOp",EDGE,"E86"),sQuery(id+"F0.wireOp",EDGE,"E87"),sQuery(id+"F0.wireOp",EDGE,"E88"),sQuery(id+"F0.wireOp",EDGE,"E89"),sQuery(id+"F0.wireOp",EDGE,"E90"),sQuery(id+"F0.wireOp",EDGE,"E91"),sQuery(id+"F0.wireOp",EDGE,"E92"),sQuery(id+"F0.wireOp",EDGE,"E93"),sQuery(id+"F0.wireOp",EDGE,"E94"),sQuery(id+"F0.wireOp",EDGE,"E95"),sQuery(id+"F0.wireOp",EDGE,"E96"),sQuery(id+"F0.wireOp",EDGE,"E97"),sQuery(id+"F0.wireOp",EDGE,"E98"),sQuery(id+"F0.wireOp",EDGE,"E99"),sQuery(id+"F0.wireOp",EDGE,"E100"),sQuery(id+"F0.wireOp",EDGE,"E101"),sQuery(id+"F0.wireOp",EDGE,"E102"),sQuery(id+"F0.wireOp",EDGE,"E103"),sQuery(id+"F0.wireOp",EDGE,"E104"),sQuery(id+"F0.wireOp",EDGE,"E105"),sQuery(id+"F0.wireOp",EDGE,"E106"),sQuery(id+"F0.wireOp",EDGE,"E107"),sQuery(id+"F0.wireOp",EDGE,"E108"),sQuery(id+"F0.wireOp",EDGE,"E109"),sQuery(id+"F0.wireOp",EDGE,"E110"),sQuery(id+"F0.wireOp",EDGE,"E111"),sQuery(id+"F0.wireOp",EDGE,"E112"),sQuery(id+"F0.wireOp",EDGE,"E113"),sQuery(id+"F0.wireOp",EDGE,"E114"),sQuery(id+"F0.wireOp",EDGE,"E115"),sQuery(id+"F0.wireOp",EDGE,"E116"),sQuery(id+"F0.wireOp",EDGE,"E117"),sQuery(id+"F0.wireOp",EDGE,"E118"),sQuery(id+"F0.wireOp",EDGE,"E119"),sQuery(id+"F0.wireOp",EDGE,"E120"),sQuery(id+"F0.wireOp",EDGE,"E121"),sQuery(id+"F0.wireOp",EDGE,"E122"),sQuery(id+"F0.wireOp",EDGE,"E123"),sQuery(id+"F0.wireOp",EDGE,"E124"),sQuery(id+"F0.wireOp",EDGE,"E125"),sQuery(id+"F0.wireOp",EDGE,"E126"),sQuery(id+"F0.wireOp",EDGE,"E127"),sQuery(id+"F0.wireOp",EDGE,"E128"),sQuery(id+"F0.wireOp",EDGE,"E129"),sQuery(id+"F0.wireOp",EDGE,"E130"),sQuery(id+"F0.wireOp",EDGE,"E131"),sQuery(id+"F0.wireOp",EDGE,"E132"),sQuery(id+"F0.wireOp",EDGE,"E133"),sQuery(id+"F0.wireOp",EDGE,"E134"),sQuery(id+"F0.wireOp",EDGE,"E135"),sQuery(id+"F0.wireOp",EDGE,"E136"),sQuery(id+"F0.wireOp",EDGE,"E137"),sQuery(id+"F0.wireOp",EDGE,"E138"),sQuery(id+"F0.wireOp",EDGE,"E139"),sQuery(id+"F0.wireOp",EDGE,"E140"),sQuery(id+"F0.wireOp",EDGE,"E141"),sQuery(id+"F0.wireOp",EDGE,"E142"),sQuery(id+"F0.wireOp",EDGE,"E143"),sQuery(id+"F0.wireOp",EDGE,"E144"),sQuery(id+"F0.wireOp",EDGE,"E145"),sQuery(id+"F0.wireOp",EDGE,"E146"),sQuery(id+"F0.wireOp",EDGE,"E147"),sQuery(id+"F0.wireOp",EDGE,"E148"),sQuery(id+"F0.wireOp",EDGE,"E149"),sQuery(id+"F0.wireOp",EDGE,"E150"),sQuery(id+"F0.wireOp",EDGE,"E151"),sQuery(id+"F0.wireOp",EDGE,"E152"),sQuery(id+"F0.wireOp",EDGE,"E153"),sQuery(id+"F0.wireOp",EDGE,"E154"),sQuery(id+"F0.wireOp",EDGE,"E155"),sQuery(id+"F0.wireOp",EDGE,"E156"),sQuery(id+"F0.wireOp",EDGE,"E157"),sQuery(id+"F0.wireOp",EDGE,"E158"),sQuery(id+"F0.wireOp",EDGE,"E159"),sQuery(id+"F0.wireOp",EDGE,"E160"),sQuery(id+"F0.wireOp",EDGE,"E161"),sQuery(id+"F0.wireOp",EDGE,"E162"),sQuery(id+"F0.wireOp",EDGE,"E163"),sQuery(id+"F0.wireOp",EDGE,"E163"),sQuery(id+"F0.wireOp",EDGE,"E164"),sQuery(id+"F0.wireOp",EDGE,"E165"),sQuery(id+"F0.wireOp",EDGE,"E166"),sQuery(id+"F0.wireOp",EDGE,"E167"),sQuery(id+"F0.wireOp",EDGE,"E168"),sQuery(id+"F0.wireOp",EDGE,"E169"),sQuery(id+"F0.wireOp",EDGE,"E170"),sQuery(id+"F0.wireOp",EDGE,"E171"),sQuery(id+"F0.wireOp",EDGE,"E171"),sQuery(id+"F0.wireOp",EDGE,"E172"),sQuery(id+"F0.wireOp",EDGE,"E173"),sQuery(id+"F0.wireOp",EDGE,"E174"),sQuery(id+"F0.wireOp",EDGE,"E174"),sQuery(id+"F0.wireOp",EDGE,"E174"),sQuery(id+"F0.wireOp",EDGE,"E175"),sQuery(id+"F0.wireOp",EDGE,"E176"),sQuery(id+"F0.wireOp",EDGE,"E176"),sQuery(id+"F0.wireOp",EDGE,"E177"),sQuery(id+"F0.wireOp",EDGE,"E178"),sQuery(id+"F0.wireOp",EDGE,"E178"),sQuery(id+"F0.wireOp",EDGE,"E179"),sQuery(id+"F0.wireOp",EDGE,"E180"),sQuery(id+"F0.wireOp",EDGE,"E181"),sQuery(id+"F0.wireOp",EDGE,"E182"),sQuery(id+"F0.wireOp",EDGE,"E183"),sQuery(id+"F0.wireOp",EDGE,"E184"),sQuery(id+"F0.wireOp",EDGE,"E185"),sQuery(id+"F0.wireOp",EDGE,"E186"),sQuery(id+"F0.wireOp",EDGE,"E187"),sQuery(id+"F0.wireOp",EDGE,"E188"),sQuery(id+"F0.wireOp",EDGE,"E189"),sQuery(id+"F0.wireOp",EDGE,"E190"),sQuery(id+"F0.wireOp",EDGE,"E191"),sQuery(id+"F0.wireOp",EDGE,"E192"),sQuery(id+"F0.wireOp",EDGE,"E193"),sQuery(id+"F0.wireOp",EDGE,"E194"),sQuery(id+"F0.wireOp",EDGE,"E195"),sQuery(id+"F0.wireOp",EDGE,"E196"),sQuery(id+"F0.wireOp",EDGE,"E197"),sQuery(id+"F0.wireOp",EDGE,"E198"),sQuery(id+"F0.wireOp",EDGE,"E199"),sQuery(id+"F0.wireOp",EDGE,"E200"),sQuery(id+"F0.wireOp",EDGE,"E201"),sQuery(id+"F0.wireOp",EDGE,"E202"),sQuery(id+"F0.wireOp",EDGE,"E203"),sQuery(id+"F0.wireOp",EDGE,"E204"),sQuery(id+"F0.wireOp",EDGE,"E205"),sQuery(id+"F0.wireOp",EDGE,"E206"),sQuery(id+"F0.wireOp",EDGE,"E207"),sQuery(id+"F0.wireOp",EDGE,"E208"),sQuery(id+"F0.wireOp",EDGE,"E209"),sQuery(id+"F0.wireOp",EDGE,"E210"),sQuery(id+"F0.wireOp",EDGE,"E211"),sQuery(id+"F0.wireOp",EDGE,"E212"),sQuery(id+"F0.wireOp",EDGE,"E213"),sQuery(id+"F0.wireOp",EDGE,"E214"),sQuery(id+"F0.wireOp",EDGE,"E215"),sQuery(id+"F0.wireOp",EDGE,"E216"),sQuery(id+"F0.wireOp",EDGE,"E217"),sQuery(id+"F0.wireOp",EDGE,"E218"),sQuery(id+"F0.wireOp",EDGE,"E219"),sQuery(id+"F0.wireOp",EDGE,"E220"),sQuery(id+"F0.wireOp",EDGE,"E221"),sQuery(id+"F0.wireOp",EDGE,"E222"),sQuery(id+"F0.wireOp",EDGE,"E223"),sQuery(id+"F0.wireOp",EDGE,"E224"),sQuery(id+"F0.wireOp",EDGE,"E225"),sQuery(id+"F0.wireOp",EDGE,"E226"),sQuery(id+"F0.wireOp",EDGE,"E227"),sQuery(id+"F0.wireOp",EDGE,"E228"),sQuery(id+"F0.wireOp",EDGE,"E229"),sQuery(id+"F0.wireOp",EDGE,"E230"),sQuery(id+"F0.wireOp",EDGE,"E231"),sQuery(id+"F0.wireOp",EDGE,"E232"),sQuery(id+"F0.wireOp",EDGE,"E233"),sQuery(id+"F0.wireOp",EDGE,"E234"),sQuery(id+"F0.wireOp",EDGE,"E235"),sQuery(id+"F0.wireOp",EDGE,"E236"),sQuery(id+"F0.wireOp",EDGE,"E237"),sQuery(id+"F0.wireOp",EDGE,"E238"),sQuery(id+"F0.wireOp",EDGE,"E239"),sQuery(id+"F0.wireOp",EDGE,"E240"),sQuery(id+"F0.wireOp",EDGE,"E241"),sQuery(id+"F0.wireOp",EDGE,"E242"),sQuery(id+"F0.wireOp",EDGE,"E243"),sQuery(id+"F0.wireOp",EDGE,"E244"),sQuery(id+"F0.wireOp",EDGE,"E245"),sQuery(id+"F0.wireOp",EDGE,"E246"),sQuery(id+"F0.wireOp",EDGE,"E247"),sQuery(id+"F0.wireOp",EDGE,"E248"),sQuery(id+"F0.wireOp",EDGE,"E249"),sQuery(id+"F0.wireOp",EDGE,"E250"),sQuery(id+"F0.wireOp",EDGE,"E251"),sQuery(id+"F0.wireOp",EDGE,"E252"),sQuery(id+"F0.wireOp",EDGE,"E253"),sQuery(id+"F0.wireOp",EDGE,"E254"),sQuery(id+"F0.wireOp",EDGE,"E255"),sQuery(id+"F0.wireOp",EDGE,"E256"),sQuery(id+"F0.wireOp",EDGE,"E257"),sQuery(id+"F0.wireOp",EDGE,"E258"),sQuery(id+"F0.wireOp",EDGE,"E259"),sQuery(id+"F0.wireOp",EDGE,"E260"),sQuery(id+"F0.wireOp",EDGE,"E261"),sQuery(id+"F0.wireOp",EDGE,"E262"),sQuery(id+"F0.wireOp",EDGE,"E263"),sQuery(id+"F0.wireOp",EDGE,"E264"),sQuery(id+"F0.wireOp",EDGE,"E265"),sQuery(id+"F0.wireOp",EDGE,"E266"),sQuery(id+"F0.wireOp",EDGE,"E267"),sQuery(id+"F0.wireOp",EDGE,"E268"),sQuery(id+"F0.wireOp",EDGE,"E269"),sQuery(id+"F0.wireOp",EDGE,"E270"),sQuery(id+"F0.wireOp",EDGE,"E271"),sQuery(id+"F0.wireOp",EDGE,"E272"),sQuery(id+"F0.wireOp",EDGE,"E273"),sQuery(id+"F0.wireOp",EDGE,"E274"),sQuery(id+"F0.wireOp",EDGE,"E275"),sQuery(id+"F0.wireOp",EDGE,"E276"),sQuery(id+"F0.wireOp",EDGE,"E277"),sQuery(id+"F0.wireOp",EDGE,"E278"),sQuery(id+"F0.wireOp",EDGE,"E279"),sQuery(id+"F0.wireOp",EDGE,"E280"),sQuery(id+"F0.wireOp",EDGE,"E281"),sQuery(id+"F0.wireOp",EDGE,"E282"),sQuery(id+"F0.wireOp",EDGE,"E283"),sQuery(id+"F0.wireOp",EDGE,"E284"),sQuery(id+"F0.wireOp",EDGE,"E285"),sQuery(id+"F0.wireOp",EDGE,"E286"),sQuery(id+"F0.wireOp",EDGE,"E287"),sQuery(id+"F0.wireOp",EDGE,"E288"),sQuery(id+"F0.wireOp",EDGE,"E289"),sQuery(id+"F0.wireOp",EDGE,"E290"),sQuery(id+"F0.wireOp",EDGE,"E291"),sQuery(id+"F0.wireOp",EDGE,"E292"),sQuery(id+"F0.wireOp",EDGE,"E293"),sQuery(id+"F0.wireOp",EDGE,"E294"),sQuery(id+"F0.wireOp",EDGE,"E295"),sQuery(id+"F0.wireOp",EDGE,"E296"),sQuery(id+"F0.wireOp",EDGE,"E297"),sQuery(id+"F0.wireOp",EDGE,"E297"),sQuery(id+"F0.wireOp",EDGE,"E298"),sQuery(id+"F0.wireOp",EDGE,"E299"),sQuery(id+"F0.wireOp",EDGE,"E300"),sQuery(id+"F0.wireOp",EDGE,"E301"),sQuery(id+"F0.wireOp",EDGE,"E302"),sQuery(id+"F0.wireOp",EDGE,"E303"),sQuery(id+"F0.wireOp",EDGE,"E304"),sQuery(id+"F0.wireOp",EDGE,"E305"),sQuery(id+"F0.wireOp",EDGE,"E306"),sQuery(id+"F0.wireOp",EDGE,"E307"),sQuery(id+"F0.wireOp",EDGE,"E308"),sQuery(id+"F0.wireOp",EDGE,"E309"),sQuery(id+"F0.wireOp",EDGE,"E310"),sQuery(id+"F0.wireOp",EDGE,"E311"),sQuery(id+"F0.wireOp",EDGE,"E312"),sQuery(id+"F0.wireOp",EDGE,"E313"),sQuery(id+"F0.wireOp",EDGE,"E314"),sQuery(id+"F0.wireOp",EDGE,"E315"),sQuery(id+"F0.wireOp",EDGE,"E316"),sQuery(id+"F0.wireOp",EDGE,"E317"),sQuery(id+"F0.wireOp",EDGE,"E318"),sQuery(id+"F0.wireOp",EDGE,"E319"),sQuery(id+"F0.wireOp",EDGE,"E320"),sQuery(id+"F0.wireOp",EDGE,"E321"),sQuery(id+"F0.wireOp",EDGE,"E322"),sQuery(id+"F0.wireOp",EDGE,"E323"),sQuery(id+"F0.wireOp",EDGE,"E324"),sQuery(id+"F0.wireOp",EDGE,"E325"),sQuery(id+"F0.wireOp",EDGE,"E326"),sQuery(id+"F0.wireOp",EDGE,"E327"),sQuery(id+"F0.wireOp",EDGE,"E328"),sQuery(id+"F0.wireOp",EDGE,"E329"),sQuery(id+"F0.wireOp",EDGE,"E330"),sQuery(id+"F0.wireOp",EDGE,"E331"),sQuery(id+"F0.wireOp",EDGE,"E332"),sQuery(id+"F0.wireOp",EDGE,"E333"),sQuery(id+"F0.wireOp",EDGE,"E334"),sQuery(id+"F0.wireOp",EDGE,"E335"),sQuery(id+"F0.wireOp",EDGE,"E336"),sQuery(id+"F0.wireOp",EDGE,"E337"),sQuery(id+"F0.wireOp",EDGE,"E338"),sQuery(id+"F0.wireOp",EDGE,"E339"),sQuery(id+"F0.wireOp",EDGE,"E340"),sQuery(id+"F0.wireOp",EDGE,"E341"),sQuery(id+"F0.wireOp",EDGE,"E342"),sQuery(id+"F0.wireOp",EDGE,"E343"),sQuery(id+"F0.wireOp",EDGE,"E344"),sQuery(id+"F0.wireOp",EDGE,"E345"),sQuery(id+"F0.wireOp",EDGE,"E346"),sQuery(id+"F0.wireOp",EDGE,"E347"),sQuery(id+"F0.wireOp",EDGE,"E348"),sQuery(id+"F0.wireOp",EDGE,"E349"),sQuery(id+"F0.wireOp",EDGE,"E350"),sQuery(id+"F0.wireOp",EDGE,"E351"),sQuery(id+"F0.wireOp",EDGE,"E352"),sQuery(id+"F0.wireOp",EDGE,"E353"),sQuery(id+"F0.wireOp",EDGE,"E354"),sQuery(id+"F0.wireOp",EDGE,"E355"),sQuery(id+"F0.wireOp",EDGE,"E356"),sQuery(id+"F0.wireOp",EDGE,"E357"),sQuery(id+"F0.wireOp",EDGE,"E358"),sQuery(id+"F0.wireOp",EDGE,"E359"),sQuery(id+"F0.wireOp",EDGE,"E360"),sQuery(id+"F0.wireOp",EDGE,"E361"),sQuery(id+"F0.wireOp",EDGE,"E362"),sQuery(id+"F0.wireOp",EDGE,"E363"),sQuery(id+"F0.wireOp",EDGE,"E364"),sQuery(id+"F0.wireOp",EDGE,"E365"),sQuery(id+"F0.wireOp",EDGE,"E366"),sQuery(id+"F0.wireOp",EDGE,"E367"),sQuery(id+"F0.wireOp",EDGE,"E368"),sQuery(id+"F0.wireOp",EDGE,"E369"),sQuery(id+"F0.wireOp",EDGE,"E370"),sQuery(id+"F0.wireOp",EDGE,"E371"),sQuery(id+"F0.wireOp",EDGE,"E372"),sQuery(id+"F0.wireOp",EDGE,"E373"),sQuery(id+"F0.wireOp",EDGE,"E374"),sQuery(id+"F0.wireOp",EDGE,"E375"),sQuery(id+"F0.wireOp",EDGE,"E376"),sQuery(id+"F0.wireOp",EDGE,"E377"),sQuery(id+"F0.wireOp",EDGE,"E378"),sQuery(id+"F0.wireOp",EDGE,"E379"),sQuery(id+"F0.wireOp",EDGE,"E380"),sQuery(id+"F0.wireOp",EDGE,"E381"),sQuery(id+"F0.wireOp",EDGE,"E382"),sQuery(id+"F0.wireOp",EDGE,"E383"),sQuery(id+"F0.wireOp",EDGE,"E384"),sQuery(id+"F0.wireOp",EDGE,"E385"),sQuery(id+"F0.wireOp",EDGE,"E386"),sQuery(id+"F0.wireOp",EDGE,"E387"),sQuery(id+"F0.wireOp",EDGE,"E388"),sQuery(id+"F0.wireOp",EDGE,"E389"),sQuery(id+"F0.wireOp",EDGE,"E390"),sQuery(id+"F0.wireOp",EDGE,"E391"),sQuery(id+"F0.wireOp",EDGE,"E392"),sQuery(id+"F0.wireOp",EDGE,"E393"),sQuery(id+"F0.wireOp",EDGE,"E394"),sQuery(id+"F0.wireOp",EDGE,"E395"),sQuery(id+"F0.wireOp",EDGE,"E396"),sQuery(id+"F0.wireOp",EDGE,"E397"),sQuery(id+"F0.wireOp",EDGE,"E398"),sQuery(id+"F0.wireOp",EDGE,"E399"),sQuery(id+"F0.wireOp",EDGE,"E400"),sQuery(id+"F0.wireOp",EDGE,"E401"),sQuery(id+"F0.wireOp",EDGE,"E402"),sQuery(id+"F0.wireOp",EDGE,"E403"),sQuery(id+"F0.wireOp",EDGE,"E404"),sQuery(id+"F0.wireOp",EDGE,"E405"),sQuery(id+"F0.wireOp",EDGE,"E406"),sQuery(id+"F0.wireOp",EDGE,"E407"),sQuery(id+"F0.wireOp",EDGE,"E408"),sQuery(id+"F0.wireOp",EDGE,"E409"),sQuery(id+"F0.wireOp",EDGE,"E410"),sQuery(id+"F0.wireOp",EDGE,"E411"),sQuery(id+"F0.wireOp",EDGE,"E412"),sQuery(id+"F0.wireOp",EDGE,"E413"),sQuery(id+"F0.wireOp",EDGE,"E414"),sQuery(id+"F0.wireOp",EDGE,"E415"),sQuery(id+"F0.wireOp",EDGE,"E416"),sQuery(id+"F0.wireOp",EDGE,"E417"),sQuery(id+"F0.wireOp",EDGE,"E418"),sQuery(id+"F0.wireOp",EDGE,"E419"),sQuery(id+"F0.wireOp",EDGE,"E420"),sQuery(id+"F0.wireOp",EDGE,"E421"),sQuery(id+"F0.wireOp",EDGE,"E422"),sQuery(id+"F0.wireOp",EDGE,"E423"),sQuery(id+"F0.wireOp",EDGE,"E424"),sQuery(id+"F0.wireOp",EDGE,"E425"),sQuery(id+"F0.wireOp",EDGE,"E426"),sQuery(id+"F0.wireOp",EDGE,"E427"),sQuery(id+"F0.wireOp",EDGE,"E428"),sQuery(id+"F0.wireOp",EDGE,"E429"),sQuery(id+"F0.wireOp",EDGE,"E430"),sQuery(id+"F0.wireOp",EDGE,"E431"),sQuery(id+"F0.wireOp",EDGE,"E432"),sQuery(id+"F0.wireOp",EDGE,"E433"),sQuery(id+"F0.wireOp",EDGE,"E434"),sQuery(id+"F0.wireOp",EDGE,"E434"),sQuery(id+"F0.wireOp",EDGE,"E434"),sQuery(id+"F0.wireOp",EDGE,"E435"),sQuery(id+"F0.wireOp",EDGE,"E436"),sQuery(id+"F0.wireOp",EDGE,"E437"),sQuery(id+"F0.wireOp",EDGE,"E438"),sQuery(id+"F0.wireOp",EDGE,"E439"),sQuery(id+"F0.wireOp",EDGE,"E440"),sQuery(id+"F0.wireOp",EDGE,"E441"),sQuery(id+"F0.wireOp",EDGE,"E442"),sQuery(id+"F0.wireOp",EDGE,"E443"),sQuery(id+"F0.wireOp",EDGE,"E444"),sQuery(id+"F0.wireOp",EDGE,"E445"),sQuery(id+"F0.wireOp",EDGE,"E446"),sQuery(id+"F0.wireOp",EDGE,"E447"),sQuery(id+"F0.wireOp",EDGE,"E448"),sQuery(id+"F0.wireOp",EDGE,"E449"),sQuery(id+"F0.wireOp",EDGE,"E450"),sQuery(id+"F0.wireOp",EDGE,"E451"),sQuery(id+"F0.wireOp",EDGE,"E452"),sQuery(id+"F0.wireOp",EDGE,"E453"),sQuery(id+"F0.wireOp",EDGE,"E454"),sQuery(id+"F0.wireOp",EDGE,"E455"),sQuery(id+"F0.wireOp",EDGE,"E456"),sQuery(id+"F0.wireOp",EDGE,"E457"),sQuery(id+"F0.wireOp",EDGE,"E458"),sQuery(id+"F0.wireOp",EDGE,"E459"),sQuery(id+"F0.wireOp",EDGE,"E460"),sQuery(id+"F0.wireOp",EDGE,"E461"),sQuery(id+"F0.wireOp",EDGE,"E462"),sQuery(id+"F0.wireOp",EDGE,"E463"),sQuery(id+"F0.wireOp",EDGE,"E464"),sQuery(id+"F0.wireOp",EDGE,"E465"),sQuery(id+"F0.wireOp",EDGE,"E466"),sQuery(id+"F0.wireOp",EDGE,"E467"),sQuery(id+"F0.wireOp",EDGE,"E468"),sQuery(id+"F0.wireOp",EDGE,"E469"),sQuery(id+"F0.wireOp",EDGE,"E470"),sQuery(id+"F0.wireOp",EDGE,"E471"),sQuery(id+"F0.wireOp",EDGE,"E472"),sQuery(id+"F0.wireOp",EDGE,"E473"),sQuery(id+"F0.wireOp",EDGE,"E474"),sQuery(id+"F0.wireOp",EDGE,"E475"),sQuery(id+"F0.wireOp",EDGE,"E476"),sQuery(id+"F0.wireOp",EDGE,"E477"),sQuery(id+"F0.wireOp",EDGE,"E478"),sQuery(id+"F0.wireOp",EDGE,"E479"),sQuery(id+"F0.wireOp",EDGE,"E480"),sQuery(id+"F0.wireOp",EDGE,"E481"),sQuery(id+"F0.wireOp",EDGE,"E482"),sQuery(id+"F0.wireOp",EDGE,"E483"),sQuery(id+"F0.wireOp",EDGE,"E484"),sQuery(id+"F0.wireOp",EDGE,"E485"),sQuery(id+"F0.wireOp",EDGE,"E486"),sQuery(id+"F0.wireOp",EDGE,"E487"),sQuery(id+"F0.wireOp",EDGE,"E488"),sQuery(id+"F0.wireOp",EDGE,"E489"),sQuery(id+"F0.wireOp",EDGE,"E489"),sQuery(id+"F0.wireOp",EDGE,"E489"),sQuery(id+"F0.wireOp",EDGE,"E490"),sQuery(id+"F0.wireOp",EDGE,"E491"),sQuery(id+"F0.wireOp",EDGE,"E492"),sQuery(id+"F0.wireOp",EDGE,"E493"),sQuery(id+"F0.wireOp",EDGE,"E494"),sQuery(id+"F0.wireOp",EDGE,"E495"),sQuery(id+"F0.wireOp",EDGE,"E496"),sQuery(id+"F0.wireOp",EDGE,"E497"),sQuery(id+"F0.wireOp",EDGE,"E498"),sQuery(id+"F0.wireOp",EDGE,"E498"),sQuery(id+"F0.wireOp",EDGE,"E499"),sQuery(id+"F0.wireOp",EDGE,"E500"),sQuery(id+"F0.wireOp",EDGE,"E501"),sQuery(id+"F0.wireOp",EDGE,"E502"),sQuery(id+"F0.wireOp",EDGE,"E503"),sQuery(id+"F0.wireOp",EDGE,"E504"),sQuery(id+"F0.wireOp",EDGE,"E505"),sQuery(id+"F0.wireOp",EDGE,"E506"),sQuery(id+"F0.wireOp",EDGE,"E507"),sQuery(id+"F0.wireOp",EDGE,"E508"),sQuery(id+"F0.wireOp",EDGE,"E509"),sQuery(id+"F0.wireOp",EDGE,"E510"),sQuery(id+"F0.wireOp",EDGE,"E510"),sQuery(id+"F0.wireOp",EDGE,"E510"),sQuery(id+"F0.wireOp",EDGE,"E511"),sQuery(id+"F0.wireOp",EDGE,"E512"),sQuery(id+"F0.wireOp",EDGE,"E513"),sQuery(id+"F0.wireOp",EDGE,"E514"),sQuery(id+"F0.wireOp",EDGE,"E515"),sQuery(id+"F0.wireOp",EDGE,"E516"),sQuery(id+"F0.wireOp",EDGE,"E517"),sQuery(id+"F0.wireOp",EDGE,"E518"),sQuery(id+"F0.wireOp",EDGE,"E519"),sQuery(id+"F0.wireOp",EDGE,"E520"),sQuery(id+"F0.wireOp",EDGE,"E521"),sQuery(id+"F0.wireOp",EDGE,"E522"),sQuery(id+"F0.wireOp",EDGE,"E523"),sQuery(id+"F0.wireOp",EDGE,"E523"),sQuery(id+"F0.wireOp",EDGE,"E524"),sQuery(id+"F0.wireOp",EDGE,"E525"),sQuery(id+"F0.wireOp",EDGE,"E526"),sQuery(id+"F0.wireOp",EDGE,"E527"),sQuery(id+"F0.wireOp",EDGE,"E528"),sQuery(id+"F0.wireOp",EDGE,"E529"),sQuery(id+"F0.wireOp",EDGE,"E530"),sQuery(id+"F0.wireOp",EDGE,"E531"),sQuery(id+"F0.wireOp",EDGE,"E532"),sQuery(id+"F0.wireOp",EDGE,"E533"),sQuery(id+"F0.wireOp",EDGE,"E534"),sQuery(id+"F0.wireOp",EDGE,"E534"),sQuery(id+"F0.wireOp",EDGE,"E534"),sQuery(id+"F0.wireOp",EDGE,"E534"),sQuery(id+"F0.wireOp",EDGE,"E534"),sQuery(id+"F0.wireOp",EDGE,"E535"),sQuery(id+"F0.wireOp",EDGE,"E536"),sQuery(id+"F0.wireOp",EDGE,"E537"),sQuery(id+"F0.wireOp",EDGE,"E538"),sQuery(id+"F0.wireOp",EDGE,"E539"),sQuery(id+"F0.wireOp",EDGE,"E540"),sQuery(id+"F0.wireOp",EDGE,"E541"),sQuery(id+"F0.wireOp",EDGE,"E542"),sQuery(id+"F0.wireOp",EDGE,"E543"),sQuery(id+"F0.wireOp",EDGE,"E544"),sQuery(id+"F0.wireOp",EDGE,"E545"),sQuery(id+"F0.wireOp",EDGE,"E546"),sQuery(id+"F0.wireOp",EDGE,"E547"),sQuery(id+"F0.wireOp",EDGE,"E548"),sQuery(id+"F0.wireOp",EDGE,"E549"),sQuery(id+"F0.wireOp",EDGE,"E550"),sQuery(id+"F0.wireOp",EDGE,"E551"),sQuery(id+"F0.wireOp",EDGE,"E552"),sQuery(id+"F0.wireOp",EDGE,"E553"),sQuery(id+"F0.wireOp",EDGE,"E554"),sQuery(id+"F0.wireOp",EDGE,"E555"),sQuery(id+"F0.wireOp",EDGE,"E556"),sQuery(id+"F0.wireOp",EDGE,"E557"),sQuery(id+"F0.wireOp",EDGE,"E558"),sQuery(id+"F0.wireOp",EDGE,"E559"),sQuery(id+"F0.wireOp",EDGE,"E560"),sQuery(id+"F0.wireOp",EDGE,"E561"),sQuery(id+"F0.wireOp",EDGE,"E562"),sQuery(id+"F0.wireOp",EDGE,"E563"),sQuery(id+"F0.wireOp",EDGE,"E564"),sQuery(id+"F0.wireOp",EDGE,"E565"),sQuery(id+"F0.wireOp",EDGE,"E566"),sQuery(id+"F0.wireOp",EDGE,"E567"),sQuery(id+"F0.wireOp",EDGE,"E568"),sQuery(id+"F0.wireOp",EDGE,"E569"),sQuery(id+"F0.wireOp",EDGE,"E570"),sQuery(id+"F0.wireOp",EDGE,"E571"),sQuery(id+"F0.wireOp",EDGE,"E572"),sQuery(id+"F0.wireOp",EDGE,"E573"),sQuery(id+"F0.wireOp",EDGE,"E574"),sQuery(id+"F0.wireOp",EDGE,"E575"),sQuery(id+"F0.wireOp",EDGE,"E576"),sQuery(id+"F0.wireOp",EDGE,"E577"),sQuery(id+"F0.wireOp",EDGE,"E578"),sQuery(id+"F0.wireOp",EDGE,"E579"),sQuery(id+"F0.wireOp",EDGE,"E580"),sQuery(id+"F0.wireOp",EDGE,"E581"),sQuery(id+"F0.wireOp",EDGE,"E582"),sQuery(id+"F0.wireOp",EDGE,"E583"),sQuery(id+"F0.wireOp",EDGE,"E584"),sQuery(id+"F0.wireOp",EDGE,"E585"),sQuery(id+"F0.wireOp",EDGE,"E586"),sQuery(id+"F0.wireOp",EDGE,"E587"),sQuery(id+"F0.wireOp",EDGE,"E588"),sQuery(id+"F0.wireOp",EDGE,"E589"),sQuery(id+"F0.wireOp",EDGE,"E590"),sQuery(id+"F0.wireOp",EDGE,"E591"),sQuery(id+"F0.wireOp",EDGE,"E592"),sQuery(id+"F0.wireOp",EDGE,"E593"),sQuery(id+"F0.wireOp",EDGE,"E594"),sQuery(id+"F0.wireOp",EDGE,"E595"),sQuery(id+"F0.wireOp",EDGE,"E596"),sQuery(id+"F0.wireOp",EDGE,"E597"),sQuery(id+"F0.wireOp",EDGE,"E598"),sQuery(id+"F0.wireOp",EDGE,"E599"),sQuery(id+"F0.wireOp",EDGE,"E600"),sQuery(id+"F0.wireOp",EDGE,"E601"),sQuery(id+"F0.wireOp",EDGE,"E602"),sQuery(id+"F0.wireOp",EDGE,"E603"),sQuery(id+"F0.wireOp",EDGE,"E604"),sQuery(id+"F0.wireOp",EDGE,"E605"),sQuery(id+"F0.wireOp",EDGE,"E606"),sQuery(id+"F0.wireOp",EDGE,"E607"),sQuery(id+"F0.wireOp",EDGE,"E608"),sQuery(id+"F0.wireOp",EDGE,"E609"),sQuery(id+"F0.wireOp",EDGE,"E610"),sQuery(id+"F0.wireOp",EDGE,"E611"),sQuery(id+"F0.wireOp",EDGE,"E612"),sQuery(id+"F0.wireOp",EDGE,"E613"),sQuery(id+"F0.wireOp",EDGE,"E614"),sQuery(id+"F0.wireOp",EDGE,"E615"),sQuery(id+"F0.wireOp",EDGE,"E616"),sQuery(id+"F0.wireOp",EDGE,"E616"),sQuery(id+"F0.wireOp",EDGE,"E617"),sQuery(id+"F0.wireOp",EDGE,"E618"),sQuery(id+"F0.wireOp",EDGE,"E619"),sQuery(id+"F0.wireOp",EDGE,"E620"),sQuery(id+"F0.wireOp",EDGE,"E621"),sQuery(id+"F0.wireOp",EDGE,"E622"),sQuery(id+"F0.wireOp",EDGE,"E623"),sQuery(id+"F0.wireOp",EDGE,"E624"),sQuery(id+"F0.wireOp",EDGE,"E625"),sQuery(id+"F0.wireOp",EDGE,"E626"),sQuery(id+"F0.wireOp",EDGE,"E627"),sQuery(id+"F0.wireOp",EDGE,"E628"),sQuery(id+"F0.wireOp",EDGE,"E629"),sQuery(id+"F0.wireOp",EDGE,"E630"),sQuery(id+"F0.wireOp",EDGE,"E631"),sQuery(id+"F0.wireOp",EDGE,"E632"),sQuery(id+"F0.wireOp",EDGE,"E633"),sQuery(id+"F0.wireOp",EDGE,"E634"),sQuery(id+"F0.wireOp",EDGE,"E635"),sQuery(id+"F0.wireOp",EDGE,"E636"),sQuery(id+"F0.wireOp",EDGE,"E637"),sQuery(id+"F0.wireOp",EDGE,"E638"),sQuery(id+"F0.wireOp",EDGE,"E639"),sQuery(id+"F0.wireOp",EDGE,"E640"),sQuery(id+"F0.wireOp",EDGE,"E641"),sQuery(id+"F0.wireOp",EDGE,"E642"),sQuery(id+"F0.wireOp",EDGE,"E643"),sQuery(id+"F0.wireOp",EDGE,"E644"),sQuery(id+"F0.wireOp",EDGE,"E645"),sQuery(id+"F0.wireOp",EDGE,"E646"),sQuery(id+"F0.wireOp",EDGE,"E647"),sQuery(id+"F0.wireOp",EDGE,"E648"),sQuery(id+"F0.wireOp",EDGE,"E649"),sQuery(id+"F0.wireOp",EDGE,"E650"),sQuery(id+"F0.wireOp",EDGE,"E651"),sQuery(id+"F0.wireOp",EDGE,"E652"),sQuery(id+"F0.wireOp",EDGE,"E653"),sQuery(id+"F0.wireOp",EDGE,"E654"),sQuery(id+"F0.wireOp",EDGE,"E655"),sQuery(id+"F0.wireOp",EDGE,"E656"),sQuery(id+"F0.wireOp",EDGE,"E657"),sQuery(id+"F0.wireOp",EDGE,"E658"),sQuery(id+"F0.wireOp",EDGE,"E659"),sQuery(id+"F0.wireOp",EDGE,"E660"),sQuery(id+"F0.wireOp",EDGE,"E661"),sQuery(id+"F0.wireOp",EDGE,"E662"),sQuery(id+"F0.wireOp",EDGE,"E663"),sQuery(id+"F0.wireOp",EDGE,"E664"),sQuery(id+"F0.wireOp",EDGE,"E665"),sQuery(id+"F0.wireOp",EDGE,"E666"),sQuery(id+"F0.wireOp",EDGE,"E667"),sQuery(id+"F0.wireOp",EDGE,"E668"),sQuery(id+"F0.wireOp",EDGE,"E669"),sQuery(id+"F0.wireOp",EDGE,"E670"),sQuery(id+"F0.wireOp",EDGE,"E671"),sQuery(id+"F0.wireOp",EDGE,"E672"),sQuery(id+"F0.wireOp",EDGE,"E673"),sQuery(id+"F0.wireOp",EDGE,"E674"),sQuery(id+"F0.wireOp",EDGE,"E675"),sQuery(id+"F0.wireOp",EDGE,"E676"),sQuery(id+"F0.wireOp",EDGE,"E677"),sQuery(id+"F0.wireOp",EDGE,"E678"),sQuery(id+"F0.wireOp",EDGE,"E679"),sQuery(id+"F0.wireOp",EDGE,"E679"),sQuery(id+"F0.wireOp",EDGE,"E680"),sQuery(id+"F0.wireOp",EDGE,"E681"),sQuery(id+"F0.wireOp",EDGE,"E682"),sQuery(id+"F0.wireOp",EDGE,"E683"),sQuery(id+"F0.wireOp",EDGE,"E684"),sQuery(id+"F0.wireOp",EDGE,"E685"),sQuery(id+"F0.wireOp",EDGE,"E686"),sQuery(id+"F0.wireOp",EDGE,"E687"),sQuery(id+"F0.wireOp",EDGE,"E688"),sQuery(id+"F0.wireOp",EDGE,"E689"),sQuery(id+"F0.wireOp",EDGE,"E690"),sQuery(id+"F0.wireOp",EDGE,"E691"),sQuery(id+"F0.wireOp",EDGE,"E692"),sQuery(id+"F0.wireOp",EDGE,"E693"),sQuery(id+"F0.wireOp",EDGE,"E694"),sQuery(id+"F0.wireOp",EDGE,"E695"),sQuery(id+"F0.wireOp",EDGE,"E696"),sQuery(id+"F0.wireOp",EDGE,"E697"),sQuery(id+"F0.wireOp",EDGE,"E698"),sQuery(id+"F0.wireOp",EDGE,"E699"),sQuery(id+"F0.wireOp",EDGE,"E700"),sQuery(id+"F0.wireOp",EDGE,"E701"),sQuery(id+"F0.wireOp",EDGE,"E702"),sQuery(id+"F0.wireOp",EDGE,"E703"),sQuery(id+"F0.wireOp",EDGE,"E704"),sQuery(id+"F0.wireOp",EDGE,"E705"),sQuery(id+"F0.wireOp",EDGE,"E706"),sQuery(id+"F0.wireOp",EDGE,"E707"),sQuery(id+"F0.wireOp",EDGE,"E708"),sQuery(id+"F0.wireOp",EDGE,"E709"),sQuery(id+"F0.wireOp",EDGE,"E710"),sQuery(id+"F0.wireOp",EDGE,"E711"),sQuery(id+"F0.wireOp",EDGE,"E712"),sQuery(id+"F0.wireOp",EDGE,"E713"),sQuery(id+"F0.wireOp",EDGE,"E714"),sQuery(id+"F0.wireOp",EDGE,"E715"),sQuery(id+"F0.wireOp",EDGE,"E716"),sQuery(id+"F0.wireOp",EDGE,"E717"),sQuery(id+"F0.wireOp",EDGE,"E718"),sQuery(id+"F0.wireOp",EDGE,"E719"),sQuery(id+"F0.wireOp",EDGE,"E720"),sQuery(id+"F0.wireOp",EDGE,"E721"),sQuery(id+"F0.wireOp",EDGE,"E722"),sQuery(id+"F0.wireOp",EDGE,"E723"),sQuery(id+"F0.wireOp",EDGE,"E724"),sQuery(id+"F0.wireOp",EDGE,"E725"),sQuery(id+"F0.wireOp",EDGE,"E726"),sQuery(id+"F0.wireOp",EDGE,"E727"),sQuery(id+"F0.wireOp",EDGE,"E728"),sQuery(id+"F0.wireOp",EDGE,"E729"),sQuery(id+"F0.wireOp",EDGE,"E730"),sQuery(id+"F0.wireOp",EDGE,"E731"),sQuery(id+"F0.wireOp",EDGE,"E732"),sQuery(id+"F0.wireOp",EDGE,"E733"),sQuery(id+"F0.wireOp",EDGE,"E734"),sQuery(id+"F0.wireOp",EDGE,"E735"),sQuery(id+"F0.wireOp",EDGE,"E736"),sQuery(id+"F0.wireOp",EDGE,"E737"),sQuery(id+"F0.wireOp",EDGE,"E738"),sQuery(id+"F0.wireOp",EDGE,"E739"),sQuery(id+"F0.wireOp",EDGE,"E740"),sQuery(id+"F0.wireOp",EDGE,"E741"),sQuery(id+"F0.wireOp",EDGE,"E742"),sQuery(id+"F0.wireOp",EDGE,"E743"),sQuery(id+"F0.wireOp",EDGE,"E744"),sQuery(id+"F0.wireOp",EDGE,"E745"),sQuery(id+"F0.wireOp",EDGE,"E746"),sQuery(id+"F0.wireOp",EDGE,"E747"),sQuery(id+"F0.wireOp",EDGE,"E748"),sQuery(id+"F0.wireOp",EDGE,"E749"),sQuery(id+"F0.wireOp",EDGE,"E750"),sQuery(id+"F0.wireOp",EDGE,"E751"),sQuery(id+"F0.wireOp",EDGE,"E752"),sQuery(id+"F0.wireOp",EDGE,"E753"),sQuery(id+"F0.wireOp",EDGE,"E754"),sQuery(id+"F0.wireOp",EDGE,"E755"),sQuery(id+"F0.wireOp",EDGE,"E756"),sQuery(id+"F0.wireOp",EDGE,"E757"),sQuery(id+"F0.wireOp",EDGE,"E758"),sQuery(id+"F0.wireOp",EDGE,"E759"),sQuery(id+"F0.wireOp",EDGE,"E760"),sQuery(id+"F0.wireOp",EDGE,"E761"),sQuery(id+"F0.wireOp",EDGE,"E762"),sQuery(id+"F0.wireOp",EDGE,"E763"),sQuery(id+"F0.wireOp",EDGE,"E764"),sQuery(id+"F0.wireOp",EDGE,"E765"),sQuery(id+"F0.wireOp",EDGE,"E766"),sQuery(id+"F0.wireOp",EDGE,"E767"),sQuery(id+"F0.wireOp",EDGE,"E768"),sQuery(id+"F0.wireOp",EDGE,"E769"),sQuery(id+"F0.wireOp",EDGE,"E769"),sQuery(id+"F0.wireOp",EDGE,"E770"),sQuery(id+"F0.wireOp",EDGE,"E771"),sQuery(id+"F0.wireOp",EDGE,"E772"),sQuery(id+"F0.wireOp",EDGE,"E773"),sQuery(id+"F0.wireOp",EDGE,"E774"),sQuery(id+"F0.wireOp",EDGE,"E775"),sQuery(id+"F0.wireOp",EDGE,"E776"),sQuery(id+"F0.wireOp",EDGE,"E777"),sQuery(id+"F0.wireOp",EDGE,"E778"),sQuery(id+"F0.wireOp",EDGE,"E779"),sQuery(id+"F0.wireOp",EDGE,"E780"),sQuery(id+"F0.wireOp",EDGE,"E781"),sQuery(id+"F0.wireOp",EDGE,"E782"),sQuery(id+"F0.wireOp",EDGE,"E783"),sQuery(id+"F0.wireOp",EDGE,"E784"),sQuery(id+"F0.wireOp",EDGE,"E785"),sQuery(id+"F0.wireOp",EDGE,"E786"),sQuery(id+"F0.wireOp",EDGE,"E787"),sQuery(id+"F0.wireOp",EDGE,"E788"),sQuery(id+"F0.wireOp",EDGE,"E789"),sQuery(id+"F0.wireOp",EDGE,"E790"),sQuery(id+"F0.wireOp",EDGE,"E791"),sQuery(id+"F0.wireOp",EDGE,"E792"),sQuery(id+"F0.wireOp",EDGE,"E793"),sQuery(id+"F0.wireOp",EDGE,"E794"),sQuery(id+"F0.wireOp",EDGE,"E795"),sQuery(id+"F0.wireOp",EDGE,"E796"),sQuery(id+"F0.wireOp",EDGE,"E797"),sQuery(id+"F0.wireOp",EDGE,"E798"),sQuery(id+"F0.wireOp",EDGE,"E799"),sQuery(id+"F0.wireOp",EDGE,"E800"),sQuery(id+"F0.wireOp",EDGE,"E801"),sQuery(id+"F0.wireOp",EDGE,"E802"),sQuery(id+"F0.wireOp",EDGE,"E803"),sQuery(id+"F0.wireOp",EDGE,"E804"),sQuery(id+"F0.wireOp",EDGE,"E805"),sQuery(id+"F0.wireOp",EDGE,"E806"),sQuery(id+"F0.wireOp",EDGE,"E807"),sQuery(id+"F0.wireOp",EDGE,"E808"),sQuery(id+"F0.wireOp",EDGE,"E809"),sQuery(id+"F0.wireOp",EDGE,"E809"),sQuery(id+"F0.wireOp",EDGE,"E810"),sQuery(id+"F0.wireOp",EDGE,"E811"),sQuery(id+"F0.wireOp",EDGE,"E812"),sQuery(id+"F0.wireOp",EDGE,"E813"),sQuery(id+"F0.wireOp",EDGE,"E814"),sQuery(id+"F0.wireOp",EDGE,"E815"),sQuery(id+"F0.wireOp",EDGE,"E816"),sQuery(id+"F0.wireOp",EDGE,"E817"),sQuery(id+"F0.wireOp",EDGE,"E818"),sQuery(id+"F0.wireOp",EDGE,"E819"),sQuery(id+"F0.wireOp",EDGE,"E820"),sQuery(id+"F0.wireOp",EDGE,"E821"),sQuery(id+"F0.wireOp",EDGE,"E822"),sQuery(id+"F0.wireOp",EDGE,"E823"),sQuery(id+"F0.wireOp",EDGE,"E824"),sQuery(id+"F0.wireOp",EDGE,"E825"),sQuery(id+"F0.wireOp",EDGE,"E826"),sQuery(id+"F0.wireOp",EDGE,"E827"),sQuery(id+"F0.wireOp",EDGE,"E828"),sQuery(id+"F0.wireOp",EDGE,"E829"),sQuery(id+"F0.wireOp",EDGE,"E830"),sQuery(id+"F0.wireOp",EDGE,"E831"),sQuery(id+"F0.wireOp",EDGE,"E832"),sQuery(id+"F0.wireOp",EDGE,"E833"),sQuery(id+"F0.wireOp",EDGE,"E834"),sQuery(id+"F0.wireOp",EDGE,"E835"),sQuery(id+"F0.wireOp",EDGE,"E836"),sQuery(id+"F0.wireOp",EDGE,"E837"),sQuery(id+"F0.wireOp",EDGE,"E838"),sQuery(id+"F0.wireOp",EDGE,"E839"),sQuery(id+"F0.wireOp",EDGE,"E840"),sQuery(id+"F0.wireOp",EDGE,"E841"),sQuery(id+"F0.wireOp",EDGE,"E842"),sQuery(id+"F0.wireOp",EDGE,"E843"),sQuery(id+"F0.wireOp",EDGE,"E844"),sQuery(id+"F0.wireOp",EDGE,"E845"),sQuery(id+"F0.wireOp",EDGE,"E846"),sQuery(id+"F0.wireOp",EDGE,"E847"),sQuery(id+"F0.wireOp",EDGE,"E848"),sQuery(id+"F0.wireOp",EDGE,"E849"),sQuery(id+"F0.wireOp",EDGE,"E850"),sQuery(id+"F0.wireOp",EDGE,"E851"),sQuery(id+"F0.wireOp",EDGE,"E852"),sQuery(id+"F0.wireOp",EDGE,"E852"),sQuery(id+"F0.wireOp",EDGE,"E852"),sQuery(id+"F0.wireOp",EDGE,"E852"),sQuery(id+"F0.wireOp",EDGE,"E852"),sQuery(id+"F0.wireOp",EDGE,"E853"),sQuery(id+"F0.wireOp",EDGE,"E854"),sQuery(id+"F0.wireOp",EDGE,"E855"),sQuery(id+"F0.wireOp",EDGE,"E856"),sQuery(id+"F0.wireOp",EDGE,"E857"),sQuery(id+"F0.wireOp",EDGE,"E858"),sQuery(id+"F0.wireOp",EDGE,"E859"),sQuery(id+"F0.wireOp",EDGE,"E860"),sQuery(id+"F0.wireOp",EDGE,"E861"),sQuery(id+"F0.wireOp",EDGE,"E862"),sQuery(id+"F0.wireOp",EDGE,"E863"),sQuery(id+"F0.wireOp",EDGE,"E864"),sQuery(id+"F0.wireOp",EDGE,"E865"),sQuery(id+"F0.wireOp",EDGE,"E866"),sQuery(id+"F0.wireOp",EDGE,"E867"),sQuery(id+"F0.wireOp",EDGE,"E868"),sQuery(id+"F0.wireOp",EDGE,"E869"),sQuery(id+"F0.wireOp",EDGE,"E870"),sQuery(id+"F0.wireOp",EDGE,"E871"),sQuery(id+"F0.wireOp",EDGE,"E872"),sQuery(id+"F0.wireOp",EDGE,"E873"),sQuery(id+"F0.wireOp",EDGE,"E874"),sQuery(id+"F0.wireOp",EDGE,"E875"),sQuery(id+"F0.wireOp",EDGE,"E876"),sQuery(id+"F0.wireOp",EDGE,"E877"),sQuery(id+"F0.wireOp",EDGE,"E878"),sQuery(id+"F0.wireOp",EDGE,"E879"),sQuery(id+"F0.wireOp",EDGE,"E880"),sQuery(id+"F0.wireOp",EDGE,"E881"),sQuery(id+"F0.wireOp",EDGE,"E882"),sQuery(id+"F0.wireOp",EDGE,"E883"),sQuery(id+"F0.wireOp",EDGE,"E884"),sQuery(id+"F0.wireOp",EDGE,"E885"),sQuery(id+"F0.wireOp",EDGE,"E886"),sQuery(id+"F0.wireOp",EDGE,"E887"),sQuery(id+"F0.wireOp",EDGE,"E888"),sQuery(id+"F0.wireOp",EDGE,"E889"),sQuery(id+"F0.wireOp",EDGE,"E890")])],"isStart":true});
            extrude(context, id + "F3", {"entities" : qUnion([Q0]), "operationType" : NewBodyOperationType.ADD, "endBound" : BoundingType.UP_TO_SURFACE, "oppositeDirection" : true, "depth" : 25.4 * mm, "endBoundEntityFace" : qUnion([Q1]), "offsetDistance" : 25.4 * mm});
        }
    });
